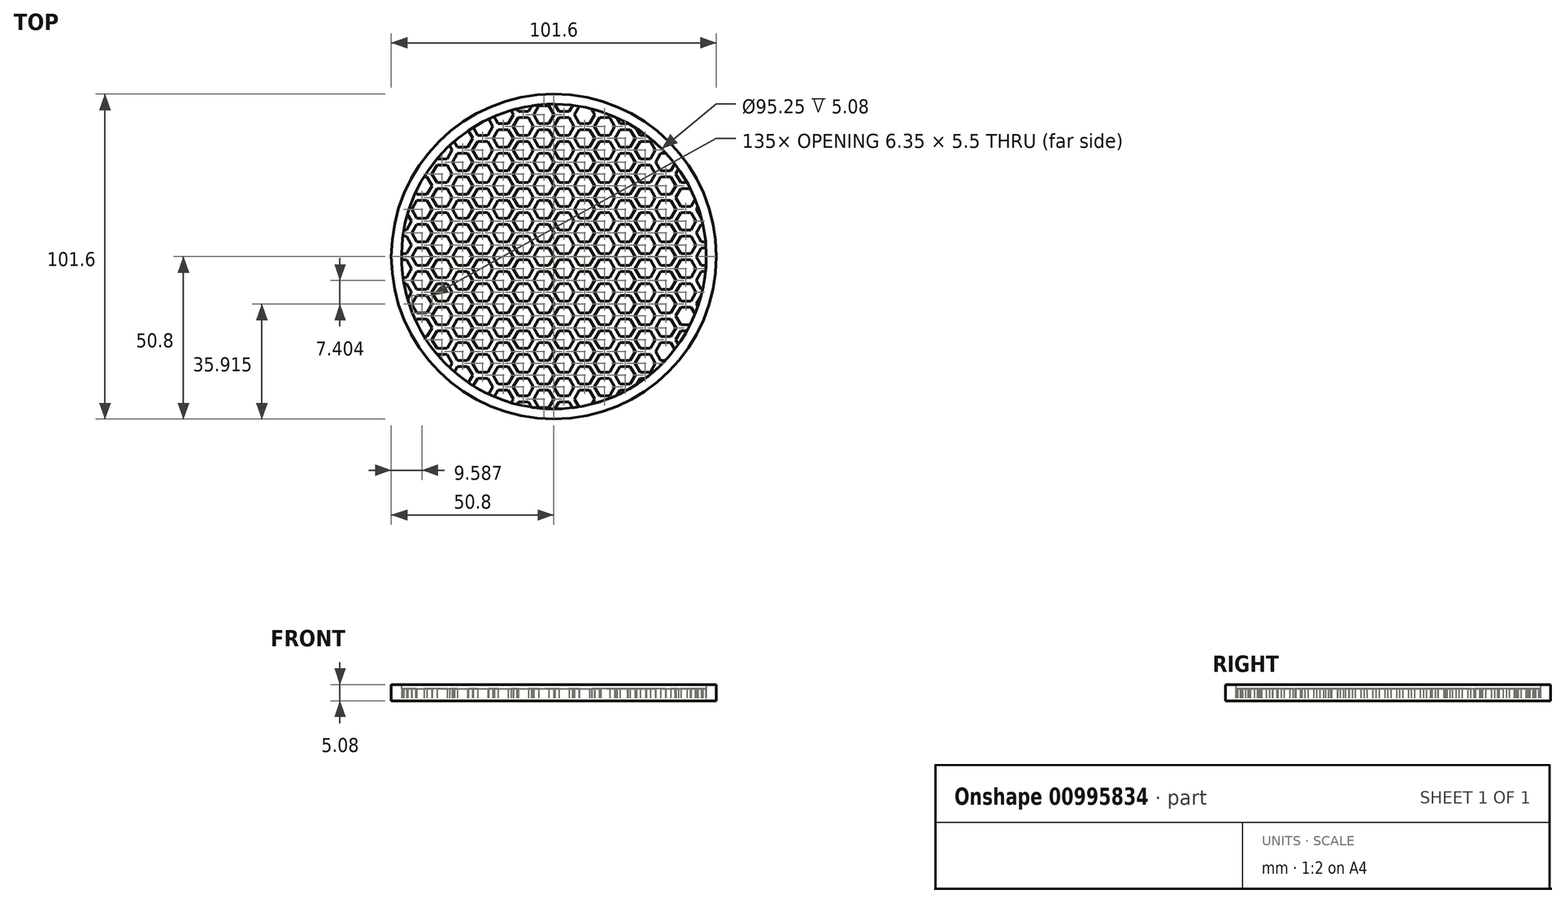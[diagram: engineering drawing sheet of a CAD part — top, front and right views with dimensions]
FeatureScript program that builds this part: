
annotation { "Feature Type Name" : "Feature", "Feature Type Description" : "" }
export const myFeature = defineFeature(function(context is Context, id is Id, definition is map)
    precondition{}
    {
        {
            var Q0;
            Q0=qCreatedBy(makeId("Top.planeOp"),FACE);
            var sketch = newSketch(context, id + "F0", { "sketchPlane" : qUnion([Q0])});
            skLineSegment(sketch, "E0.bottom", {"start": v(50.8, -50.8) * mm, "end": v(-50.8, -50.8) * mm});
            skLineSegment(sketch, "E0.top", {"start": v(50.8, 50.8) * mm, "end": v(-50.8, 50.8) * mm, "construction": true});
            skLineSegment(sketch, "E0.left", {"start": v(50.8, -50.8) * mm, "end": v(50.8, 50.8) * mm});
            skLineSegment(sketch, "E0.right", {"start": v(-50.8, -50.8) * mm, "end": v(-50.8, 50.8) * mm});
            skPoint(sketch, "E0.middle", {"position": v(0, 0) * mm});
            skCircle(sketch, "E1.cCircle", {"center": v(-47.63, 48.05) * mm, "radius": 3.18 * mm, "construction": true});
            skLineSegment(sketch, "E1.0", {"start": v(-46.04, 45.3) * mm, "end": v(-49.21, 45.3) * mm});
            skLineSegment(sketch, "E1.1", {"start": v(-49.21, 45.3) * mm, "end": v(-50.8, 48.05) * mm});
            skLineSegment(sketch, "E1.2", {"start": v(-50.8, 48.05) * mm, "end": v(-49.21, 50.8) * mm});
            skLineSegment(sketch, "E1.3", {"start": v(-49.21, 50.8) * mm, "end": v(-46.04, 50.8) * mm});
            skLineSegment(sketch, "E1.4", {"start": v(-46.04, 50.8) * mm, "end": v(-44.45, 48.05) * mm});
            skLineSegment(sketch, "E1.5", {"start": v(-44.45, 48.05) * mm, "end": v(-46.04, 45.3) * mm});
            skCircle(sketch, "E2.cCircle", {"center": v(-41.21, 44.35) * mm, "radius": 3.18 * mm, "construction": true});
            skLineSegment(sketch, "E2.0", {"start": v(-39.63, 47.1) * mm, "end": v(-38.04, 44.35) * mm});
            skLineSegment(sketch, "E2.1", {"start": v(-38.04, 44.35) * mm, "end": v(-39.63, 41.6) * mm});
            skLineSegment(sketch, "E2.2", {"start": v(-39.63, 41.6) * mm, "end": v(-42.8, 41.6) * mm});
            skLineSegment(sketch, "E2.3", {"start": v(-42.8, 41.6) * mm, "end": v(-44.39, 44.35) * mm});
            skLineSegment(sketch, "E2.4", {"start": v(-44.39, 44.35) * mm, "end": v(-42.8, 47.1) * mm});
            skLineSegment(sketch, "E2.5", {"start": v(-42.8, 47.1) * mm, "end": v(-39.63, 47.1) * mm});
            skCircle(sketch, "E3.cCircle", {"center": v(-41.21, 51.75) * mm, "radius": 3.18 * mm, "construction": true});
            skPoint(sketch, "E3.cCircle.centerSnap0", {"position": v(-41.21, 47.1) * mm});
            skLineSegment(sketch, "E3.0", {"start": v(-38.04, 51.75) * mm, "end": v(-39.63, 49) * mm});
            skLineSegment(sketch, "E3.1", {"start": v(-39.63, 49) * mm, "end": v(-42.8, 49) * mm});
            skLineSegment(sketch, "E3.2", {"start": v(-42.8, 49) * mm, "end": v(-44.39, 51.75) * mm});
            skLineSegment(sketch, "E3.3", {"start": v(-44.39, 51.75) * mm, "end": v(-42.8, 54.5) * mm});
            skLineSegment(sketch, "E3.4", {"start": v(-42.8, 54.5) * mm, "end": v(-39.63, 54.5) * mm});
            skLineSegment(sketch, "E3.5", {"start": v(-39.63, 54.5) * mm, "end": v(-38.04, 51.75) * mm});
            skCircle(sketch, "E4.cCircle", {"center": v(-47.63, 40.65) * mm, "radius": 3.18 * mm, "construction": true});
            skPoint(sketch, "E4.cCircle.centerSnap0", {"position": v(-47.62, 45.3) * mm});
            skLineSegment(sketch, "E4.0", {"start": v(-49.21, 37.9) * mm, "end": v(-50.8, 40.65) * mm});
            skLineSegment(sketch, "E4.1", {"start": v(-50.8, 40.65) * mm, "end": v(-49.21, 43.4) * mm});
            skLineSegment(sketch, "E4.2", {"start": v(-49.21, 43.4) * mm, "end": v(-46.04, 43.4) * mm});
            skLineSegment(sketch, "E4.3", {"start": v(-46.04, 43.4) * mm, "end": v(-44.45, 40.65) * mm});
            skLineSegment(sketch, "E4.4", {"start": v(-44.45, 40.65) * mm, "end": v(-46.04, 37.9) * mm});
            skLineSegment(sketch, "E4.5", {"start": v(-46.04, 37.9) * mm, "end": v(-49.21, 37.9) * mm});
            skLineSegment(sketch, "E5.0.1.0", {"start": v(-42.8, 32.29) * mm, "end": v(-39.63, 32.29) * mm});
            skLineSegment(sketch, "E5.0.1.1", {"start": v(-46.04, 30.5) * mm, "end": v(-49.21, 30.5) * mm});
            skLineSegment(sketch, "E5.0.1.2", {"start": v(-44.45, 25.84) * mm, "end": v(-46.04, 23.09) * mm});
            skLineSegment(sketch, "E5.0.1.3", {"start": v(-39.63, 32.29) * mm, "end": v(-38.04, 29.54) * mm});
            skLineSegment(sketch, "E5.0.1.4", {"start": v(-44.39, 36.94) * mm, "end": v(-42.8, 39.7) * mm});
            skLineSegment(sketch, "E5.0.1.5", {"start": v(-50.8, 33.24) * mm, "end": v(-49.21, 36) * mm});
            skLineSegment(sketch, "E5.0.1.6", {"start": v(-39.63, 39.7) * mm, "end": v(-38.04, 36.94) * mm});
            skLineSegment(sketch, "E5.0.1.7", {"start": v(-39.63, 26.8) * mm, "end": v(-42.8, 26.8) * mm});
            skLineSegment(sketch, "E5.0.1.8", {"start": v(-38.04, 36.94) * mm, "end": v(-39.63, 34.2) * mm});
            skLineSegment(sketch, "E5.0.1.9", {"start": v(-50.8, 25.84) * mm, "end": v(-49.21, 28.59) * mm});
            skLineSegment(sketch, "E5.0.1.10", {"start": v(-46.04, 36) * mm, "end": v(-44.45, 33.24) * mm});
            skLineSegment(sketch, "E5.0.1.11", {"start": v(-44.39, 29.54) * mm, "end": v(-42.8, 32.29) * mm});
            skLineSegment(sketch, "E5.0.1.12", {"start": v(-42.8, 34.2) * mm, "end": v(-44.39, 36.94) * mm});
            skLineSegment(sketch, "E5.0.1.13", {"start": v(-46.04, 28.59) * mm, "end": v(-44.45, 25.84) * mm});
            skLineSegment(sketch, "E5.0.1.14", {"start": v(-42.8, 39.7) * mm, "end": v(-39.63, 39.7) * mm});
            skLineSegment(sketch, "E5.0.1.15", {"start": v(-46.04, 23.09) * mm, "end": v(-49.21, 23.09) * mm});
            skLineSegment(sketch, "E5.0.1.16", {"start": v(-49.21, 30.5) * mm, "end": v(-50.8, 33.24) * mm});
            skLineSegment(sketch, "E5.0.1.17", {"start": v(-38.04, 29.54) * mm, "end": v(-39.63, 26.8) * mm});
            skLineSegment(sketch, "E5.0.1.18", {"start": v(-49.21, 23.09) * mm, "end": v(-50.8, 25.84) * mm});
            skLineSegment(sketch, "E5.0.1.19", {"start": v(-49.21, 36) * mm, "end": v(-46.04, 36) * mm});
            skLineSegment(sketch, "E5.0.1.20", {"start": v(-42.8, 26.8) * mm, "end": v(-44.39, 29.54) * mm});
            skLineSegment(sketch, "E5.0.1.21", {"start": v(-39.63, 34.2) * mm, "end": v(-42.8, 34.2) * mm});
            skLineSegment(sketch, "E5.0.1.22", {"start": v(-49.21, 28.59) * mm, "end": v(-46.04, 28.59) * mm});
            skLineSegment(sketch, "E5.0.1.23", {"start": v(-44.45, 33.24) * mm, "end": v(-46.04, 30.5) * mm});
            skLineSegment(sketch, "E5.0.2.0", {"start": v(-42.8, 17.48) * mm, "end": v(-39.63, 17.48) * mm});
            skLineSegment(sketch, "E5.0.2.1", {"start": v(-46.04, 15.68) * mm, "end": v(-49.21, 15.68) * mm});
            skLineSegment(sketch, "E5.0.2.2", {"start": v(-44.45, 11.03) * mm, "end": v(-46.04, 8.28) * mm});
            skLineSegment(sketch, "E5.0.2.3", {"start": v(-39.63, 17.48) * mm, "end": v(-38.04, 14.73) * mm});
            skLineSegment(sketch, "E5.0.2.4", {"start": v(-44.39, 22.14) * mm, "end": v(-42.8, 24.89) * mm});
            skLineSegment(sketch, "E5.0.2.5", {"start": v(-50.8, 18.43) * mm, "end": v(-49.21, 21.18) * mm});
            skLineSegment(sketch, "E5.0.2.6", {"start": v(-39.63, 24.89) * mm, "end": v(-38.04, 22.14) * mm});
            skLineSegment(sketch, "E5.0.2.7", {"start": v(-39.63, 11.98) * mm, "end": v(-42.8, 11.98) * mm});
            skLineSegment(sketch, "E5.0.2.8", {"start": v(-38.04, 22.14) * mm, "end": v(-39.63, 19.39) * mm});
            skLineSegment(sketch, "E5.0.2.9", {"start": v(-50.8, 11.03) * mm, "end": v(-49.21, 13.78) * mm});
            skLineSegment(sketch, "E5.0.2.10", {"start": v(-46.04, 21.18) * mm, "end": v(-44.45, 18.43) * mm});
            skLineSegment(sketch, "E5.0.2.11", {"start": v(-44.39, 14.73) * mm, "end": v(-42.8, 17.48) * mm});
            skLineSegment(sketch, "E5.0.2.12", {"start": v(-42.8, 19.39) * mm, "end": v(-44.39, 22.14) * mm});
            skLineSegment(sketch, "E5.0.2.13", {"start": v(-46.04, 13.78) * mm, "end": v(-44.45, 11.03) * mm});
            skLineSegment(sketch, "E5.0.2.14", {"start": v(-42.8, 24.89) * mm, "end": v(-39.63, 24.89) * mm});
            skLineSegment(sketch, "E5.0.2.15", {"start": v(-46.04, 8.28) * mm, "end": v(-49.21, 8.28) * mm});
            skLineSegment(sketch, "E5.0.2.16", {"start": v(-49.21, 15.68) * mm, "end": v(-50.8, 18.43) * mm});
            skLineSegment(sketch, "E5.0.2.17", {"start": v(-38.04, 14.73) * mm, "end": v(-39.63, 11.98) * mm});
            skLineSegment(sketch, "E5.0.2.18", {"start": v(-49.21, 8.28) * mm, "end": v(-50.8, 11.03) * mm});
            skLineSegment(sketch, "E5.0.2.19", {"start": v(-49.21, 21.18) * mm, "end": v(-46.04, 21.18) * mm});
            skLineSegment(sketch, "E5.0.2.20", {"start": v(-42.8, 11.98) * mm, "end": v(-44.39, 14.73) * mm});
            skLineSegment(sketch, "E5.0.2.21", {"start": v(-39.63, 19.39) * mm, "end": v(-42.8, 19.39) * mm});
            skLineSegment(sketch, "E5.0.2.22", {"start": v(-49.21, 13.78) * mm, "end": v(-46.04, 13.78) * mm});
            skLineSegment(sketch, "E5.0.2.23", {"start": v(-44.45, 18.43) * mm, "end": v(-46.04, 15.68) * mm});
            skLineSegment(sketch, "E5.0.3.0", {"start": v(-42.8, 2.67) * mm, "end": v(-39.63, 2.67) * mm});
            skLineSegment(sketch, "E5.0.3.1", {"start": v(-46.04, 0.88) * mm, "end": v(-49.21, 0.88) * mm});
            skLineSegment(sketch, "E5.0.3.2", {"start": v(-44.45, -3.78) * mm, "end": v(-46.04, -6.53) * mm});
            skLineSegment(sketch, "E5.0.3.3", {"start": v(-39.63, 2.67) * mm, "end": v(-38.04, -0.08) * mm});
            skLineSegment(sketch, "E5.0.3.4", {"start": v(-44.39, 7.33) * mm, "end": v(-42.8, 10.08) * mm});
            skLineSegment(sketch, "E5.0.3.5", {"start": v(-50.8, 3.63) * mm, "end": v(-49.21, 6.38) * mm});
            skLineSegment(sketch, "E5.0.3.6", {"start": v(-39.63, 10.08) * mm, "end": v(-38.04, 7.33) * mm});
            skLineSegment(sketch, "E5.0.3.7", {"start": v(-39.63, -2.83) * mm, "end": v(-42.8, -2.83) * mm});
            skLineSegment(sketch, "E5.0.3.8", {"start": v(-38.04, 7.33) * mm, "end": v(-39.63, 4.58) * mm});
            skLineSegment(sketch, "E5.0.3.9", {"start": v(-50.8, -3.78) * mm, "end": v(-49.21, -1.03) * mm});
            skLineSegment(sketch, "E5.0.3.10", {"start": v(-46.04, 6.38) * mm, "end": v(-44.45, 3.63) * mm});
            skLineSegment(sketch, "E5.0.3.11", {"start": v(-44.39, -0.08) * mm, "end": v(-42.8, 2.67) * mm});
            skLineSegment(sketch, "E5.0.3.12", {"start": v(-42.8, 4.58) * mm, "end": v(-44.39, 7.33) * mm});
            skLineSegment(sketch, "E5.0.3.13", {"start": v(-46.04, -1.03) * mm, "end": v(-44.45, -3.78) * mm});
            skLineSegment(sketch, "E5.0.3.14", {"start": v(-42.8, 10.08) * mm, "end": v(-39.63, 10.08) * mm});
            skLineSegment(sketch, "E5.0.3.15", {"start": v(-46.04, -6.53) * mm, "end": v(-49.21, -6.53) * mm});
            skLineSegment(sketch, "E5.0.3.16", {"start": v(-49.21, 0.88) * mm, "end": v(-50.8, 3.63) * mm});
            skLineSegment(sketch, "E5.0.3.17", {"start": v(-38.04, -0.08) * mm, "end": v(-39.63, -2.83) * mm});
            skLineSegment(sketch, "E5.0.3.18", {"start": v(-49.21, -6.53) * mm, "end": v(-50.8, -3.78) * mm});
            skLineSegment(sketch, "E5.0.3.19", {"start": v(-49.21, 6.38) * mm, "end": v(-46.04, 6.38) * mm});
            skLineSegment(sketch, "E5.0.3.20", {"start": v(-42.8, -2.83) * mm, "end": v(-44.39, -0.08) * mm});
            skLineSegment(sketch, "E5.0.3.21", {"start": v(-39.63, 4.58) * mm, "end": v(-42.8, 4.58) * mm});
            skLineSegment(sketch, "E5.0.3.22", {"start": v(-49.21, -1.03) * mm, "end": v(-46.04, -1.03) * mm});
            skLineSegment(sketch, "E5.0.3.23", {"start": v(-44.45, 3.63) * mm, "end": v(-46.04, 0.88) * mm});
            skLineSegment(sketch, "E5.0.4.0", {"start": v(-42.8, -12.13) * mm, "end": v(-39.63, -12.13) * mm});
            skLineSegment(sketch, "E5.0.4.1", {"start": v(-46.04, -13.93) * mm, "end": v(-49.21, -13.93) * mm});
            skLineSegment(sketch, "E5.0.4.2", {"start": v(-44.45, -18.59) * mm, "end": v(-46.04, -21.34) * mm});
            skLineSegment(sketch, "E5.0.4.3", {"start": v(-39.63, -12.13) * mm, "end": v(-38.04, -14.88) * mm});
            skLineSegment(sketch, "E5.0.4.4", {"start": v(-44.39, -7.48) * mm, "end": v(-42.8, -4.73) * mm});
            skLineSegment(sketch, "E5.0.4.5", {"start": v(-50.8, -11.18) * mm, "end": v(-49.21, -8.43) * mm});
            skLineSegment(sketch, "E5.0.4.6", {"start": v(-39.63, -4.73) * mm, "end": v(-38.04, -7.48) * mm});
            skLineSegment(sketch, "E5.0.4.7", {"start": v(-39.63, -17.63) * mm, "end": v(-42.8, -17.63) * mm});
            skLineSegment(sketch, "E5.0.4.8", {"start": v(-38.04, -7.48) * mm, "end": v(-39.63, -10.23) * mm});
            skLineSegment(sketch, "E5.0.4.9", {"start": v(-50.8, -18.59) * mm, "end": v(-49.21, -15.84) * mm});
            skLineSegment(sketch, "E5.0.4.10", {"start": v(-46.04, -8.43) * mm, "end": v(-44.45, -11.18) * mm});
            skLineSegment(sketch, "E5.0.4.11", {"start": v(-44.39, -14.88) * mm, "end": v(-42.8, -12.13) * mm});
            skLineSegment(sketch, "E5.0.4.12", {"start": v(-42.8, -10.23) * mm, "end": v(-44.39, -7.48) * mm});
            skLineSegment(sketch, "E5.0.4.13", {"start": v(-46.04, -15.84) * mm, "end": v(-44.45, -18.59) * mm});
            skLineSegment(sketch, "E5.0.4.14", {"start": v(-42.8, -4.73) * mm, "end": v(-39.63, -4.73) * mm});
            skLineSegment(sketch, "E5.0.4.15", {"start": v(-46.04, -21.34) * mm, "end": v(-49.21, -21.34) * mm});
            skLineSegment(sketch, "E5.0.4.16", {"start": v(-49.21, -13.93) * mm, "end": v(-50.8, -11.18) * mm});
            skLineSegment(sketch, "E5.0.4.17", {"start": v(-38.04, -14.88) * mm, "end": v(-39.63, -17.63) * mm});
            skLineSegment(sketch, "E5.0.4.18", {"start": v(-49.21, -21.34) * mm, "end": v(-50.8, -18.59) * mm});
            skLineSegment(sketch, "E5.0.4.19", {"start": v(-49.21, -8.43) * mm, "end": v(-46.04, -8.43) * mm});
            skLineSegment(sketch, "E5.0.4.20", {"start": v(-42.8, -17.63) * mm, "end": v(-44.39, -14.88) * mm});
            skLineSegment(sketch, "E5.0.4.21", {"start": v(-39.63, -10.23) * mm, "end": v(-42.8, -10.23) * mm});
            skLineSegment(sketch, "E5.0.4.22", {"start": v(-49.21, -15.84) * mm, "end": v(-46.04, -15.84) * mm});
            skLineSegment(sketch, "E5.0.4.23", {"start": v(-44.45, -11.18) * mm, "end": v(-46.04, -13.93) * mm});
            skLineSegment(sketch, "E5.0.5.0", {"start": v(-42.8, -26.94) * mm, "end": v(-39.63, -26.94) * mm});
            skLineSegment(sketch, "E5.0.5.1", {"start": v(-46.04, -28.74) * mm, "end": v(-49.21, -28.74) * mm});
            skLineSegment(sketch, "E5.0.5.2", {"start": v(-44.45, -33.4) * mm, "end": v(-46.04, -36.14) * mm});
            skLineSegment(sketch, "E5.0.5.3", {"start": v(-39.63, -26.94) * mm, "end": v(-38.04, -29.7) * mm});
            skLineSegment(sketch, "E5.0.5.4", {"start": v(-44.39, -22.29) * mm, "end": v(-42.8, -19.54) * mm});
            skLineSegment(sketch, "E5.0.5.5", {"start": v(-50.8, -26) * mm, "end": v(-49.21, -23.24) * mm});
            skLineSegment(sketch, "E5.0.5.6", {"start": v(-39.63, -19.54) * mm, "end": v(-38.04, -22.29) * mm});
            skLineSegment(sketch, "E5.0.5.7", {"start": v(-39.63, -32.44) * mm, "end": v(-42.8, -32.44) * mm});
            skLineSegment(sketch, "E5.0.5.8", {"start": v(-38.04, -22.29) * mm, "end": v(-39.63, -25.04) * mm});
            skLineSegment(sketch, "E5.0.5.9", {"start": v(-50.8, -33.4) * mm, "end": v(-49.21, -30.65) * mm});
            skLineSegment(sketch, "E5.0.5.10", {"start": v(-46.04, -23.24) * mm, "end": v(-44.45, -26) * mm});
            skLineSegment(sketch, "E5.0.5.11", {"start": v(-44.39, -29.7) * mm, "end": v(-42.8, -26.94) * mm});
            skLineSegment(sketch, "E5.0.5.12", {"start": v(-42.8, -25.04) * mm, "end": v(-44.39, -22.29) * mm});
            skLineSegment(sketch, "E5.0.5.13", {"start": v(-46.04, -30.65) * mm, "end": v(-44.45, -33.4) * mm});
            skLineSegment(sketch, "E5.0.5.14", {"start": v(-42.8, -19.54) * mm, "end": v(-39.63, -19.54) * mm});
            skLineSegment(sketch, "E5.0.5.15", {"start": v(-46.04, -36.14) * mm, "end": v(-49.21, -36.14) * mm});
            skLineSegment(sketch, "E5.0.5.16", {"start": v(-49.21, -28.74) * mm, "end": v(-50.8, -26) * mm});
            skLineSegment(sketch, "E5.0.5.17", {"start": v(-38.04, -29.7) * mm, "end": v(-39.63, -32.44) * mm});
            skLineSegment(sketch, "E5.0.5.18", {"start": v(-49.21, -36.14) * mm, "end": v(-50.8, -33.4) * mm});
            skLineSegment(sketch, "E5.0.5.19", {"start": v(-49.21, -23.24) * mm, "end": v(-46.04, -23.24) * mm});
            skLineSegment(sketch, "E5.0.5.20", {"start": v(-42.8, -32.44) * mm, "end": v(-44.39, -29.7) * mm});
            skLineSegment(sketch, "E5.0.5.21", {"start": v(-39.63, -25.04) * mm, "end": v(-42.8, -25.04) * mm});
            skLineSegment(sketch, "E5.0.5.22", {"start": v(-49.21, -30.65) * mm, "end": v(-46.04, -30.65) * mm});
            skLineSegment(sketch, "E5.0.5.23", {"start": v(-44.45, -26) * mm, "end": v(-46.04, -28.74) * mm});
            skLineSegment(sketch, "E5.0.6.0", {"start": v(-42.8, -41.75) * mm, "end": v(-39.63, -41.75) * mm});
            skLineSegment(sketch, "E5.0.6.1", {"start": v(-46.04, -43.55) * mm, "end": v(-49.21, -43.55) * mm});
            skLineSegment(sketch, "E5.0.6.2", {"start": v(-44.45, -48.2) * mm, "end": v(-46.04, -50.95) * mm});
            skLineSegment(sketch, "E5.0.6.3", {"start": v(-39.63, -41.75) * mm, "end": v(-38.04, -44.5) * mm});
            skLineSegment(sketch, "E5.0.6.4", {"start": v(-44.39, -37.1) * mm, "end": v(-42.8, -34.35) * mm});
            skLineSegment(sketch, "E5.0.6.5", {"start": v(-50.8, -40.8) * mm, "end": v(-49.21, -38.05) * mm});
            skLineSegment(sketch, "E5.0.6.6", {"start": v(-39.63, -34.35) * mm, "end": v(-38.04, -37.1) * mm});
            skLineSegment(sketch, "E5.0.6.7", {"start": v(-39.63, -47.25) * mm, "end": v(-42.8, -47.25) * mm});
            skLineSegment(sketch, "E5.0.6.8", {"start": v(-38.04, -37.1) * mm, "end": v(-39.63, -39.85) * mm});
            skLineSegment(sketch, "E5.0.6.9", {"start": v(-50.8, -48.2) * mm, "end": v(-49.21, -45.45) * mm});
            skLineSegment(sketch, "E5.0.6.10", {"start": v(-46.04, -38.05) * mm, "end": v(-44.45, -40.8) * mm});
            skLineSegment(sketch, "E5.0.6.11", {"start": v(-44.39, -44.5) * mm, "end": v(-42.8, -41.75) * mm});
            skLineSegment(sketch, "E5.0.6.12", {"start": v(-42.8, -39.85) * mm, "end": v(-44.39, -37.1) * mm});
            skLineSegment(sketch, "E5.0.6.13", {"start": v(-46.04, -45.45) * mm, "end": v(-44.45, -48.2) * mm});
            skLineSegment(sketch, "E5.0.6.14", {"start": v(-42.8, -34.35) * mm, "end": v(-39.63, -34.35) * mm});
            skLineSegment(sketch, "E5.0.6.15", {"start": v(-46.04, -50.95) * mm, "end": v(-49.21, -50.95) * mm});
            skLineSegment(sketch, "E5.0.6.16", {"start": v(-49.21, -43.55) * mm, "end": v(-50.8, -40.8) * mm});
            skLineSegment(sketch, "E5.0.6.17", {"start": v(-38.04, -44.5) * mm, "end": v(-39.63, -47.25) * mm});
            skLineSegment(sketch, "E5.0.6.18", {"start": v(-49.21, -50.95) * mm, "end": v(-50.8, -48.2) * mm});
            skLineSegment(sketch, "E5.0.6.19", {"start": v(-49.21, -38.05) * mm, "end": v(-46.04, -38.05) * mm});
            skLineSegment(sketch, "E5.0.6.20", {"start": v(-42.8, -47.25) * mm, "end": v(-44.39, -44.5) * mm});
            skLineSegment(sketch, "E5.0.6.21", {"start": v(-39.63, -39.85) * mm, "end": v(-42.8, -39.85) * mm});
            skLineSegment(sketch, "E5.0.6.22", {"start": v(-49.21, -45.45) * mm, "end": v(-46.04, -45.45) * mm});
            skLineSegment(sketch, "E5.0.6.23", {"start": v(-44.45, -40.8) * mm, "end": v(-46.04, -43.55) * mm});
            skLineSegment(sketch, "E5.1.0.0", {"start": v(-30.1, 47.1) * mm, "end": v(-26.93, 47.1) * mm});
            skLineSegment(sketch, "E5.1.0.1", {"start": v(-33.34, 45.3) * mm, "end": v(-36.51, 45.3) * mm});
            skLineSegment(sketch, "E5.1.0.2", {"start": v(-31.75, 40.65) * mm, "end": v(-33.34, 37.9) * mm});
            skLineSegment(sketch, "E5.1.0.3", {"start": v(-26.93, 47.1) * mm, "end": v(-25.34, 44.35) * mm});
            skLineSegment(sketch, "E5.1.0.4", {"start": v(-31.69, 51.75) * mm, "end": v(-30.1, 54.5) * mm});
            skLineSegment(sketch, "E5.1.0.5", {"start": v(-38.1, 48.05) * mm, "end": v(-36.51, 50.8) * mm});
            skLineSegment(sketch, "E5.1.0.6", {"start": v(-26.93, 54.5) * mm, "end": v(-25.34, 51.75) * mm});
            skLineSegment(sketch, "E5.1.0.7", {"start": v(-26.93, 41.6) * mm, "end": v(-30.1, 41.6) * mm});
            skLineSegment(sketch, "E5.1.0.8", {"start": v(-25.34, 51.75) * mm, "end": v(-26.93, 49) * mm});
            skLineSegment(sketch, "E5.1.0.9", {"start": v(-38.1, 40.65) * mm, "end": v(-36.51, 43.4) * mm});
            skLineSegment(sketch, "E5.1.0.10", {"start": v(-33.34, 50.8) * mm, "end": v(-31.75, 48.05) * mm});
            skLineSegment(sketch, "E5.1.0.11", {"start": v(-31.69, 44.35) * mm, "end": v(-30.1, 47.1) * mm});
            skLineSegment(sketch, "E5.1.0.12", {"start": v(-30.1, 49) * mm, "end": v(-31.69, 51.75) * mm});
            skLineSegment(sketch, "E5.1.0.13", {"start": v(-33.34, 43.4) * mm, "end": v(-31.75, 40.65) * mm});
            skLineSegment(sketch, "E5.1.0.14", {"start": v(-30.1, 54.5) * mm, "end": v(-26.93, 54.5) * mm});
            skLineSegment(sketch, "E5.1.0.15", {"start": v(-33.34, 37.9) * mm, "end": v(-36.51, 37.9) * mm});
            skLineSegment(sketch, "E5.1.0.16", {"start": v(-36.51, 45.3) * mm, "end": v(-38.1, 48.05) * mm});
            skLineSegment(sketch, "E5.1.0.17", {"start": v(-25.34, 44.35) * mm, "end": v(-26.93, 41.6) * mm});
            skLineSegment(sketch, "E5.1.0.18", {"start": v(-36.51, 37.9) * mm, "end": v(-38.1, 40.65) * mm});
            skLineSegment(sketch, "E5.1.0.19", {"start": v(-36.51, 50.8) * mm, "end": v(-33.34, 50.8) * mm});
            skLineSegment(sketch, "E5.1.0.20", {"start": v(-30.1, 41.6) * mm, "end": v(-31.69, 44.35) * mm});
            skLineSegment(sketch, "E5.1.0.21", {"start": v(-26.93, 49) * mm, "end": v(-30.1, 49) * mm});
            skLineSegment(sketch, "E5.1.0.22", {"start": v(-36.51, 43.4) * mm, "end": v(-33.34, 43.4) * mm});
            skLineSegment(sketch, "E5.1.0.23", {"start": v(-31.75, 48.05) * mm, "end": v(-33.34, 45.3) * mm});
            skLineSegment(sketch, "E5.1.1.0", {"start": v(-30.1, 32.29) * mm, "end": v(-26.93, 32.29) * mm});
            skLineSegment(sketch, "E5.1.1.1", {"start": v(-33.34, 30.5) * mm, "end": v(-36.51, 30.5) * mm});
            skLineSegment(sketch, "E5.1.1.2", {"start": v(-31.75, 25.84) * mm, "end": v(-33.34, 23.09) * mm});
            skLineSegment(sketch, "E5.1.1.3", {"start": v(-26.93, 32.29) * mm, "end": v(-25.34, 29.54) * mm});
            skLineSegment(sketch, "E5.1.1.4", {"start": v(-31.69, 36.94) * mm, "end": v(-30.1, 39.7) * mm});
            skLineSegment(sketch, "E5.1.1.5", {"start": v(-38.1, 33.24) * mm, "end": v(-36.51, 36) * mm});
            skLineSegment(sketch, "E5.1.1.6", {"start": v(-26.93, 39.7) * mm, "end": v(-25.34, 36.94) * mm});
            skLineSegment(sketch, "E5.1.1.7", {"start": v(-26.93, 26.8) * mm, "end": v(-30.1, 26.8) * mm});
            skLineSegment(sketch, "E5.1.1.8", {"start": v(-25.34, 36.94) * mm, "end": v(-26.93, 34.2) * mm});
            skLineSegment(sketch, "E5.1.1.9", {"start": v(-38.1, 25.84) * mm, "end": v(-36.51, 28.59) * mm});
            skLineSegment(sketch, "E5.1.1.10", {"start": v(-33.34, 36) * mm, "end": v(-31.75, 33.24) * mm});
            skLineSegment(sketch, "E5.1.1.11", {"start": v(-31.69, 29.54) * mm, "end": v(-30.1, 32.29) * mm});
            skLineSegment(sketch, "E5.1.1.12", {"start": v(-30.1, 34.2) * mm, "end": v(-31.69, 36.94) * mm});
            skLineSegment(sketch, "E5.1.1.13", {"start": v(-33.34, 28.59) * mm, "end": v(-31.75, 25.84) * mm});
            skLineSegment(sketch, "E5.1.1.14", {"start": v(-30.1, 39.7) * mm, "end": v(-26.93, 39.7) * mm});
            skLineSegment(sketch, "E5.1.1.15", {"start": v(-33.34, 23.09) * mm, "end": v(-36.51, 23.09) * mm});
            skLineSegment(sketch, "E5.1.1.16", {"start": v(-36.51, 30.5) * mm, "end": v(-38.1, 33.24) * mm});
            skLineSegment(sketch, "E5.1.1.17", {"start": v(-25.34, 29.54) * mm, "end": v(-26.93, 26.8) * mm});
            skLineSegment(sketch, "E5.1.1.18", {"start": v(-36.51, 23.09) * mm, "end": v(-38.1, 25.84) * mm});
            skLineSegment(sketch, "E5.1.1.19", {"start": v(-36.51, 36) * mm, "end": v(-33.34, 36) * mm});
            skLineSegment(sketch, "E5.1.1.20", {"start": v(-30.1, 26.8) * mm, "end": v(-31.69, 29.54) * mm});
            skLineSegment(sketch, "E5.1.1.21", {"start": v(-26.93, 34.2) * mm, "end": v(-30.1, 34.2) * mm});
            skLineSegment(sketch, "E5.1.1.22", {"start": v(-36.51, 28.59) * mm, "end": v(-33.34, 28.59) * mm});
            skLineSegment(sketch, "E5.1.1.23", {"start": v(-31.75, 33.24) * mm, "end": v(-33.34, 30.5) * mm});
            skLineSegment(sketch, "E5.1.2.0", {"start": v(-30.1, 17.48) * mm, "end": v(-26.93, 17.48) * mm});
            skLineSegment(sketch, "E5.1.2.1", {"start": v(-33.34, 15.68) * mm, "end": v(-36.51, 15.68) * mm});
            skLineSegment(sketch, "E5.1.2.2", {"start": v(-31.75, 11.03) * mm, "end": v(-33.34, 8.28) * mm});
            skLineSegment(sketch, "E5.1.2.3", {"start": v(-26.93, 17.48) * mm, "end": v(-25.34, 14.73) * mm});
            skLineSegment(sketch, "E5.1.2.4", {"start": v(-31.69, 22.14) * mm, "end": v(-30.1, 24.89) * mm});
            skLineSegment(sketch, "E5.1.2.5", {"start": v(-38.1, 18.43) * mm, "end": v(-36.51, 21.18) * mm});
            skLineSegment(sketch, "E5.1.2.6", {"start": v(-26.93, 24.89) * mm, "end": v(-25.34, 22.14) * mm});
            skLineSegment(sketch, "E5.1.2.7", {"start": v(-26.93, 11.98) * mm, "end": v(-30.1, 11.98) * mm});
            skLineSegment(sketch, "E5.1.2.8", {"start": v(-25.34, 22.14) * mm, "end": v(-26.93, 19.39) * mm});
            skLineSegment(sketch, "E5.1.2.9", {"start": v(-38.1, 11.03) * mm, "end": v(-36.51, 13.78) * mm});
            skLineSegment(sketch, "E5.1.2.10", {"start": v(-33.34, 21.18) * mm, "end": v(-31.75, 18.43) * mm});
            skLineSegment(sketch, "E5.1.2.11", {"start": v(-31.69, 14.73) * mm, "end": v(-30.1, 17.48) * mm});
            skLineSegment(sketch, "E5.1.2.12", {"start": v(-30.1, 19.39) * mm, "end": v(-31.69, 22.14) * mm});
            skLineSegment(sketch, "E5.1.2.13", {"start": v(-33.34, 13.78) * mm, "end": v(-31.75, 11.03) * mm});
            skLineSegment(sketch, "E5.1.2.14", {"start": v(-30.1, 24.89) * mm, "end": v(-26.93, 24.89) * mm});
            skLineSegment(sketch, "E5.1.2.15", {"start": v(-33.34, 8.28) * mm, "end": v(-36.51, 8.28) * mm});
            skLineSegment(sketch, "E5.1.2.16", {"start": v(-36.51, 15.68) * mm, "end": v(-38.1, 18.43) * mm});
            skLineSegment(sketch, "E5.1.2.17", {"start": v(-25.34, 14.73) * mm, "end": v(-26.93, 11.98) * mm});
            skLineSegment(sketch, "E5.1.2.18", {"start": v(-36.51, 8.28) * mm, "end": v(-38.1, 11.03) * mm});
            skLineSegment(sketch, "E5.1.2.19", {"start": v(-36.51, 21.18) * mm, "end": v(-33.34, 21.18) * mm});
            skLineSegment(sketch, "E5.1.2.20", {"start": v(-30.1, 11.98) * mm, "end": v(-31.69, 14.73) * mm});
            skLineSegment(sketch, "E5.1.2.21", {"start": v(-26.93, 19.39) * mm, "end": v(-30.1, 19.39) * mm});
            skLineSegment(sketch, "E5.1.2.22", {"start": v(-36.51, 13.78) * mm, "end": v(-33.34, 13.78) * mm});
            skLineSegment(sketch, "E5.1.2.23", {"start": v(-31.75, 18.43) * mm, "end": v(-33.34, 15.68) * mm});
            skLineSegment(sketch, "E5.1.3.0", {"start": v(-30.1, 2.67) * mm, "end": v(-26.93, 2.67) * mm});
            skLineSegment(sketch, "E5.1.3.1", {"start": v(-33.34, 0.88) * mm, "end": v(-36.51, 0.88) * mm});
            skLineSegment(sketch, "E5.1.3.2", {"start": v(-31.75, -3.78) * mm, "end": v(-33.34, -6.53) * mm});
            skLineSegment(sketch, "E5.1.3.3", {"start": v(-26.93, 2.67) * mm, "end": v(-25.34, -0.08) * mm});
            skLineSegment(sketch, "E5.1.3.4", {"start": v(-31.69, 7.33) * mm, "end": v(-30.1, 10.08) * mm});
            skLineSegment(sketch, "E5.1.3.5", {"start": v(-38.1, 3.63) * mm, "end": v(-36.51, 6.38) * mm});
            skLineSegment(sketch, "E5.1.3.6", {"start": v(-26.93, 10.08) * mm, "end": v(-25.34, 7.33) * mm});
            skLineSegment(sketch, "E5.1.3.7", {"start": v(-26.93, -2.83) * mm, "end": v(-30.1, -2.83) * mm});
            skLineSegment(sketch, "E5.1.3.8", {"start": v(-25.34, 7.33) * mm, "end": v(-26.93, 4.58) * mm});
            skLineSegment(sketch, "E5.1.3.9", {"start": v(-38.1, -3.78) * mm, "end": v(-36.51, -1.03) * mm});
            skLineSegment(sketch, "E5.1.3.10", {"start": v(-33.34, 6.38) * mm, "end": v(-31.75, 3.63) * mm});
            skLineSegment(sketch, "E5.1.3.11", {"start": v(-31.69, -0.08) * mm, "end": v(-30.1, 2.67) * mm});
            skLineSegment(sketch, "E5.1.3.12", {"start": v(-30.1, 4.58) * mm, "end": v(-31.69, 7.33) * mm});
            skLineSegment(sketch, "E5.1.3.13", {"start": v(-33.34, -1.03) * mm, "end": v(-31.75, -3.78) * mm});
            skLineSegment(sketch, "E5.1.3.14", {"start": v(-30.1, 10.08) * mm, "end": v(-26.93, 10.08) * mm});
            skLineSegment(sketch, "E5.1.3.15", {"start": v(-33.34, -6.53) * mm, "end": v(-36.51, -6.53) * mm});
            skLineSegment(sketch, "E5.1.3.16", {"start": v(-36.51, 0.88) * mm, "end": v(-38.1, 3.63) * mm});
            skLineSegment(sketch, "E5.1.3.17", {"start": v(-25.34, -0.08) * mm, "end": v(-26.93, -2.83) * mm});
            skLineSegment(sketch, "E5.1.3.18", {"start": v(-36.51, -6.53) * mm, "end": v(-38.1, -3.78) * mm});
            skLineSegment(sketch, "E5.1.3.19", {"start": v(-36.51, 6.38) * mm, "end": v(-33.34, 6.38) * mm});
            skLineSegment(sketch, "E5.1.3.20", {"start": v(-30.1, -2.83) * mm, "end": v(-31.69, -0.08) * mm});
            skLineSegment(sketch, "E5.1.3.21", {"start": v(-26.93, 4.58) * mm, "end": v(-30.1, 4.58) * mm});
            skLineSegment(sketch, "E5.1.3.22", {"start": v(-36.51, -1.03) * mm, "end": v(-33.34, -1.03) * mm});
            skLineSegment(sketch, "E5.1.3.23", {"start": v(-31.75, 3.63) * mm, "end": v(-33.34, 0.88) * mm});
            skLineSegment(sketch, "E5.1.4.0", {"start": v(-30.1, -12.13) * mm, "end": v(-26.93, -12.13) * mm});
            skLineSegment(sketch, "E5.1.4.1", {"start": v(-33.34, -13.93) * mm, "end": v(-36.51, -13.93) * mm});
            skLineSegment(sketch, "E5.1.4.2", {"start": v(-31.75, -18.59) * mm, "end": v(-33.34, -21.34) * mm});
            skLineSegment(sketch, "E5.1.4.3", {"start": v(-26.93, -12.13) * mm, "end": v(-25.34, -14.88) * mm});
            skLineSegment(sketch, "E5.1.4.4", {"start": v(-31.69, -7.48) * mm, "end": v(-30.1, -4.73) * mm});
            skLineSegment(sketch, "E5.1.4.5", {"start": v(-38.1, -11.18) * mm, "end": v(-36.51, -8.43) * mm});
            skLineSegment(sketch, "E5.1.4.6", {"start": v(-26.93, -4.73) * mm, "end": v(-25.34, -7.48) * mm});
            skLineSegment(sketch, "E5.1.4.7", {"start": v(-26.93, -17.63) * mm, "end": v(-30.1, -17.63) * mm});
            skLineSegment(sketch, "E5.1.4.8", {"start": v(-25.34, -7.48) * mm, "end": v(-26.93, -10.23) * mm});
            skLineSegment(sketch, "E5.1.4.9", {"start": v(-38.1, -18.59) * mm, "end": v(-36.51, -15.84) * mm});
            skLineSegment(sketch, "E5.1.4.10", {"start": v(-33.34, -8.43) * mm, "end": v(-31.75, -11.18) * mm});
            skLineSegment(sketch, "E5.1.4.11", {"start": v(-31.69, -14.88) * mm, "end": v(-30.1, -12.13) * mm});
            skLineSegment(sketch, "E5.1.4.12", {"start": v(-30.1, -10.23) * mm, "end": v(-31.69, -7.48) * mm});
            skLineSegment(sketch, "E5.1.4.13", {"start": v(-33.34, -15.84) * mm, "end": v(-31.75, -18.59) * mm});
            skLineSegment(sketch, "E5.1.4.14", {"start": v(-30.1, -4.73) * mm, "end": v(-26.93, -4.73) * mm});
            skLineSegment(sketch, "E5.1.4.15", {"start": v(-33.34, -21.34) * mm, "end": v(-36.51, -21.34) * mm});
            skLineSegment(sketch, "E5.1.4.16", {"start": v(-36.51, -13.93) * mm, "end": v(-38.1, -11.18) * mm});
            skLineSegment(sketch, "E5.1.4.17", {"start": v(-25.34, -14.88) * mm, "end": v(-26.93, -17.63) * mm});
            skLineSegment(sketch, "E5.1.4.18", {"start": v(-36.51, -21.34) * mm, "end": v(-38.1, -18.59) * mm});
            skLineSegment(sketch, "E5.1.4.19", {"start": v(-36.51, -8.43) * mm, "end": v(-33.34, -8.43) * mm});
            skLineSegment(sketch, "E5.1.4.20", {"start": v(-30.1, -17.63) * mm, "end": v(-31.69, -14.88) * mm});
            skLineSegment(sketch, "E5.1.4.21", {"start": v(-26.93, -10.23) * mm, "end": v(-30.1, -10.23) * mm});
            skLineSegment(sketch, "E5.1.4.22", {"start": v(-36.51, -15.84) * mm, "end": v(-33.34, -15.84) * mm});
            skLineSegment(sketch, "E5.1.4.23", {"start": v(-31.75, -11.18) * mm, "end": v(-33.34, -13.93) * mm});
            skLineSegment(sketch, "E5.1.5.0", {"start": v(-30.1, -26.94) * mm, "end": v(-26.93, -26.94) * mm});
            skLineSegment(sketch, "E5.1.5.1", {"start": v(-33.34, -28.74) * mm, "end": v(-36.51, -28.74) * mm});
            skLineSegment(sketch, "E5.1.5.2", {"start": v(-31.75, -33.4) * mm, "end": v(-33.34, -36.14) * mm});
            skLineSegment(sketch, "E5.1.5.3", {"start": v(-26.93, -26.94) * mm, "end": v(-25.34, -29.7) * mm});
            skLineSegment(sketch, "E5.1.5.4", {"start": v(-31.69, -22.29) * mm, "end": v(-30.1, -19.54) * mm});
            skLineSegment(sketch, "E5.1.5.5", {"start": v(-38.1, -26) * mm, "end": v(-36.51, -23.24) * mm});
            skLineSegment(sketch, "E5.1.5.6", {"start": v(-26.93, -19.54) * mm, "end": v(-25.34, -22.29) * mm});
            skLineSegment(sketch, "E5.1.5.7", {"start": v(-26.93, -32.44) * mm, "end": v(-30.1, -32.44) * mm});
            skLineSegment(sketch, "E5.1.5.8", {"start": v(-25.34, -22.29) * mm, "end": v(-26.93, -25.04) * mm});
            skLineSegment(sketch, "E5.1.5.9", {"start": v(-38.1, -33.4) * mm, "end": v(-36.51, -30.65) * mm});
            skLineSegment(sketch, "E5.1.5.10", {"start": v(-33.34, -23.24) * mm, "end": v(-31.75, -26) * mm});
            skLineSegment(sketch, "E5.1.5.11", {"start": v(-31.69, -29.7) * mm, "end": v(-30.1, -26.94) * mm});
            skLineSegment(sketch, "E5.1.5.12", {"start": v(-30.1, -25.04) * mm, "end": v(-31.69, -22.29) * mm});
            skLineSegment(sketch, "E5.1.5.13", {"start": v(-33.34, -30.65) * mm, "end": v(-31.75, -33.4) * mm});
            skLineSegment(sketch, "E5.1.5.14", {"start": v(-30.1, -19.54) * mm, "end": v(-26.93, -19.54) * mm});
            skLineSegment(sketch, "E5.1.5.15", {"start": v(-33.34, -36.14) * mm, "end": v(-36.51, -36.14) * mm});
            skLineSegment(sketch, "E5.1.5.16", {"start": v(-36.51, -28.74) * mm, "end": v(-38.1, -26) * mm});
            skLineSegment(sketch, "E5.1.5.17", {"start": v(-25.34, -29.7) * mm, "end": v(-26.93, -32.44) * mm});
            skLineSegment(sketch, "E5.1.5.18", {"start": v(-36.51, -36.14) * mm, "end": v(-38.1, -33.4) * mm});
            skLineSegment(sketch, "E5.1.5.19", {"start": v(-36.51, -23.24) * mm, "end": v(-33.34, -23.24) * mm});
            skLineSegment(sketch, "E5.1.5.20", {"start": v(-30.1, -32.44) * mm, "end": v(-31.69, -29.7) * mm});
            skLineSegment(sketch, "E5.1.5.21", {"start": v(-26.93, -25.04) * mm, "end": v(-30.1, -25.04) * mm});
            skLineSegment(sketch, "E5.1.5.22", {"start": v(-36.51, -30.65) * mm, "end": v(-33.34, -30.65) * mm});
            skLineSegment(sketch, "E5.1.5.23", {"start": v(-31.75, -26) * mm, "end": v(-33.34, -28.74) * mm});
            skLineSegment(sketch, "E5.1.6.0", {"start": v(-30.1, -41.75) * mm, "end": v(-26.93, -41.75) * mm});
            skLineSegment(sketch, "E5.1.6.1", {"start": v(-33.34, -43.55) * mm, "end": v(-36.51, -43.55) * mm});
            skLineSegment(sketch, "E5.1.6.2", {"start": v(-31.75, -48.2) * mm, "end": v(-33.34, -50.95) * mm});
            skLineSegment(sketch, "E5.1.6.3", {"start": v(-26.93, -41.75) * mm, "end": v(-25.34, -44.5) * mm});
            skLineSegment(sketch, "E5.1.6.4", {"start": v(-31.69, -37.1) * mm, "end": v(-30.1, -34.35) * mm});
            skLineSegment(sketch, "E5.1.6.5", {"start": v(-38.1, -40.8) * mm, "end": v(-36.51, -38.05) * mm});
            skLineSegment(sketch, "E5.1.6.6", {"start": v(-26.93, -34.35) * mm, "end": v(-25.34, -37.1) * mm});
            skLineSegment(sketch, "E5.1.6.7", {"start": v(-26.93, -47.25) * mm, "end": v(-30.1, -47.25) * mm});
            skLineSegment(sketch, "E5.1.6.8", {"start": v(-25.34, -37.1) * mm, "end": v(-26.93, -39.85) * mm});
            skLineSegment(sketch, "E5.1.6.9", {"start": v(-38.1, -48.2) * mm, "end": v(-36.51, -45.45) * mm});
            skLineSegment(sketch, "E5.1.6.10", {"start": v(-33.34, -38.05) * mm, "end": v(-31.75, -40.8) * mm});
            skLineSegment(sketch, "E5.1.6.11", {"start": v(-31.69, -44.5) * mm, "end": v(-30.1, -41.75) * mm});
            skLineSegment(sketch, "E5.1.6.12", {"start": v(-30.1, -39.85) * mm, "end": v(-31.69, -37.1) * mm});
            skLineSegment(sketch, "E5.1.6.13", {"start": v(-33.34, -45.45) * mm, "end": v(-31.75, -48.2) * mm});
            skLineSegment(sketch, "E5.1.6.14", {"start": v(-30.1, -34.35) * mm, "end": v(-26.93, -34.35) * mm});
            skLineSegment(sketch, "E5.1.6.15", {"start": v(-33.34, -50.95) * mm, "end": v(-36.51, -50.95) * mm});
            skLineSegment(sketch, "E5.1.6.16", {"start": v(-36.51, -43.55) * mm, "end": v(-38.1, -40.8) * mm});
            skLineSegment(sketch, "E5.1.6.17", {"start": v(-25.34, -44.5) * mm, "end": v(-26.93, -47.25) * mm});
            skLineSegment(sketch, "E5.1.6.18", {"start": v(-36.51, -50.95) * mm, "end": v(-38.1, -48.2) * mm});
            skLineSegment(sketch, "E5.1.6.19", {"start": v(-36.51, -38.05) * mm, "end": v(-33.34, -38.05) * mm});
            skLineSegment(sketch, "E5.1.6.20", {"start": v(-30.1, -47.25) * mm, "end": v(-31.69, -44.5) * mm});
            skLineSegment(sketch, "E5.1.6.21", {"start": v(-26.93, -39.85) * mm, "end": v(-30.1, -39.85) * mm});
            skLineSegment(sketch, "E5.1.6.22", {"start": v(-36.51, -45.45) * mm, "end": v(-33.34, -45.45) * mm});
            skLineSegment(sketch, "E5.1.6.23", {"start": v(-31.75, -40.8) * mm, "end": v(-33.34, -43.55) * mm});
            skLineSegment(sketch, "E5.2.0.0", {"start": v(-17.4, 47.1) * mm, "end": v(-14.23, 47.1) * mm});
            skLineSegment(sketch, "E5.2.0.1", {"start": v(-20.64, 45.3) * mm, "end": v(-23.81, 45.3) * mm});
            skLineSegment(sketch, "E5.2.0.2", {"start": v(-19.05, 40.65) * mm, "end": v(-20.64, 37.9) * mm});
            skLineSegment(sketch, "E5.2.0.3", {"start": v(-14.23, 47.1) * mm, "end": v(-12.64, 44.35) * mm});
            skLineSegment(sketch, "E5.2.0.4", {"start": v(-18.99, 51.75) * mm, "end": v(-17.4, 54.5) * mm});
            skLineSegment(sketch, "E5.2.0.5", {"start": v(-25.4, 48.05) * mm, "end": v(-23.81, 50.8) * mm});
            skLineSegment(sketch, "E5.2.0.6", {"start": v(-14.23, 54.5) * mm, "end": v(-12.64, 51.75) * mm});
            skLineSegment(sketch, "E5.2.0.7", {"start": v(-14.23, 41.6) * mm, "end": v(-17.4, 41.6) * mm});
            skLineSegment(sketch, "E5.2.0.8", {"start": v(-12.64, 51.75) * mm, "end": v(-14.23, 49) * mm});
            skLineSegment(sketch, "E5.2.0.9", {"start": v(-25.4, 40.65) * mm, "end": v(-23.81, 43.4) * mm});
            skLineSegment(sketch, "E5.2.0.10", {"start": v(-20.64, 50.8) * mm, "end": v(-19.05, 48.05) * mm});
            skLineSegment(sketch, "E5.2.0.11", {"start": v(-18.99, 44.35) * mm, "end": v(-17.4, 47.1) * mm});
            skLineSegment(sketch, "E5.2.0.12", {"start": v(-17.4, 49) * mm, "end": v(-18.99, 51.75) * mm});
            skLineSegment(sketch, "E5.2.0.13", {"start": v(-20.64, 43.4) * mm, "end": v(-19.05, 40.65) * mm});
            skLineSegment(sketch, "E5.2.0.14", {"start": v(-17.4, 54.5) * mm, "end": v(-14.23, 54.5) * mm});
            skLineSegment(sketch, "E5.2.0.15", {"start": v(-20.64, 37.9) * mm, "end": v(-23.81, 37.9) * mm});
            skLineSegment(sketch, "E5.2.0.16", {"start": v(-23.81, 45.3) * mm, "end": v(-25.4, 48.05) * mm});
            skLineSegment(sketch, "E5.2.0.17", {"start": v(-12.64, 44.35) * mm, "end": v(-14.23, 41.6) * mm});
            skLineSegment(sketch, "E5.2.0.18", {"start": v(-23.81, 37.9) * mm, "end": v(-25.4, 40.65) * mm});
            skLineSegment(sketch, "E5.2.0.19", {"start": v(-23.81, 50.8) * mm, "end": v(-20.64, 50.8) * mm});
            skLineSegment(sketch, "E5.2.0.20", {"start": v(-17.4, 41.6) * mm, "end": v(-18.99, 44.35) * mm});
            skLineSegment(sketch, "E5.2.0.21", {"start": v(-14.23, 49) * mm, "end": v(-17.4, 49) * mm});
            skLineSegment(sketch, "E5.2.0.22", {"start": v(-23.81, 43.4) * mm, "end": v(-20.64, 43.4) * mm});
            skLineSegment(sketch, "E5.2.0.23", {"start": v(-19.05, 48.05) * mm, "end": v(-20.64, 45.3) * mm});
            skLineSegment(sketch, "E5.2.1.0", {"start": v(-17.4, 32.29) * mm, "end": v(-14.23, 32.29) * mm});
            skLineSegment(sketch, "E5.2.1.1", {"start": v(-20.64, 30.5) * mm, "end": v(-23.81, 30.5) * mm});
            skLineSegment(sketch, "E5.2.1.2", {"start": v(-19.05, 25.84) * mm, "end": v(-20.64, 23.09) * mm});
            skLineSegment(sketch, "E5.2.1.3", {"start": v(-14.23, 32.29) * mm, "end": v(-12.64, 29.54) * mm});
            skLineSegment(sketch, "E5.2.1.4", {"start": v(-18.99, 36.94) * mm, "end": v(-17.4, 39.7) * mm});
            skLineSegment(sketch, "E5.2.1.5", {"start": v(-25.4, 33.24) * mm, "end": v(-23.81, 36) * mm});
            skLineSegment(sketch, "E5.2.1.6", {"start": v(-14.23, 39.7) * mm, "end": v(-12.64, 36.94) * mm});
            skLineSegment(sketch, "E5.2.1.7", {"start": v(-14.23, 26.8) * mm, "end": v(-17.4, 26.8) * mm});
            skLineSegment(sketch, "E5.2.1.8", {"start": v(-12.64, 36.94) * mm, "end": v(-14.23, 34.2) * mm});
            skLineSegment(sketch, "E5.2.1.9", {"start": v(-25.4, 25.84) * mm, "end": v(-23.81, 28.59) * mm});
            skLineSegment(sketch, "E5.2.1.10", {"start": v(-20.64, 36) * mm, "end": v(-19.05, 33.24) * mm});
            skLineSegment(sketch, "E5.2.1.11", {"start": v(-18.99, 29.54) * mm, "end": v(-17.4, 32.29) * mm});
            skLineSegment(sketch, "E5.2.1.12", {"start": v(-17.4, 34.2) * mm, "end": v(-18.99, 36.94) * mm});
            skLineSegment(sketch, "E5.2.1.13", {"start": v(-20.64, 28.59) * mm, "end": v(-19.05, 25.84) * mm});
            skLineSegment(sketch, "E5.2.1.14", {"start": v(-17.4, 39.7) * mm, "end": v(-14.23, 39.7) * mm});
            skLineSegment(sketch, "E5.2.1.15", {"start": v(-20.64, 23.09) * mm, "end": v(-23.81, 23.09) * mm});
            skLineSegment(sketch, "E5.2.1.16", {"start": v(-23.81, 30.5) * mm, "end": v(-25.4, 33.24) * mm});
            skLineSegment(sketch, "E5.2.1.17", {"start": v(-12.64, 29.54) * mm, "end": v(-14.23, 26.8) * mm});
            skLineSegment(sketch, "E5.2.1.18", {"start": v(-23.81, 23.09) * mm, "end": v(-25.4, 25.84) * mm});
            skLineSegment(sketch, "E5.2.1.19", {"start": v(-23.81, 36) * mm, "end": v(-20.64, 36) * mm});
            skLineSegment(sketch, "E5.2.1.20", {"start": v(-17.4, 26.8) * mm, "end": v(-18.99, 29.54) * mm});
            skLineSegment(sketch, "E5.2.1.21", {"start": v(-14.23, 34.2) * mm, "end": v(-17.4, 34.2) * mm});
            skLineSegment(sketch, "E5.2.1.22", {"start": v(-23.81, 28.59) * mm, "end": v(-20.64, 28.59) * mm});
            skLineSegment(sketch, "E5.2.1.23", {"start": v(-19.05, 33.24) * mm, "end": v(-20.64, 30.5) * mm});
            skLineSegment(sketch, "E5.2.2.0", {"start": v(-17.4, 17.48) * mm, "end": v(-14.23, 17.48) * mm});
            skLineSegment(sketch, "E5.2.2.1", {"start": v(-20.64, 15.68) * mm, "end": v(-23.81, 15.68) * mm});
            skLineSegment(sketch, "E5.2.2.2", {"start": v(-19.05, 11.03) * mm, "end": v(-20.64, 8.28) * mm});
            skLineSegment(sketch, "E5.2.2.3", {"start": v(-14.23, 17.48) * mm, "end": v(-12.64, 14.73) * mm});
            skLineSegment(sketch, "E5.2.2.4", {"start": v(-18.99, 22.14) * mm, "end": v(-17.4, 24.89) * mm});
            skLineSegment(sketch, "E5.2.2.5", {"start": v(-25.4, 18.43) * mm, "end": v(-23.81, 21.18) * mm});
            skLineSegment(sketch, "E5.2.2.6", {"start": v(-14.23, 24.89) * mm, "end": v(-12.64, 22.14) * mm});
            skLineSegment(sketch, "E5.2.2.7", {"start": v(-14.23, 11.98) * mm, "end": v(-17.4, 11.98) * mm});
            skLineSegment(sketch, "E5.2.2.8", {"start": v(-12.64, 22.14) * mm, "end": v(-14.23, 19.39) * mm});
            skLineSegment(sketch, "E5.2.2.9", {"start": v(-25.4, 11.03) * mm, "end": v(-23.81, 13.78) * mm});
            skLineSegment(sketch, "E5.2.2.10", {"start": v(-20.64, 21.18) * mm, "end": v(-19.05, 18.43) * mm});
            skLineSegment(sketch, "E5.2.2.11", {"start": v(-18.99, 14.73) * mm, "end": v(-17.4, 17.48) * mm});
            skLineSegment(sketch, "E5.2.2.12", {"start": v(-17.4, 19.39) * mm, "end": v(-18.99, 22.14) * mm});
            skLineSegment(sketch, "E5.2.2.13", {"start": v(-20.64, 13.78) * mm, "end": v(-19.05, 11.03) * mm});
            skLineSegment(sketch, "E5.2.2.14", {"start": v(-17.4, 24.89) * mm, "end": v(-14.23, 24.89) * mm});
            skLineSegment(sketch, "E5.2.2.15", {"start": v(-20.64, 8.28) * mm, "end": v(-23.81, 8.28) * mm});
            skLineSegment(sketch, "E5.2.2.16", {"start": v(-23.81, 15.68) * mm, "end": v(-25.4, 18.43) * mm});
            skLineSegment(sketch, "E5.2.2.17", {"start": v(-12.64, 14.73) * mm, "end": v(-14.23, 11.98) * mm});
            skLineSegment(sketch, "E5.2.2.18", {"start": v(-23.81, 8.28) * mm, "end": v(-25.4, 11.03) * mm});
            skLineSegment(sketch, "E5.2.2.19", {"start": v(-23.81, 21.18) * mm, "end": v(-20.64, 21.18) * mm});
            skLineSegment(sketch, "E5.2.2.20", {"start": v(-17.4, 11.98) * mm, "end": v(-18.99, 14.73) * mm});
            skLineSegment(sketch, "E5.2.2.21", {"start": v(-14.23, 19.39) * mm, "end": v(-17.4, 19.39) * mm});
            skLineSegment(sketch, "E5.2.2.22", {"start": v(-23.81, 13.78) * mm, "end": v(-20.64, 13.78) * mm});
            skLineSegment(sketch, "E5.2.2.23", {"start": v(-19.05, 18.43) * mm, "end": v(-20.64, 15.68) * mm});
            skLineSegment(sketch, "E5.2.3.0", {"start": v(-17.4, 2.67) * mm, "end": v(-14.23, 2.67) * mm});
            skLineSegment(sketch, "E5.2.3.1", {"start": v(-20.64, 0.88) * mm, "end": v(-23.81, 0.88) * mm});
            skLineSegment(sketch, "E5.2.3.2", {"start": v(-19.05, -3.78) * mm, "end": v(-20.64, -6.53) * mm});
            skLineSegment(sketch, "E5.2.3.3", {"start": v(-14.23, 2.67) * mm, "end": v(-12.64, -0.08) * mm});
            skLineSegment(sketch, "E5.2.3.4", {"start": v(-18.99, 7.33) * mm, "end": v(-17.4, 10.08) * mm});
            skLineSegment(sketch, "E5.2.3.5", {"start": v(-25.4, 3.63) * mm, "end": v(-23.81, 6.38) * mm});
            skLineSegment(sketch, "E5.2.3.6", {"start": v(-14.23, 10.08) * mm, "end": v(-12.64, 7.33) * mm});
            skLineSegment(sketch, "E5.2.3.7", {"start": v(-14.23, -2.83) * mm, "end": v(-17.4, -2.83) * mm});
            skLineSegment(sketch, "E5.2.3.8", {"start": v(-12.64, 7.33) * mm, "end": v(-14.23, 4.58) * mm});
            skLineSegment(sketch, "E5.2.3.9", {"start": v(-25.4, -3.78) * mm, "end": v(-23.81, -1.03) * mm});
            skLineSegment(sketch, "E5.2.3.10", {"start": v(-20.64, 6.38) * mm, "end": v(-19.05, 3.63) * mm});
            skLineSegment(sketch, "E5.2.3.11", {"start": v(-18.99, -0.08) * mm, "end": v(-17.4, 2.67) * mm});
            skLineSegment(sketch, "E5.2.3.12", {"start": v(-17.4, 4.58) * mm, "end": v(-18.99, 7.33) * mm});
            skLineSegment(sketch, "E5.2.3.13", {"start": v(-20.64, -1.03) * mm, "end": v(-19.05, -3.78) * mm});
            skLineSegment(sketch, "E5.2.3.14", {"start": v(-17.4, 10.08) * mm, "end": v(-14.23, 10.08) * mm});
            skLineSegment(sketch, "E5.2.3.15", {"start": v(-20.64, -6.53) * mm, "end": v(-23.81, -6.53) * mm});
            skLineSegment(sketch, "E5.2.3.16", {"start": v(-23.81, 0.88) * mm, "end": v(-25.4, 3.63) * mm});
            skLineSegment(sketch, "E5.2.3.17", {"start": v(-12.64, -0.08) * mm, "end": v(-14.23, -2.83) * mm});
            skLineSegment(sketch, "E5.2.3.18", {"start": v(-23.81, -6.53) * mm, "end": v(-25.4, -3.78) * mm});
            skLineSegment(sketch, "E5.2.3.19", {"start": v(-23.81, 6.38) * mm, "end": v(-20.64, 6.38) * mm});
            skLineSegment(sketch, "E5.2.3.20", {"start": v(-17.4, -2.83) * mm, "end": v(-18.99, -0.08) * mm});
            skLineSegment(sketch, "E5.2.3.21", {"start": v(-14.23, 4.58) * mm, "end": v(-17.4, 4.58) * mm});
            skLineSegment(sketch, "E5.2.3.22", {"start": v(-23.81, -1.03) * mm, "end": v(-20.64, -1.03) * mm});
            skLineSegment(sketch, "E5.2.3.23", {"start": v(-19.05, 3.63) * mm, "end": v(-20.64, 0.88) * mm});
            skLineSegment(sketch, "E5.2.4.0", {"start": v(-17.4, -12.13) * mm, "end": v(-14.23, -12.13) * mm});
            skLineSegment(sketch, "E5.2.4.1", {"start": v(-20.64, -13.93) * mm, "end": v(-23.81, -13.93) * mm});
            skLineSegment(sketch, "E5.2.4.2", {"start": v(-19.05, -18.59) * mm, "end": v(-20.64, -21.34) * mm});
            skLineSegment(sketch, "E5.2.4.3", {"start": v(-14.23, -12.13) * mm, "end": v(-12.64, -14.88) * mm});
            skLineSegment(sketch, "E5.2.4.4", {"start": v(-18.99, -7.48) * mm, "end": v(-17.4, -4.73) * mm});
            skLineSegment(sketch, "E5.2.4.5", {"start": v(-25.4, -11.18) * mm, "end": v(-23.81, -8.43) * mm});
            skLineSegment(sketch, "E5.2.4.6", {"start": v(-14.23, -4.73) * mm, "end": v(-12.64, -7.48) * mm});
            skLineSegment(sketch, "E5.2.4.7", {"start": v(-14.23, -17.63) * mm, "end": v(-17.4, -17.63) * mm});
            skLineSegment(sketch, "E5.2.4.8", {"start": v(-12.64, -7.48) * mm, "end": v(-14.23, -10.23) * mm});
            skLineSegment(sketch, "E5.2.4.9", {"start": v(-25.4, -18.59) * mm, "end": v(-23.81, -15.84) * mm});
            skLineSegment(sketch, "E5.2.4.10", {"start": v(-20.64, -8.43) * mm, "end": v(-19.05, -11.18) * mm});
            skLineSegment(sketch, "E5.2.4.11", {"start": v(-18.99, -14.88) * mm, "end": v(-17.4, -12.13) * mm});
            skLineSegment(sketch, "E5.2.4.12", {"start": v(-17.4, -10.23) * mm, "end": v(-18.99, -7.48) * mm});
            skLineSegment(sketch, "E5.2.4.13", {"start": v(-20.64, -15.84) * mm, "end": v(-19.05, -18.59) * mm});
            skLineSegment(sketch, "E5.2.4.14", {"start": v(-17.4, -4.73) * mm, "end": v(-14.23, -4.73) * mm});
            skLineSegment(sketch, "E5.2.4.15", {"start": v(-20.64, -21.34) * mm, "end": v(-23.81, -21.34) * mm});
            skLineSegment(sketch, "E5.2.4.16", {"start": v(-23.81, -13.93) * mm, "end": v(-25.4, -11.18) * mm});
            skLineSegment(sketch, "E5.2.4.17", {"start": v(-12.64, -14.88) * mm, "end": v(-14.23, -17.63) * mm});
            skLineSegment(sketch, "E5.2.4.18", {"start": v(-23.81, -21.34) * mm, "end": v(-25.4, -18.59) * mm});
            skLineSegment(sketch, "E5.2.4.19", {"start": v(-23.81, -8.43) * mm, "end": v(-20.64, -8.43) * mm});
            skLineSegment(sketch, "E5.2.4.20", {"start": v(-17.4, -17.63) * mm, "end": v(-18.99, -14.88) * mm});
            skLineSegment(sketch, "E5.2.4.21", {"start": v(-14.23, -10.23) * mm, "end": v(-17.4, -10.23) * mm});
            skLineSegment(sketch, "E5.2.4.22", {"start": v(-23.81, -15.84) * mm, "end": v(-20.64, -15.84) * mm});
            skLineSegment(sketch, "E5.2.4.23", {"start": v(-19.05, -11.18) * mm, "end": v(-20.64, -13.93) * mm});
            skLineSegment(sketch, "E5.2.5.0", {"start": v(-17.4, -26.94) * mm, "end": v(-14.23, -26.94) * mm});
            skLineSegment(sketch, "E5.2.5.1", {"start": v(-20.64, -28.74) * mm, "end": v(-23.81, -28.74) * mm});
            skLineSegment(sketch, "E5.2.5.2", {"start": v(-19.05, -33.4) * mm, "end": v(-20.64, -36.14) * mm});
            skLineSegment(sketch, "E5.2.5.3", {"start": v(-14.23, -26.94) * mm, "end": v(-12.64, -29.7) * mm});
            skLineSegment(sketch, "E5.2.5.4", {"start": v(-18.99, -22.29) * mm, "end": v(-17.4, -19.54) * mm});
            skLineSegment(sketch, "E5.2.5.5", {"start": v(-25.4, -26) * mm, "end": v(-23.81, -23.24) * mm});
            skLineSegment(sketch, "E5.2.5.6", {"start": v(-14.23, -19.54) * mm, "end": v(-12.64, -22.29) * mm});
            skLineSegment(sketch, "E5.2.5.7", {"start": v(-14.23, -32.44) * mm, "end": v(-17.4, -32.44) * mm});
            skLineSegment(sketch, "E5.2.5.8", {"start": v(-12.64, -22.29) * mm, "end": v(-14.23, -25.04) * mm});
            skLineSegment(sketch, "E5.2.5.9", {"start": v(-25.4, -33.4) * mm, "end": v(-23.81, -30.65) * mm});
            skLineSegment(sketch, "E5.2.5.10", {"start": v(-20.64, -23.24) * mm, "end": v(-19.05, -26) * mm});
            skLineSegment(sketch, "E5.2.5.11", {"start": v(-18.99, -29.7) * mm, "end": v(-17.4, -26.94) * mm});
            skLineSegment(sketch, "E5.2.5.12", {"start": v(-17.4, -25.04) * mm, "end": v(-18.99, -22.29) * mm});
            skLineSegment(sketch, "E5.2.5.13", {"start": v(-20.64, -30.65) * mm, "end": v(-19.05, -33.4) * mm});
            skLineSegment(sketch, "E5.2.5.14", {"start": v(-17.4, -19.54) * mm, "end": v(-14.23, -19.54) * mm});
            skLineSegment(sketch, "E5.2.5.15", {"start": v(-20.64, -36.14) * mm, "end": v(-23.81, -36.14) * mm});
            skLineSegment(sketch, "E5.2.5.16", {"start": v(-23.81, -28.74) * mm, "end": v(-25.4, -26) * mm});
            skLineSegment(sketch, "E5.2.5.17", {"start": v(-12.64, -29.7) * mm, "end": v(-14.23, -32.44) * mm});
            skLineSegment(sketch, "E5.2.5.18", {"start": v(-23.81, -36.14) * mm, "end": v(-25.4, -33.4) * mm});
            skLineSegment(sketch, "E5.2.5.19", {"start": v(-23.81, -23.24) * mm, "end": v(-20.64, -23.24) * mm});
            skLineSegment(sketch, "E5.2.5.20", {"start": v(-17.4, -32.44) * mm, "end": v(-18.99, -29.7) * mm});
            skLineSegment(sketch, "E5.2.5.21", {"start": v(-14.23, -25.04) * mm, "end": v(-17.4, -25.04) * mm});
            skLineSegment(sketch, "E5.2.5.22", {"start": v(-23.81, -30.65) * mm, "end": v(-20.64, -30.65) * mm});
            skLineSegment(sketch, "E5.2.5.23", {"start": v(-19.05, -26) * mm, "end": v(-20.64, -28.74) * mm});
            skLineSegment(sketch, "E5.2.6.0", {"start": v(-17.4, -41.75) * mm, "end": v(-14.23, -41.75) * mm});
            skLineSegment(sketch, "E5.2.6.1", {"start": v(-20.64, -43.55) * mm, "end": v(-23.81, -43.55) * mm});
            skLineSegment(sketch, "E5.2.6.2", {"start": v(-19.05, -48.2) * mm, "end": v(-20.64, -50.95) * mm});
            skLineSegment(sketch, "E5.2.6.3", {"start": v(-14.23, -41.75) * mm, "end": v(-12.64, -44.5) * mm});
            skLineSegment(sketch, "E5.2.6.4", {"start": v(-18.99, -37.1) * mm, "end": v(-17.4, -34.35) * mm});
            skLineSegment(sketch, "E5.2.6.5", {"start": v(-25.4, -40.8) * mm, "end": v(-23.81, -38.05) * mm});
            skLineSegment(sketch, "E5.2.6.6", {"start": v(-14.23, -34.35) * mm, "end": v(-12.64, -37.1) * mm});
            skLineSegment(sketch, "E5.2.6.7", {"start": v(-14.23, -47.25) * mm, "end": v(-17.4, -47.25) * mm});
            skLineSegment(sketch, "E5.2.6.8", {"start": v(-12.64, -37.1) * mm, "end": v(-14.23, -39.85) * mm});
            skLineSegment(sketch, "E5.2.6.9", {"start": v(-25.4, -48.2) * mm, "end": v(-23.81, -45.45) * mm});
            skLineSegment(sketch, "E5.2.6.10", {"start": v(-20.64, -38.05) * mm, "end": v(-19.05, -40.8) * mm});
            skLineSegment(sketch, "E5.2.6.11", {"start": v(-18.99, -44.5) * mm, "end": v(-17.4, -41.75) * mm});
            skLineSegment(sketch, "E5.2.6.12", {"start": v(-17.4, -39.85) * mm, "end": v(-18.99, -37.1) * mm});
            skLineSegment(sketch, "E5.2.6.13", {"start": v(-20.64, -45.45) * mm, "end": v(-19.05, -48.2) * mm});
            skLineSegment(sketch, "E5.2.6.14", {"start": v(-17.4, -34.35) * mm, "end": v(-14.23, -34.35) * mm});
            skLineSegment(sketch, "E5.2.6.15", {"start": v(-20.64, -50.95) * mm, "end": v(-23.81, -50.95) * mm});
            skLineSegment(sketch, "E5.2.6.16", {"start": v(-23.81, -43.55) * mm, "end": v(-25.4, -40.8) * mm});
            skLineSegment(sketch, "E5.2.6.17", {"start": v(-12.64, -44.5) * mm, "end": v(-14.23, -47.25) * mm});
            skLineSegment(sketch, "E5.2.6.18", {"start": v(-23.81, -50.95) * mm, "end": v(-25.4, -48.2) * mm});
            skLineSegment(sketch, "E5.2.6.19", {"start": v(-23.81, -38.05) * mm, "end": v(-20.64, -38.05) * mm});
            skLineSegment(sketch, "E5.2.6.20", {"start": v(-17.4, -47.25) * mm, "end": v(-18.99, -44.5) * mm});
            skLineSegment(sketch, "E5.2.6.21", {"start": v(-14.23, -39.85) * mm, "end": v(-17.4, -39.85) * mm});
            skLineSegment(sketch, "E5.2.6.22", {"start": v(-23.81, -45.45) * mm, "end": v(-20.64, -45.45) * mm});
            skLineSegment(sketch, "E5.2.6.23", {"start": v(-19.05, -40.8) * mm, "end": v(-20.64, -43.55) * mm});
            skLineSegment(sketch, "E5.3.0.0", {"start": v(-4.7, 47.1) * mm, "end": v(-1.53, 47.1) * mm});
            skLineSegment(sketch, "E5.3.0.1", {"start": v(-7.94, 45.3) * mm, "end": v(-11.11, 45.3) * mm});
            skLineSegment(sketch, "E5.3.0.2", {"start": v(-6.35, 40.65) * mm, "end": v(-7.94, 37.9) * mm});
            skLineSegment(sketch, "E5.3.0.3", {"start": v(-1.53, 47.1) * mm, "end": v(0.06, 44.35) * mm});
            skLineSegment(sketch, "E5.3.0.4", {"start": v(-6.29, 51.75) * mm, "end": v(-4.7, 54.5) * mm});
            skLineSegment(sketch, "E5.3.0.5", {"start": v(-12.7, 48.05) * mm, "end": v(-11.11, 50.8) * mm});
            skLineSegment(sketch, "E5.3.0.6", {"start": v(-1.53, 54.5) * mm, "end": v(0.06, 51.75) * mm});
            skLineSegment(sketch, "E5.3.0.7", {"start": v(-1.53, 41.6) * mm, "end": v(-4.7, 41.6) * mm});
            skLineSegment(sketch, "E5.3.0.8", {"start": v(0.06, 51.75) * mm, "end": v(-1.53, 49) * mm});
            skLineSegment(sketch, "E5.3.0.9", {"start": v(-12.7, 40.65) * mm, "end": v(-11.11, 43.4) * mm});
            skLineSegment(sketch, "E5.3.0.10", {"start": v(-7.94, 50.8) * mm, "end": v(-6.35, 48.05) * mm});
            skLineSegment(sketch, "E5.3.0.11", {"start": v(-6.29, 44.35) * mm, "end": v(-4.7, 47.1) * mm});
            skLineSegment(sketch, "E5.3.0.12", {"start": v(-4.7, 49) * mm, "end": v(-6.29, 51.75) * mm});
            skLineSegment(sketch, "E5.3.0.13", {"start": v(-7.94, 43.4) * mm, "end": v(-6.35, 40.65) * mm});
            skLineSegment(sketch, "E5.3.0.14", {"start": v(-4.7, 54.5) * mm, "end": v(-1.53, 54.5) * mm});
            skLineSegment(sketch, "E5.3.0.15", {"start": v(-7.94, 37.9) * mm, "end": v(-11.11, 37.9) * mm});
            skLineSegment(sketch, "E5.3.0.16", {"start": v(-11.11, 45.3) * mm, "end": v(-12.7, 48.05) * mm});
            skLineSegment(sketch, "E5.3.0.17", {"start": v(0.06, 44.35) * mm, "end": v(-1.53, 41.6) * mm});
            skLineSegment(sketch, "E5.3.0.18", {"start": v(-11.11, 37.9) * mm, "end": v(-12.7, 40.65) * mm});
            skLineSegment(sketch, "E5.3.0.19", {"start": v(-11.11, 50.8) * mm, "end": v(-7.94, 50.8) * mm});
            skLineSegment(sketch, "E5.3.0.20", {"start": v(-4.7, 41.6) * mm, "end": v(-6.29, 44.35) * mm});
            skLineSegment(sketch, "E5.3.0.21", {"start": v(-1.53, 49) * mm, "end": v(-4.7, 49) * mm});
            skLineSegment(sketch, "E5.3.0.22", {"start": v(-11.11, 43.4) * mm, "end": v(-7.94, 43.4) * mm});
            skLineSegment(sketch, "E5.3.0.23", {"start": v(-6.35, 48.05) * mm, "end": v(-7.94, 45.3) * mm});
            skLineSegment(sketch, "E5.3.1.0", {"start": v(-4.7, 32.29) * mm, "end": v(-1.53, 32.29) * mm});
            skLineSegment(sketch, "E5.3.1.1", {"start": v(-7.94, 30.5) * mm, "end": v(-11.11, 30.5) * mm});
            skLineSegment(sketch, "E5.3.1.2", {"start": v(-6.35, 25.84) * mm, "end": v(-7.94, 23.09) * mm});
            skLineSegment(sketch, "E5.3.1.3", {"start": v(-1.53, 32.29) * mm, "end": v(0.06, 29.54) * mm});
            skLineSegment(sketch, "E5.3.1.4", {"start": v(-6.29, 36.94) * mm, "end": v(-4.7, 39.7) * mm});
            skLineSegment(sketch, "E5.3.1.5", {"start": v(-12.7, 33.24) * mm, "end": v(-11.11, 36) * mm});
            skLineSegment(sketch, "E5.3.1.6", {"start": v(-1.53, 39.7) * mm, "end": v(0.06, 36.94) * mm});
            skLineSegment(sketch, "E5.3.1.7", {"start": v(-1.53, 26.8) * mm, "end": v(-4.7, 26.8) * mm});
            skLineSegment(sketch, "E5.3.1.8", {"start": v(0.06, 36.94) * mm, "end": v(-1.53, 34.2) * mm});
            skLineSegment(sketch, "E5.3.1.9", {"start": v(-12.7, 25.84) * mm, "end": v(-11.11, 28.59) * mm});
            skLineSegment(sketch, "E5.3.1.10", {"start": v(-7.94, 36) * mm, "end": v(-6.35, 33.24) * mm});
            skLineSegment(sketch, "E5.3.1.11", {"start": v(-6.29, 29.54) * mm, "end": v(-4.7, 32.29) * mm});
            skLineSegment(sketch, "E5.3.1.12", {"start": v(-4.7, 34.2) * mm, "end": v(-6.29, 36.94) * mm});
            skLineSegment(sketch, "E5.3.1.13", {"start": v(-7.94, 28.59) * mm, "end": v(-6.35, 25.84) * mm});
            skLineSegment(sketch, "E5.3.1.14", {"start": v(-4.7, 39.7) * mm, "end": v(-1.53, 39.7) * mm});
            skLineSegment(sketch, "E5.3.1.15", {"start": v(-7.94, 23.09) * mm, "end": v(-11.11, 23.09) * mm});
            skLineSegment(sketch, "E5.3.1.16", {"start": v(-11.11, 30.5) * mm, "end": v(-12.7, 33.24) * mm});
            skLineSegment(sketch, "E5.3.1.17", {"start": v(0.06, 29.54) * mm, "end": v(-1.53, 26.8) * mm});
            skLineSegment(sketch, "E5.3.1.18", {"start": v(-11.11, 23.09) * mm, "end": v(-12.7, 25.84) * mm});
            skLineSegment(sketch, "E5.3.1.19", {"start": v(-11.11, 36) * mm, "end": v(-7.94, 36) * mm});
            skLineSegment(sketch, "E5.3.1.20", {"start": v(-4.7, 26.8) * mm, "end": v(-6.29, 29.54) * mm});
            skLineSegment(sketch, "E5.3.1.21", {"start": v(-1.53, 34.2) * mm, "end": v(-4.7, 34.2) * mm});
            skLineSegment(sketch, "E5.3.1.22", {"start": v(-11.11, 28.59) * mm, "end": v(-7.94, 28.59) * mm});
            skLineSegment(sketch, "E5.3.1.23", {"start": v(-6.35, 33.24) * mm, "end": v(-7.94, 30.5) * mm});
            skLineSegment(sketch, "E5.3.2.0", {"start": v(-4.7, 17.48) * mm, "end": v(-1.53, 17.48) * mm});
            skLineSegment(sketch, "E5.3.2.1", {"start": v(-7.94, 15.68) * mm, "end": v(-11.11, 15.68) * mm});
            skLineSegment(sketch, "E5.3.2.2", {"start": v(-6.35, 11.03) * mm, "end": v(-7.94, 8.28) * mm});
            skLineSegment(sketch, "E5.3.2.3", {"start": v(-1.53, 17.48) * mm, "end": v(0.06, 14.73) * mm});
            skLineSegment(sketch, "E5.3.2.4", {"start": v(-6.29, 22.14) * mm, "end": v(-4.7, 24.89) * mm});
            skLineSegment(sketch, "E5.3.2.5", {"start": v(-12.7, 18.43) * mm, "end": v(-11.11, 21.18) * mm});
            skLineSegment(sketch, "E5.3.2.6", {"start": v(-1.53, 24.89) * mm, "end": v(0.06, 22.14) * mm});
            skLineSegment(sketch, "E5.3.2.7", {"start": v(-1.53, 11.98) * mm, "end": v(-4.7, 11.98) * mm});
            skLineSegment(sketch, "E5.3.2.8", {"start": v(0.06, 22.14) * mm, "end": v(-1.53, 19.39) * mm});
            skLineSegment(sketch, "E5.3.2.9", {"start": v(-12.7, 11.03) * mm, "end": v(-11.11, 13.78) * mm});
            skLineSegment(sketch, "E5.3.2.10", {"start": v(-7.94, 21.18) * mm, "end": v(-6.35, 18.43) * mm});
            skLineSegment(sketch, "E5.3.2.11", {"start": v(-6.29, 14.73) * mm, "end": v(-4.7, 17.48) * mm});
            skLineSegment(sketch, "E5.3.2.12", {"start": v(-4.7, 19.39) * mm, "end": v(-6.29, 22.14) * mm});
            skLineSegment(sketch, "E5.3.2.13", {"start": v(-7.94, 13.78) * mm, "end": v(-6.35, 11.03) * mm});
            skLineSegment(sketch, "E5.3.2.14", {"start": v(-4.7, 24.89) * mm, "end": v(-1.53, 24.89) * mm});
            skLineSegment(sketch, "E5.3.2.15", {"start": v(-7.94, 8.28) * mm, "end": v(-11.11, 8.28) * mm});
            skLineSegment(sketch, "E5.3.2.16", {"start": v(-11.11, 15.68) * mm, "end": v(-12.7, 18.43) * mm});
            skLineSegment(sketch, "E5.3.2.17", {"start": v(0.06, 14.73) * mm, "end": v(-1.53, 11.98) * mm});
            skLineSegment(sketch, "E5.3.2.18", {"start": v(-11.11, 8.28) * mm, "end": v(-12.7, 11.03) * mm});
            skLineSegment(sketch, "E5.3.2.19", {"start": v(-11.11, 21.18) * mm, "end": v(-7.94, 21.18) * mm});
            skLineSegment(sketch, "E5.3.2.20", {"start": v(-4.7, 11.98) * mm, "end": v(-6.29, 14.73) * mm});
            skLineSegment(sketch, "E5.3.2.21", {"start": v(-1.53, 19.39) * mm, "end": v(-4.7, 19.39) * mm});
            skLineSegment(sketch, "E5.3.2.22", {"start": v(-11.11, 13.78) * mm, "end": v(-7.94, 13.78) * mm});
            skLineSegment(sketch, "E5.3.2.23", {"start": v(-6.35, 18.43) * mm, "end": v(-7.94, 15.68) * mm});
            skLineSegment(sketch, "E5.3.3.0", {"start": v(-4.7, 2.67) * mm, "end": v(-1.53, 2.67) * mm});
            skLineSegment(sketch, "E5.3.3.1", {"start": v(-7.94, 0.88) * mm, "end": v(-11.11, 0.88) * mm});
            skLineSegment(sketch, "E5.3.3.2", {"start": v(-6.35, -3.78) * mm, "end": v(-7.94, -6.53) * mm});
            skLineSegment(sketch, "E5.3.3.3", {"start": v(-1.53, 2.67) * mm, "end": v(0.06, -0.08) * mm});
            skLineSegment(sketch, "E5.3.3.4", {"start": v(-6.29, 7.33) * mm, "end": v(-4.7, 10.08) * mm});
            skLineSegment(sketch, "E5.3.3.5", {"start": v(-12.7, 3.63) * mm, "end": v(-11.11, 6.38) * mm});
            skLineSegment(sketch, "E5.3.3.6", {"start": v(-1.53, 10.08) * mm, "end": v(0.06, 7.33) * mm});
            skLineSegment(sketch, "E5.3.3.7", {"start": v(-1.53, -2.83) * mm, "end": v(-4.7, -2.83) * mm});
            skLineSegment(sketch, "E5.3.3.8", {"start": v(0.06, 7.33) * mm, "end": v(-1.53, 4.58) * mm});
            skLineSegment(sketch, "E5.3.3.9", {"start": v(-12.7, -3.78) * mm, "end": v(-11.11, -1.03) * mm});
            skLineSegment(sketch, "E5.3.3.10", {"start": v(-7.94, 6.38) * mm, "end": v(-6.35, 3.63) * mm});
            skLineSegment(sketch, "E5.3.3.11", {"start": v(-6.29, -0.08) * mm, "end": v(-4.7, 2.67) * mm});
            skLineSegment(sketch, "E5.3.3.12", {"start": v(-4.7, 4.58) * mm, "end": v(-6.29, 7.33) * mm});
            skLineSegment(sketch, "E5.3.3.13", {"start": v(-7.94, -1.03) * mm, "end": v(-6.35, -3.78) * mm});
            skLineSegment(sketch, "E5.3.3.14", {"start": v(-4.7, 10.08) * mm, "end": v(-1.53, 10.08) * mm});
            skLineSegment(sketch, "E5.3.3.15", {"start": v(-7.94, -6.53) * mm, "end": v(-11.11, -6.53) * mm});
            skLineSegment(sketch, "E5.3.3.16", {"start": v(-11.11, 0.88) * mm, "end": v(-12.7, 3.63) * mm});
            skLineSegment(sketch, "E5.3.3.17", {"start": v(0.06, -0.08) * mm, "end": v(-1.53, -2.83) * mm});
            skLineSegment(sketch, "E5.3.3.18", {"start": v(-11.11, -6.53) * mm, "end": v(-12.7, -3.78) * mm});
            skLineSegment(sketch, "E5.3.3.19", {"start": v(-11.11, 6.38) * mm, "end": v(-7.94, 6.38) * mm});
            skLineSegment(sketch, "E5.3.3.20", {"start": v(-4.7, -2.83) * mm, "end": v(-6.29, -0.08) * mm});
            skLineSegment(sketch, "E5.3.3.21", {"start": v(-1.53, 4.58) * mm, "end": v(-4.7, 4.58) * mm});
            skLineSegment(sketch, "E5.3.3.22", {"start": v(-11.11, -1.03) * mm, "end": v(-7.94, -1.03) * mm});
            skLineSegment(sketch, "E5.3.3.23", {"start": v(-6.35, 3.63) * mm, "end": v(-7.94, 0.88) * mm});
            skLineSegment(sketch, "E5.3.4.0", {"start": v(-4.7, -12.13) * mm, "end": v(-1.53, -12.13) * mm});
            skLineSegment(sketch, "E5.3.4.1", {"start": v(-7.94, -13.93) * mm, "end": v(-11.11, -13.93) * mm});
            skLineSegment(sketch, "E5.3.4.2", {"start": v(-6.35, -18.59) * mm, "end": v(-7.94, -21.34) * mm});
            skLineSegment(sketch, "E5.3.4.3", {"start": v(-1.53, -12.13) * mm, "end": v(0.06, -14.88) * mm});
            skLineSegment(sketch, "E5.3.4.4", {"start": v(-6.29, -7.48) * mm, "end": v(-4.7, -4.73) * mm});
            skLineSegment(sketch, "E5.3.4.5", {"start": v(-12.7, -11.18) * mm, "end": v(-11.11, -8.43) * mm});
            skLineSegment(sketch, "E5.3.4.6", {"start": v(-1.53, -4.73) * mm, "end": v(0.06, -7.48) * mm});
            skLineSegment(sketch, "E5.3.4.7", {"start": v(-1.53, -17.63) * mm, "end": v(-4.7, -17.63) * mm});
            skLineSegment(sketch, "E5.3.4.8", {"start": v(0.06, -7.48) * mm, "end": v(-1.53, -10.23) * mm});
            skLineSegment(sketch, "E5.3.4.9", {"start": v(-12.7, -18.59) * mm, "end": v(-11.11, -15.84) * mm});
            skLineSegment(sketch, "E5.3.4.10", {"start": v(-7.94, -8.43) * mm, "end": v(-6.35, -11.18) * mm});
            skLineSegment(sketch, "E5.3.4.11", {"start": v(-6.29, -14.88) * mm, "end": v(-4.7, -12.13) * mm});
            skLineSegment(sketch, "E5.3.4.12", {"start": v(-4.7, -10.23) * mm, "end": v(-6.29, -7.48) * mm});
            skLineSegment(sketch, "E5.3.4.13", {"start": v(-7.94, -15.84) * mm, "end": v(-6.35, -18.59) * mm});
            skLineSegment(sketch, "E5.3.4.14", {"start": v(-4.7, -4.73) * mm, "end": v(-1.53, -4.73) * mm});
            skLineSegment(sketch, "E5.3.4.15", {"start": v(-7.94, -21.34) * mm, "end": v(-11.11, -21.34) * mm});
            skLineSegment(sketch, "E5.3.4.16", {"start": v(-11.11, -13.93) * mm, "end": v(-12.7, -11.18) * mm});
            skLineSegment(sketch, "E5.3.4.17", {"start": v(0.06, -14.88) * mm, "end": v(-1.53, -17.63) * mm});
            skLineSegment(sketch, "E5.3.4.18", {"start": v(-11.11, -21.34) * mm, "end": v(-12.7, -18.59) * mm});
            skLineSegment(sketch, "E5.3.4.19", {"start": v(-11.11, -8.43) * mm, "end": v(-7.94, -8.43) * mm});
            skLineSegment(sketch, "E5.3.4.20", {"start": v(-4.7, -17.63) * mm, "end": v(-6.29, -14.88) * mm});
            skLineSegment(sketch, "E5.3.4.21", {"start": v(-1.53, -10.23) * mm, "end": v(-4.7, -10.23) * mm});
            skLineSegment(sketch, "E5.3.4.22", {"start": v(-11.11, -15.84) * mm, "end": v(-7.94, -15.84) * mm});
            skLineSegment(sketch, "E5.3.4.23", {"start": v(-6.35, -11.18) * mm, "end": v(-7.94, -13.93) * mm});
            skLineSegment(sketch, "E5.3.5.0", {"start": v(-4.7, -26.94) * mm, "end": v(-1.53, -26.94) * mm});
            skLineSegment(sketch, "E5.3.5.1", {"start": v(-7.94, -28.74) * mm, "end": v(-11.11, -28.74) * mm});
            skLineSegment(sketch, "E5.3.5.2", {"start": v(-6.35, -33.4) * mm, "end": v(-7.94, -36.14) * mm});
            skLineSegment(sketch, "E5.3.5.3", {"start": v(-1.53, -26.94) * mm, "end": v(0.06, -29.7) * mm});
            skLineSegment(sketch, "E5.3.5.4", {"start": v(-6.29, -22.29) * mm, "end": v(-4.7, -19.54) * mm});
            skLineSegment(sketch, "E5.3.5.5", {"start": v(-12.7, -26) * mm, "end": v(-11.11, -23.24) * mm});
            skLineSegment(sketch, "E5.3.5.6", {"start": v(-1.53, -19.54) * mm, "end": v(0.06, -22.29) * mm});
            skLineSegment(sketch, "E5.3.5.7", {"start": v(-1.53, -32.44) * mm, "end": v(-4.7, -32.44) * mm});
            skLineSegment(sketch, "E5.3.5.8", {"start": v(0.06, -22.29) * mm, "end": v(-1.53, -25.04) * mm});
            skLineSegment(sketch, "E5.3.5.9", {"start": v(-12.7, -33.4) * mm, "end": v(-11.11, -30.65) * mm});
            skLineSegment(sketch, "E5.3.5.10", {"start": v(-7.94, -23.24) * mm, "end": v(-6.35, -26) * mm});
            skLineSegment(sketch, "E5.3.5.11", {"start": v(-6.29, -29.7) * mm, "end": v(-4.7, -26.94) * mm});
            skLineSegment(sketch, "E5.3.5.12", {"start": v(-4.7, -25.04) * mm, "end": v(-6.29, -22.29) * mm});
            skLineSegment(sketch, "E5.3.5.13", {"start": v(-7.94, -30.65) * mm, "end": v(-6.35, -33.4) * mm});
            skLineSegment(sketch, "E5.3.5.14", {"start": v(-4.7, -19.54) * mm, "end": v(-1.53, -19.54) * mm});
            skLineSegment(sketch, "E5.3.5.15", {"start": v(-7.94, -36.14) * mm, "end": v(-11.11, -36.14) * mm});
            skLineSegment(sketch, "E5.3.5.16", {"start": v(-11.11, -28.74) * mm, "end": v(-12.7, -26) * mm});
            skLineSegment(sketch, "E5.3.5.17", {"start": v(0.06, -29.7) * mm, "end": v(-1.53, -32.44) * mm});
            skLineSegment(sketch, "E5.3.5.18", {"start": v(-11.11, -36.14) * mm, "end": v(-12.7, -33.4) * mm});
            skLineSegment(sketch, "E5.3.5.19", {"start": v(-11.11, -23.24) * mm, "end": v(-7.94, -23.24) * mm});
            skLineSegment(sketch, "E5.3.5.20", {"start": v(-4.7, -32.44) * mm, "end": v(-6.29, -29.7) * mm});
            skLineSegment(sketch, "E5.3.5.21", {"start": v(-1.53, -25.04) * mm, "end": v(-4.7, -25.04) * mm});
            skLineSegment(sketch, "E5.3.5.22", {"start": v(-11.11, -30.65) * mm, "end": v(-7.94, -30.65) * mm});
            skLineSegment(sketch, "E5.3.5.23", {"start": v(-6.35, -26) * mm, "end": v(-7.94, -28.74) * mm});
            skLineSegment(sketch, "E5.3.6.0", {"start": v(-4.7, -41.75) * mm, "end": v(-1.53, -41.75) * mm});
            skLineSegment(sketch, "E5.3.6.1", {"start": v(-7.94, -43.55) * mm, "end": v(-11.11, -43.55) * mm});
            skLineSegment(sketch, "E5.3.6.2", {"start": v(-6.35, -48.2) * mm, "end": v(-7.94, -50.95) * mm});
            skLineSegment(sketch, "E5.3.6.3", {"start": v(-1.53, -41.75) * mm, "end": v(0.06, -44.5) * mm});
            skLineSegment(sketch, "E5.3.6.4", {"start": v(-6.29, -37.1) * mm, "end": v(-4.7, -34.35) * mm});
            skLineSegment(sketch, "E5.3.6.5", {"start": v(-12.7, -40.8) * mm, "end": v(-11.11, -38.05) * mm});
            skLineSegment(sketch, "E5.3.6.6", {"start": v(-1.53, -34.35) * mm, "end": v(0.06, -37.1) * mm});
            skLineSegment(sketch, "E5.3.6.7", {"start": v(-1.53, -47.25) * mm, "end": v(-4.7, -47.25) * mm});
            skLineSegment(sketch, "E5.3.6.8", {"start": v(0.06, -37.1) * mm, "end": v(-1.53, -39.85) * mm});
            skLineSegment(sketch, "E5.3.6.9", {"start": v(-12.7, -48.2) * mm, "end": v(-11.11, -45.45) * mm});
            skLineSegment(sketch, "E5.3.6.10", {"start": v(-7.94, -38.05) * mm, "end": v(-6.35, -40.8) * mm});
            skLineSegment(sketch, "E5.3.6.11", {"start": v(-6.29, -44.5) * mm, "end": v(-4.7, -41.75) * mm});
            skLineSegment(sketch, "E5.3.6.12", {"start": v(-4.7, -39.85) * mm, "end": v(-6.29, -37.1) * mm});
            skLineSegment(sketch, "E5.3.6.13", {"start": v(-7.94, -45.45) * mm, "end": v(-6.35, -48.2) * mm});
            skLineSegment(sketch, "E5.3.6.14", {"start": v(-4.7, -34.35) * mm, "end": v(-1.53, -34.35) * mm});
            skLineSegment(sketch, "E5.3.6.15", {"start": v(-7.94, -50.95) * mm, "end": v(-11.11, -50.95) * mm});
            skLineSegment(sketch, "E5.3.6.16", {"start": v(-11.11, -43.55) * mm, "end": v(-12.7, -40.8) * mm});
            skLineSegment(sketch, "E5.3.6.17", {"start": v(0.06, -44.5) * mm, "end": v(-1.53, -47.25) * mm});
            skLineSegment(sketch, "E5.3.6.18", {"start": v(-11.11, -50.95) * mm, "end": v(-12.7, -48.2) * mm});
            skLineSegment(sketch, "E5.3.6.19", {"start": v(-11.11, -38.05) * mm, "end": v(-7.94, -38.05) * mm});
            skLineSegment(sketch, "E5.3.6.20", {"start": v(-4.7, -47.25) * mm, "end": v(-6.29, -44.5) * mm});
            skLineSegment(sketch, "E5.3.6.21", {"start": v(-1.53, -39.85) * mm, "end": v(-4.7, -39.85) * mm});
            skLineSegment(sketch, "E5.3.6.22", {"start": v(-11.11, -45.45) * mm, "end": v(-7.94, -45.45) * mm});
            skLineSegment(sketch, "E5.3.6.23", {"start": v(-6.35, -40.8) * mm, "end": v(-7.94, -43.55) * mm});
            skLineSegment(sketch, "E5.4.0.0", {"start": v(8, 47.1) * mm, "end": v(11.17, 47.1) * mm});
            skLineSegment(sketch, "E5.4.0.1", {"start": v(4.76, 45.3) * mm, "end": v(1.59, 45.3) * mm});
            skLineSegment(sketch, "E5.4.0.2", {"start": v(6.35, 40.65) * mm, "end": v(4.76, 37.9) * mm});
            skLineSegment(sketch, "E5.4.0.3", {"start": v(11.17, 47.1) * mm, "end": v(12.76, 44.35) * mm});
            skLineSegment(sketch, "E5.4.0.4", {"start": v(6.41, 51.75) * mm, "end": v(8, 54.5) * mm});
            skLineSegment(sketch, "E5.4.0.5", {"start": v(0, 48.05) * mm, "end": v(1.59, 50.8) * mm});
            skLineSegment(sketch, "E5.4.0.6", {"start": v(11.17, 54.5) * mm, "end": v(12.76, 51.75) * mm});
            skLineSegment(sketch, "E5.4.0.7", {"start": v(11.17, 41.6) * mm, "end": v(8, 41.6) * mm});
            skLineSegment(sketch, "E5.4.0.8", {"start": v(12.76, 51.75) * mm, "end": v(11.17, 49) * mm});
            skLineSegment(sketch, "E5.4.0.9", {"start": v(0, 40.65) * mm, "end": v(1.59, 43.4) * mm});
            skLineSegment(sketch, "E5.4.0.10", {"start": v(4.76, 50.8) * mm, "end": v(6.35, 48.05) * mm});
            skLineSegment(sketch, "E5.4.0.11", {"start": v(6.41, 44.35) * mm, "end": v(8, 47.1) * mm});
            skLineSegment(sketch, "E5.4.0.12", {"start": v(8, 49) * mm, "end": v(6.41, 51.75) * mm});
            skLineSegment(sketch, "E5.4.0.13", {"start": v(4.76, 43.4) * mm, "end": v(6.35, 40.65) * mm});
            skLineSegment(sketch, "E5.4.0.14", {"start": v(8, 54.5) * mm, "end": v(11.17, 54.5) * mm});
            skLineSegment(sketch, "E5.4.0.15", {"start": v(4.76, 37.9) * mm, "end": v(1.59, 37.9) * mm});
            skLineSegment(sketch, "E5.4.0.16", {"start": v(1.59, 45.3) * mm, "end": v(0, 48.05) * mm});
            skLineSegment(sketch, "E5.4.0.17", {"start": v(12.76, 44.35) * mm, "end": v(11.17, 41.6) * mm});
            skLineSegment(sketch, "E5.4.0.18", {"start": v(1.59, 37.9) * mm, "end": v(0, 40.65) * mm});
            skLineSegment(sketch, "E5.4.0.19", {"start": v(1.59, 50.8) * mm, "end": v(4.76, 50.8) * mm});
            skLineSegment(sketch, "E5.4.0.20", {"start": v(8, 41.6) * mm, "end": v(6.41, 44.35) * mm});
            skLineSegment(sketch, "E5.4.0.21", {"start": v(11.17, 49) * mm, "end": v(8, 49) * mm});
            skLineSegment(sketch, "E5.4.0.22", {"start": v(1.59, 43.4) * mm, "end": v(4.76, 43.4) * mm});
            skLineSegment(sketch, "E5.4.0.23", {"start": v(6.35, 48.05) * mm, "end": v(4.76, 45.3) * mm});
            skLineSegment(sketch, "E5.4.1.0", {"start": v(8, 32.29) * mm, "end": v(11.17, 32.29) * mm});
            skLineSegment(sketch, "E5.4.1.1", {"start": v(4.76, 30.5) * mm, "end": v(1.59, 30.5) * mm});
            skLineSegment(sketch, "E5.4.1.2", {"start": v(6.35, 25.84) * mm, "end": v(4.76, 23.09) * mm});
            skLineSegment(sketch, "E5.4.1.3", {"start": v(11.17, 32.29) * mm, "end": v(12.76, 29.54) * mm});
            skLineSegment(sketch, "E5.4.1.4", {"start": v(6.41, 36.94) * mm, "end": v(8, 39.7) * mm});
            skLineSegment(sketch, "E5.4.1.5", {"start": v(0, 33.24) * mm, "end": v(1.59, 36) * mm});
            skLineSegment(sketch, "E5.4.1.6", {"start": v(11.17, 39.7) * mm, "end": v(12.76, 36.94) * mm});
            skLineSegment(sketch, "E5.4.1.7", {"start": v(11.17, 26.8) * mm, "end": v(8, 26.8) * mm});
            skLineSegment(sketch, "E5.4.1.8", {"start": v(12.76, 36.94) * mm, "end": v(11.17, 34.2) * mm});
            skLineSegment(sketch, "E5.4.1.9", {"start": v(0, 25.84) * mm, "end": v(1.59, 28.59) * mm});
            skLineSegment(sketch, "E5.4.1.10", {"start": v(4.76, 36) * mm, "end": v(6.35, 33.24) * mm});
            skLineSegment(sketch, "E5.4.1.11", {"start": v(6.41, 29.54) * mm, "end": v(8, 32.29) * mm});
            skLineSegment(sketch, "E5.4.1.12", {"start": v(8, 34.2) * mm, "end": v(6.41, 36.94) * mm});
            skLineSegment(sketch, "E5.4.1.13", {"start": v(4.76, 28.59) * mm, "end": v(6.35, 25.84) * mm});
            skLineSegment(sketch, "E5.4.1.14", {"start": v(8, 39.7) * mm, "end": v(11.17, 39.7) * mm});
            skLineSegment(sketch, "E5.4.1.15", {"start": v(4.76, 23.09) * mm, "end": v(1.59, 23.09) * mm});
            skLineSegment(sketch, "E5.4.1.16", {"start": v(1.59, 30.5) * mm, "end": v(0, 33.24) * mm});
            skLineSegment(sketch, "E5.4.1.17", {"start": v(12.76, 29.54) * mm, "end": v(11.17, 26.8) * mm});
            skLineSegment(sketch, "E5.4.1.18", {"start": v(1.59, 23.09) * mm, "end": v(0, 25.84) * mm});
            skLineSegment(sketch, "E5.4.1.19", {"start": v(1.59, 36) * mm, "end": v(4.76, 36) * mm});
            skLineSegment(sketch, "E5.4.1.20", {"start": v(8, 26.8) * mm, "end": v(6.41, 29.54) * mm});
            skLineSegment(sketch, "E5.4.1.21", {"start": v(11.17, 34.2) * mm, "end": v(8, 34.2) * mm});
            skLineSegment(sketch, "E5.4.1.22", {"start": v(1.59, 28.59) * mm, "end": v(4.76, 28.59) * mm});
            skLineSegment(sketch, "E5.4.1.23", {"start": v(6.35, 33.24) * mm, "end": v(4.76, 30.5) * mm});
            skLineSegment(sketch, "E5.4.2.0", {"start": v(8, 17.48) * mm, "end": v(11.17, 17.48) * mm});
            skLineSegment(sketch, "E5.4.2.1", {"start": v(4.76, 15.68) * mm, "end": v(1.59, 15.68) * mm});
            skLineSegment(sketch, "E5.4.2.2", {"start": v(6.35, 11.03) * mm, "end": v(4.76, 8.28) * mm});
            skLineSegment(sketch, "E5.4.2.3", {"start": v(11.17, 17.48) * mm, "end": v(12.76, 14.73) * mm});
            skLineSegment(sketch, "E5.4.2.4", {"start": v(6.41, 22.14) * mm, "end": v(8, 24.89) * mm});
            skLineSegment(sketch, "E5.4.2.5", {"start": v(0, 18.43) * mm, "end": v(1.59, 21.18) * mm});
            skLineSegment(sketch, "E5.4.2.6", {"start": v(11.17, 24.89) * mm, "end": v(12.76, 22.14) * mm});
            skLineSegment(sketch, "E5.4.2.7", {"start": v(11.17, 11.98) * mm, "end": v(8, 11.98) * mm});
            skLineSegment(sketch, "E5.4.2.8", {"start": v(12.76, 22.14) * mm, "end": v(11.17, 19.39) * mm});
            skLineSegment(sketch, "E5.4.2.9", {"start": v(0, 11.03) * mm, "end": v(1.59, 13.78) * mm});
            skLineSegment(sketch, "E5.4.2.10", {"start": v(4.76, 21.18) * mm, "end": v(6.35, 18.43) * mm});
            skLineSegment(sketch, "E5.4.2.11", {"start": v(6.41, 14.73) * mm, "end": v(8, 17.48) * mm});
            skLineSegment(sketch, "E5.4.2.12", {"start": v(8, 19.39) * mm, "end": v(6.41, 22.14) * mm});
            skLineSegment(sketch, "E5.4.2.13", {"start": v(4.76, 13.78) * mm, "end": v(6.35, 11.03) * mm});
            skLineSegment(sketch, "E5.4.2.14", {"start": v(8, 24.89) * mm, "end": v(11.17, 24.89) * mm});
            skLineSegment(sketch, "E5.4.2.15", {"start": v(4.76, 8.28) * mm, "end": v(1.59, 8.28) * mm});
            skLineSegment(sketch, "E5.4.2.16", {"start": v(1.59, 15.68) * mm, "end": v(0, 18.43) * mm});
            skLineSegment(sketch, "E5.4.2.17", {"start": v(12.76, 14.73) * mm, "end": v(11.17, 11.98) * mm});
            skLineSegment(sketch, "E5.4.2.18", {"start": v(1.59, 8.28) * mm, "end": v(0, 11.03) * mm});
            skLineSegment(sketch, "E5.4.2.19", {"start": v(1.59, 21.18) * mm, "end": v(4.76, 21.18) * mm});
            skLineSegment(sketch, "E5.4.2.20", {"start": v(8, 11.98) * mm, "end": v(6.41, 14.73) * mm});
            skLineSegment(sketch, "E5.4.2.21", {"start": v(11.17, 19.39) * mm, "end": v(8, 19.39) * mm});
            skLineSegment(sketch, "E5.4.2.22", {"start": v(1.59, 13.78) * mm, "end": v(4.76, 13.78) * mm});
            skLineSegment(sketch, "E5.4.2.23", {"start": v(6.35, 18.43) * mm, "end": v(4.76, 15.68) * mm});
            skLineSegment(sketch, "E5.4.3.0", {"start": v(8, 2.67) * mm, "end": v(11.17, 2.67) * mm});
            skLineSegment(sketch, "E5.4.3.1", {"start": v(4.76, 0.88) * mm, "end": v(1.59, 0.88) * mm});
            skLineSegment(sketch, "E5.4.3.2", {"start": v(6.35, -3.78) * mm, "end": v(4.76, -6.53) * mm});
            skLineSegment(sketch, "E5.4.3.3", {"start": v(11.17, 2.67) * mm, "end": v(12.76, -0.08) * mm});
            skLineSegment(sketch, "E5.4.3.4", {"start": v(6.41, 7.33) * mm, "end": v(8, 10.08) * mm});
            skLineSegment(sketch, "E5.4.3.5", {"start": v(0, 3.63) * mm, "end": v(1.59, 6.38) * mm});
            skLineSegment(sketch, "E5.4.3.6", {"start": v(11.17, 10.08) * mm, "end": v(12.76, 7.33) * mm});
            skLineSegment(sketch, "E5.4.3.7", {"start": v(11.17, -2.83) * mm, "end": v(8, -2.83) * mm});
            skLineSegment(sketch, "E5.4.3.8", {"start": v(12.76, 7.33) * mm, "end": v(11.17, 4.58) * mm});
            skLineSegment(sketch, "E5.4.3.9", {"start": v(0, -3.78) * mm, "end": v(1.59, -1.03) * mm});
            skLineSegment(sketch, "E5.4.3.10", {"start": v(4.76, 6.38) * mm, "end": v(6.35, 3.63) * mm});
            skLineSegment(sketch, "E5.4.3.11", {"start": v(6.41, -0.08) * mm, "end": v(8, 2.67) * mm});
            skLineSegment(sketch, "E5.4.3.12", {"start": v(8, 4.58) * mm, "end": v(6.41, 7.33) * mm});
            skLineSegment(sketch, "E5.4.3.13", {"start": v(4.76, -1.03) * mm, "end": v(6.35, -3.78) * mm});
            skLineSegment(sketch, "E5.4.3.14", {"start": v(8, 10.08) * mm, "end": v(11.17, 10.08) * mm});
            skLineSegment(sketch, "E5.4.3.15", {"start": v(4.76, -6.53) * mm, "end": v(1.59, -6.53) * mm});
            skLineSegment(sketch, "E5.4.3.16", {"start": v(1.59, 0.88) * mm, "end": v(0, 3.63) * mm});
            skLineSegment(sketch, "E5.4.3.17", {"start": v(12.76, -0.08) * mm, "end": v(11.17, -2.83) * mm});
            skLineSegment(sketch, "E5.4.3.18", {"start": v(1.59, -6.53) * mm, "end": v(0, -3.78) * mm});
            skLineSegment(sketch, "E5.4.3.19", {"start": v(1.59, 6.38) * mm, "end": v(4.76, 6.38) * mm});
            skLineSegment(sketch, "E5.4.3.20", {"start": v(8, -2.83) * mm, "end": v(6.41, -0.08) * mm});
            skLineSegment(sketch, "E5.4.3.21", {"start": v(11.17, 4.58) * mm, "end": v(8, 4.58) * mm});
            skLineSegment(sketch, "E5.4.3.22", {"start": v(1.59, -1.03) * mm, "end": v(4.76, -1.03) * mm});
            skLineSegment(sketch, "E5.4.3.23", {"start": v(6.35, 3.63) * mm, "end": v(4.76, 0.88) * mm});
            skLineSegment(sketch, "E5.4.4.0", {"start": v(8, -12.13) * mm, "end": v(11.17, -12.13) * mm});
            skLineSegment(sketch, "E5.4.4.1", {"start": v(4.76, -13.93) * mm, "end": v(1.59, -13.93) * mm});
            skLineSegment(sketch, "E5.4.4.2", {"start": v(6.35, -18.59) * mm, "end": v(4.76, -21.34) * mm});
            skLineSegment(sketch, "E5.4.4.3", {"start": v(11.17, -12.13) * mm, "end": v(12.76, -14.88) * mm});
            skLineSegment(sketch, "E5.4.4.4", {"start": v(6.41, -7.48) * mm, "end": v(8, -4.73) * mm});
            skLineSegment(sketch, "E5.4.4.5", {"start": v(0, -11.18) * mm, "end": v(1.59, -8.43) * mm});
            skLineSegment(sketch, "E5.4.4.6", {"start": v(11.17, -4.73) * mm, "end": v(12.76, -7.48) * mm});
            skLineSegment(sketch, "E5.4.4.7", {"start": v(11.17, -17.63) * mm, "end": v(8, -17.63) * mm});
            skLineSegment(sketch, "E5.4.4.8", {"start": v(12.76, -7.48) * mm, "end": v(11.17, -10.23) * mm});
            skLineSegment(sketch, "E5.4.4.9", {"start": v(0, -18.59) * mm, "end": v(1.59, -15.84) * mm});
            skLineSegment(sketch, "E5.4.4.10", {"start": v(4.76, -8.43) * mm, "end": v(6.35, -11.18) * mm});
            skLineSegment(sketch, "E5.4.4.11", {"start": v(6.41, -14.88) * mm, "end": v(8, -12.13) * mm});
            skLineSegment(sketch, "E5.4.4.12", {"start": v(8, -10.23) * mm, "end": v(6.41, -7.48) * mm});
            skLineSegment(sketch, "E5.4.4.13", {"start": v(4.76, -15.84) * mm, "end": v(6.35, -18.59) * mm});
            skLineSegment(sketch, "E5.4.4.14", {"start": v(8, -4.73) * mm, "end": v(11.17, -4.73) * mm});
            skLineSegment(sketch, "E5.4.4.15", {"start": v(4.76, -21.34) * mm, "end": v(1.59, -21.34) * mm});
            skLineSegment(sketch, "E5.4.4.16", {"start": v(1.59, -13.93) * mm, "end": v(0, -11.18) * mm});
            skLineSegment(sketch, "E5.4.4.17", {"start": v(12.76, -14.88) * mm, "end": v(11.17, -17.63) * mm});
            skLineSegment(sketch, "E5.4.4.18", {"start": v(1.59, -21.34) * mm, "end": v(0, -18.59) * mm});
            skLineSegment(sketch, "E5.4.4.19", {"start": v(1.59, -8.43) * mm, "end": v(4.76, -8.43) * mm});
            skLineSegment(sketch, "E5.4.4.20", {"start": v(8, -17.63) * mm, "end": v(6.41, -14.88) * mm});
            skLineSegment(sketch, "E5.4.4.21", {"start": v(11.17, -10.23) * mm, "end": v(8, -10.23) * mm});
            skLineSegment(sketch, "E5.4.4.22", {"start": v(1.59, -15.84) * mm, "end": v(4.76, -15.84) * mm});
            skLineSegment(sketch, "E5.4.4.23", {"start": v(6.35, -11.18) * mm, "end": v(4.76, -13.93) * mm});
            skLineSegment(sketch, "E5.4.5.0", {"start": v(8, -26.94) * mm, "end": v(11.17, -26.94) * mm});
            skLineSegment(sketch, "E5.4.5.1", {"start": v(4.76, -28.74) * mm, "end": v(1.59, -28.74) * mm});
            skLineSegment(sketch, "E5.4.5.2", {"start": v(6.35, -33.4) * mm, "end": v(4.76, -36.14) * mm});
            skLineSegment(sketch, "E5.4.5.3", {"start": v(11.17, -26.94) * mm, "end": v(12.76, -29.7) * mm});
            skLineSegment(sketch, "E5.4.5.4", {"start": v(6.41, -22.29) * mm, "end": v(8, -19.54) * mm});
            skLineSegment(sketch, "E5.4.5.5", {"start": v(0, -26) * mm, "end": v(1.59, -23.24) * mm});
            skLineSegment(sketch, "E5.4.5.6", {"start": v(11.17, -19.54) * mm, "end": v(12.76, -22.29) * mm});
            skLineSegment(sketch, "E5.4.5.7", {"start": v(11.17, -32.44) * mm, "end": v(8, -32.44) * mm});
            skLineSegment(sketch, "E5.4.5.8", {"start": v(12.76, -22.29) * mm, "end": v(11.17, -25.04) * mm});
            skLineSegment(sketch, "E5.4.5.9", {"start": v(0, -33.4) * mm, "end": v(1.59, -30.65) * mm});
            skLineSegment(sketch, "E5.4.5.10", {"start": v(4.76, -23.24) * mm, "end": v(6.35, -26) * mm});
            skLineSegment(sketch, "E5.4.5.11", {"start": v(6.41, -29.7) * mm, "end": v(8, -26.94) * mm});
            skLineSegment(sketch, "E5.4.5.12", {"start": v(8, -25.04) * mm, "end": v(6.41, -22.29) * mm});
            skLineSegment(sketch, "E5.4.5.13", {"start": v(4.76, -30.65) * mm, "end": v(6.35, -33.4) * mm});
            skLineSegment(sketch, "E5.4.5.14", {"start": v(8, -19.54) * mm, "end": v(11.17, -19.54) * mm});
            skLineSegment(sketch, "E5.4.5.15", {"start": v(4.76, -36.14) * mm, "end": v(1.59, -36.14) * mm});
            skLineSegment(sketch, "E5.4.5.16", {"start": v(1.59, -28.74) * mm, "end": v(0, -26) * mm});
            skLineSegment(sketch, "E5.4.5.17", {"start": v(12.76, -29.7) * mm, "end": v(11.17, -32.44) * mm});
            skLineSegment(sketch, "E5.4.5.18", {"start": v(1.59, -36.14) * mm, "end": v(0, -33.4) * mm});
            skLineSegment(sketch, "E5.4.5.19", {"start": v(1.59, -23.24) * mm, "end": v(4.76, -23.24) * mm});
            skLineSegment(sketch, "E5.4.5.20", {"start": v(8, -32.44) * mm, "end": v(6.41, -29.7) * mm});
            skLineSegment(sketch, "E5.4.5.21", {"start": v(11.17, -25.04) * mm, "end": v(8, -25.04) * mm});
            skLineSegment(sketch, "E5.4.5.22", {"start": v(1.59, -30.65) * mm, "end": v(4.76, -30.65) * mm});
            skLineSegment(sketch, "E5.4.5.23", {"start": v(6.35, -26) * mm, "end": v(4.76, -28.74) * mm});
            skLineSegment(sketch, "E5.4.6.0", {"start": v(8, -41.75) * mm, "end": v(11.17, -41.75) * mm});
            skLineSegment(sketch, "E5.4.6.1", {"start": v(4.76, -43.55) * mm, "end": v(1.59, -43.55) * mm});
            skLineSegment(sketch, "E5.4.6.2", {"start": v(6.35, -48.2) * mm, "end": v(4.76, -50.95) * mm});
            skLineSegment(sketch, "E5.4.6.3", {"start": v(11.17, -41.75) * mm, "end": v(12.76, -44.5) * mm});
            skLineSegment(sketch, "E5.4.6.4", {"start": v(6.41, -37.1) * mm, "end": v(8, -34.35) * mm});
            skLineSegment(sketch, "E5.4.6.5", {"start": v(0, -40.8) * mm, "end": v(1.59, -38.05) * mm});
            skLineSegment(sketch, "E5.4.6.6", {"start": v(11.17, -34.35) * mm, "end": v(12.76, -37.1) * mm});
            skLineSegment(sketch, "E5.4.6.7", {"start": v(11.17, -47.25) * mm, "end": v(8, -47.25) * mm});
            skLineSegment(sketch, "E5.4.6.8", {"start": v(12.76, -37.1) * mm, "end": v(11.17, -39.85) * mm});
            skLineSegment(sketch, "E5.4.6.9", {"start": v(0, -48.2) * mm, "end": v(1.59, -45.45) * mm});
            skLineSegment(sketch, "E5.4.6.10", {"start": v(4.76, -38.05) * mm, "end": v(6.35, -40.8) * mm});
            skLineSegment(sketch, "E5.4.6.11", {"start": v(6.41, -44.5) * mm, "end": v(8, -41.75) * mm});
            skLineSegment(sketch, "E5.4.6.12", {"start": v(8, -39.85) * mm, "end": v(6.41, -37.1) * mm});
            skLineSegment(sketch, "E5.4.6.13", {"start": v(4.76, -45.45) * mm, "end": v(6.35, -48.2) * mm});
            skLineSegment(sketch, "E5.4.6.14", {"start": v(8, -34.35) * mm, "end": v(11.17, -34.35) * mm});
            skLineSegment(sketch, "E5.4.6.15", {"start": v(4.76, -50.95) * mm, "end": v(1.59, -50.95) * mm});
            skLineSegment(sketch, "E5.4.6.16", {"start": v(1.59, -43.55) * mm, "end": v(0, -40.8) * mm});
            skLineSegment(sketch, "E5.4.6.17", {"start": v(12.76, -44.5) * mm, "end": v(11.17, -47.25) * mm});
            skLineSegment(sketch, "E5.4.6.18", {"start": v(1.59, -50.95) * mm, "end": v(0, -48.2) * mm});
            skLineSegment(sketch, "E5.4.6.19", {"start": v(1.59, -38.05) * mm, "end": v(4.76, -38.05) * mm});
            skLineSegment(sketch, "E5.4.6.20", {"start": v(8, -47.25) * mm, "end": v(6.41, -44.5) * mm});
            skLineSegment(sketch, "E5.4.6.21", {"start": v(11.17, -39.85) * mm, "end": v(8, -39.85) * mm});
            skLineSegment(sketch, "E5.4.6.22", {"start": v(1.59, -45.45) * mm, "end": v(4.76, -45.45) * mm});
            skLineSegment(sketch, "E5.4.6.23", {"start": v(6.35, -40.8) * mm, "end": v(4.76, -43.55) * mm});
            skLineSegment(sketch, "E5.5.0.0", {"start": v(20.7, 47.1) * mm, "end": v(23.87, 47.1) * mm});
            skLineSegment(sketch, "E5.5.0.1", {"start": v(17.46, 45.3) * mm, "end": v(14.29, 45.3) * mm});
            skLineSegment(sketch, "E5.5.0.2", {"start": v(19.05, 40.65) * mm, "end": v(17.46, 37.9) * mm});
            skLineSegment(sketch, "E5.5.0.3", {"start": v(23.87, 47.1) * mm, "end": v(25.46, 44.35) * mm});
            skLineSegment(sketch, "E5.5.0.4", {"start": v(19.11, 51.75) * mm, "end": v(20.7, 54.5) * mm});
            skLineSegment(sketch, "E5.5.0.5", {"start": v(12.7, 48.05) * mm, "end": v(14.29, 50.8) * mm});
            skLineSegment(sketch, "E5.5.0.6", {"start": v(23.87, 54.5) * mm, "end": v(25.46, 51.75) * mm});
            skLineSegment(sketch, "E5.5.0.7", {"start": v(23.87, 41.6) * mm, "end": v(20.7, 41.6) * mm});
            skLineSegment(sketch, "E5.5.0.8", {"start": v(25.46, 51.75) * mm, "end": v(23.87, 49) * mm});
            skLineSegment(sketch, "E5.5.0.9", {"start": v(12.7, 40.65) * mm, "end": v(14.29, 43.4) * mm});
            skLineSegment(sketch, "E5.5.0.10", {"start": v(17.46, 50.8) * mm, "end": v(19.05, 48.05) * mm});
            skLineSegment(sketch, "E5.5.0.11", {"start": v(19.11, 44.35) * mm, "end": v(20.7, 47.1) * mm});
            skLineSegment(sketch, "E5.5.0.12", {"start": v(20.7, 49) * mm, "end": v(19.11, 51.75) * mm});
            skLineSegment(sketch, "E5.5.0.13", {"start": v(17.46, 43.4) * mm, "end": v(19.05, 40.65) * mm});
            skLineSegment(sketch, "E5.5.0.14", {"start": v(20.7, 54.5) * mm, "end": v(23.87, 54.5) * mm});
            skLineSegment(sketch, "E5.5.0.15", {"start": v(17.46, 37.9) * mm, "end": v(14.29, 37.9) * mm});
            skLineSegment(sketch, "E5.5.0.16", {"start": v(14.29, 45.3) * mm, "end": v(12.7, 48.05) * mm});
            skLineSegment(sketch, "E5.5.0.17", {"start": v(25.46, 44.35) * mm, "end": v(23.87, 41.6) * mm});
            skLineSegment(sketch, "E5.5.0.18", {"start": v(14.29, 37.9) * mm, "end": v(12.7, 40.65) * mm});
            skLineSegment(sketch, "E5.5.0.19", {"start": v(14.29, 50.8) * mm, "end": v(17.46, 50.8) * mm});
            skLineSegment(sketch, "E5.5.0.20", {"start": v(20.7, 41.6) * mm, "end": v(19.11, 44.35) * mm});
            skLineSegment(sketch, "E5.5.0.21", {"start": v(23.87, 49) * mm, "end": v(20.7, 49) * mm});
            skLineSegment(sketch, "E5.5.0.22", {"start": v(14.29, 43.4) * mm, "end": v(17.46, 43.4) * mm});
            skLineSegment(sketch, "E5.5.0.23", {"start": v(19.05, 48.05) * mm, "end": v(17.46, 45.3) * mm});
            skLineSegment(sketch, "E5.5.1.0", {"start": v(20.7, 32.29) * mm, "end": v(23.87, 32.29) * mm});
            skLineSegment(sketch, "E5.5.1.1", {"start": v(17.46, 30.5) * mm, "end": v(14.29, 30.5) * mm});
            skLineSegment(sketch, "E5.5.1.2", {"start": v(19.05, 25.84) * mm, "end": v(17.46, 23.09) * mm});
            skLineSegment(sketch, "E5.5.1.3", {"start": v(23.87, 32.29) * mm, "end": v(25.46, 29.54) * mm});
            skLineSegment(sketch, "E5.5.1.4", {"start": v(19.11, 36.94) * mm, "end": v(20.7, 39.7) * mm});
            skLineSegment(sketch, "E5.5.1.5", {"start": v(12.7, 33.24) * mm, "end": v(14.29, 36) * mm});
            skLineSegment(sketch, "E5.5.1.6", {"start": v(23.87, 39.7) * mm, "end": v(25.46, 36.94) * mm});
            skLineSegment(sketch, "E5.5.1.7", {"start": v(23.87, 26.8) * mm, "end": v(20.7, 26.8) * mm});
            skLineSegment(sketch, "E5.5.1.8", {"start": v(25.46, 36.94) * mm, "end": v(23.87, 34.2) * mm});
            skLineSegment(sketch, "E5.5.1.9", {"start": v(12.7, 25.84) * mm, "end": v(14.29, 28.59) * mm});
            skLineSegment(sketch, "E5.5.1.10", {"start": v(17.46, 36) * mm, "end": v(19.05, 33.24) * mm});
            skLineSegment(sketch, "E5.5.1.11", {"start": v(19.11, 29.54) * mm, "end": v(20.7, 32.29) * mm});
            skLineSegment(sketch, "E5.5.1.12", {"start": v(20.7, 34.2) * mm, "end": v(19.11, 36.94) * mm});
            skLineSegment(sketch, "E5.5.1.13", {"start": v(17.46, 28.59) * mm, "end": v(19.05, 25.84) * mm});
            skLineSegment(sketch, "E5.5.1.14", {"start": v(20.7, 39.7) * mm, "end": v(23.87, 39.7) * mm});
            skLineSegment(sketch, "E5.5.1.15", {"start": v(17.46, 23.09) * mm, "end": v(14.29, 23.09) * mm});
            skLineSegment(sketch, "E5.5.1.16", {"start": v(14.29, 30.5) * mm, "end": v(12.7, 33.24) * mm});
            skLineSegment(sketch, "E5.5.1.17", {"start": v(25.46, 29.54) * mm, "end": v(23.87, 26.8) * mm});
            skLineSegment(sketch, "E5.5.1.18", {"start": v(14.29, 23.09) * mm, "end": v(12.7, 25.84) * mm});
            skLineSegment(sketch, "E5.5.1.19", {"start": v(14.29, 36) * mm, "end": v(17.46, 36) * mm});
            skLineSegment(sketch, "E5.5.1.20", {"start": v(20.7, 26.8) * mm, "end": v(19.11, 29.54) * mm});
            skLineSegment(sketch, "E5.5.1.21", {"start": v(23.87, 34.2) * mm, "end": v(20.7, 34.2) * mm});
            skLineSegment(sketch, "E5.5.1.22", {"start": v(14.29, 28.59) * mm, "end": v(17.46, 28.59) * mm});
            skLineSegment(sketch, "E5.5.1.23", {"start": v(19.05, 33.24) * mm, "end": v(17.46, 30.5) * mm});
            skLineSegment(sketch, "E5.5.2.0", {"start": v(20.7, 17.48) * mm, "end": v(23.87, 17.48) * mm});
            skLineSegment(sketch, "E5.5.2.1", {"start": v(17.46, 15.68) * mm, "end": v(14.29, 15.68) * mm});
            skLineSegment(sketch, "E5.5.2.2", {"start": v(19.05, 11.03) * mm, "end": v(17.46, 8.28) * mm});
            skLineSegment(sketch, "E5.5.2.3", {"start": v(23.87, 17.48) * mm, "end": v(25.46, 14.73) * mm});
            skLineSegment(sketch, "E5.5.2.4", {"start": v(19.11, 22.14) * mm, "end": v(20.7, 24.89) * mm});
            skLineSegment(sketch, "E5.5.2.5", {"start": v(12.7, 18.43) * mm, "end": v(14.29, 21.18) * mm});
            skLineSegment(sketch, "E5.5.2.6", {"start": v(23.87, 24.89) * mm, "end": v(25.46, 22.14) * mm});
            skLineSegment(sketch, "E5.5.2.7", {"start": v(23.87, 11.98) * mm, "end": v(20.7, 11.98) * mm});
            skLineSegment(sketch, "E5.5.2.8", {"start": v(25.46, 22.14) * mm, "end": v(23.87, 19.39) * mm});
            skLineSegment(sketch, "E5.5.2.9", {"start": v(12.7, 11.03) * mm, "end": v(14.29, 13.78) * mm});
            skLineSegment(sketch, "E5.5.2.10", {"start": v(17.46, 21.18) * mm, "end": v(19.05, 18.43) * mm});
            skLineSegment(sketch, "E5.5.2.11", {"start": v(19.11, 14.73) * mm, "end": v(20.7, 17.48) * mm});
            skLineSegment(sketch, "E5.5.2.12", {"start": v(20.7, 19.39) * mm, "end": v(19.11, 22.14) * mm});
            skLineSegment(sketch, "E5.5.2.13", {"start": v(17.46, 13.78) * mm, "end": v(19.05, 11.03) * mm});
            skLineSegment(sketch, "E5.5.2.14", {"start": v(20.7, 24.89) * mm, "end": v(23.87, 24.89) * mm});
            skLineSegment(sketch, "E5.5.2.15", {"start": v(17.46, 8.28) * mm, "end": v(14.29, 8.28) * mm});
            skLineSegment(sketch, "E5.5.2.16", {"start": v(14.29, 15.68) * mm, "end": v(12.7, 18.43) * mm});
            skLineSegment(sketch, "E5.5.2.17", {"start": v(25.46, 14.73) * mm, "end": v(23.87, 11.98) * mm});
            skLineSegment(sketch, "E5.5.2.18", {"start": v(14.29, 8.28) * mm, "end": v(12.7, 11.03) * mm});
            skLineSegment(sketch, "E5.5.2.19", {"start": v(14.29, 21.18) * mm, "end": v(17.46, 21.18) * mm});
            skLineSegment(sketch, "E5.5.2.20", {"start": v(20.7, 11.98) * mm, "end": v(19.11, 14.73) * mm});
            skLineSegment(sketch, "E5.5.2.21", {"start": v(23.87, 19.39) * mm, "end": v(20.7, 19.39) * mm});
            skLineSegment(sketch, "E5.5.2.22", {"start": v(14.29, 13.78) * mm, "end": v(17.46, 13.78) * mm});
            skLineSegment(sketch, "E5.5.2.23", {"start": v(19.05, 18.43) * mm, "end": v(17.46, 15.68) * mm});
            skLineSegment(sketch, "E5.5.3.0", {"start": v(20.7, 2.67) * mm, "end": v(23.87, 2.67) * mm});
            skLineSegment(sketch, "E5.5.3.1", {"start": v(17.46, 0.88) * mm, "end": v(14.29, 0.88) * mm});
            skLineSegment(sketch, "E5.5.3.2", {"start": v(19.05, -3.78) * mm, "end": v(17.46, -6.53) * mm});
            skLineSegment(sketch, "E5.5.3.3", {"start": v(23.87, 2.67) * mm, "end": v(25.46, -0.08) * mm});
            skLineSegment(sketch, "E5.5.3.4", {"start": v(19.11, 7.33) * mm, "end": v(20.7, 10.08) * mm});
            skLineSegment(sketch, "E5.5.3.5", {"start": v(12.7, 3.63) * mm, "end": v(14.29, 6.38) * mm});
            skLineSegment(sketch, "E5.5.3.6", {"start": v(23.87, 10.08) * mm, "end": v(25.46, 7.33) * mm});
            skLineSegment(sketch, "E5.5.3.7", {"start": v(23.87, -2.83) * mm, "end": v(20.7, -2.83) * mm});
            skLineSegment(sketch, "E5.5.3.8", {"start": v(25.46, 7.33) * mm, "end": v(23.87, 4.58) * mm});
            skLineSegment(sketch, "E5.5.3.9", {"start": v(12.7, -3.78) * mm, "end": v(14.29, -1.03) * mm});
            skLineSegment(sketch, "E5.5.3.10", {"start": v(17.46, 6.38) * mm, "end": v(19.05, 3.63) * mm});
            skLineSegment(sketch, "E5.5.3.11", {"start": v(19.11, -0.08) * mm, "end": v(20.7, 2.67) * mm});
            skLineSegment(sketch, "E5.5.3.12", {"start": v(20.7, 4.58) * mm, "end": v(19.11, 7.33) * mm});
            skLineSegment(sketch, "E5.5.3.13", {"start": v(17.46, -1.03) * mm, "end": v(19.05, -3.78) * mm});
            skLineSegment(sketch, "E5.5.3.14", {"start": v(20.7, 10.08) * mm, "end": v(23.87, 10.08) * mm});
            skLineSegment(sketch, "E5.5.3.15", {"start": v(17.46, -6.53) * mm, "end": v(14.29, -6.53) * mm});
            skLineSegment(sketch, "E5.5.3.16", {"start": v(14.29, 0.88) * mm, "end": v(12.7, 3.63) * mm});
            skLineSegment(sketch, "E5.5.3.17", {"start": v(25.46, -0.08) * mm, "end": v(23.87, -2.83) * mm});
            skLineSegment(sketch, "E5.5.3.18", {"start": v(14.29, -6.53) * mm, "end": v(12.7, -3.78) * mm});
            skLineSegment(sketch, "E5.5.3.19", {"start": v(14.29, 6.38) * mm, "end": v(17.46, 6.38) * mm});
            skLineSegment(sketch, "E5.5.3.20", {"start": v(20.7, -2.83) * mm, "end": v(19.11, -0.08) * mm});
            skLineSegment(sketch, "E5.5.3.21", {"start": v(23.87, 4.58) * mm, "end": v(20.7, 4.58) * mm});
            skLineSegment(sketch, "E5.5.3.22", {"start": v(14.29, -1.03) * mm, "end": v(17.46, -1.03) * mm});
            skLineSegment(sketch, "E5.5.3.23", {"start": v(19.05, 3.63) * mm, "end": v(17.46, 0.88) * mm});
            skLineSegment(sketch, "E5.5.4.0", {"start": v(20.7, -12.13) * mm, "end": v(23.87, -12.13) * mm});
            skLineSegment(sketch, "E5.5.4.1", {"start": v(17.46, -13.93) * mm, "end": v(14.29, -13.93) * mm});
            skLineSegment(sketch, "E5.5.4.2", {"start": v(19.05, -18.59) * mm, "end": v(17.46, -21.34) * mm});
            skLineSegment(sketch, "E5.5.4.3", {"start": v(23.87, -12.13) * mm, "end": v(25.46, -14.88) * mm});
            skLineSegment(sketch, "E5.5.4.4", {"start": v(19.11, -7.48) * mm, "end": v(20.7, -4.73) * mm});
            skLineSegment(sketch, "E5.5.4.5", {"start": v(12.7, -11.18) * mm, "end": v(14.29, -8.43) * mm});
            skLineSegment(sketch, "E5.5.4.6", {"start": v(23.87, -4.73) * mm, "end": v(25.46, -7.48) * mm});
            skLineSegment(sketch, "E5.5.4.7", {"start": v(23.87, -17.63) * mm, "end": v(20.7, -17.63) * mm});
            skLineSegment(sketch, "E5.5.4.8", {"start": v(25.46, -7.48) * mm, "end": v(23.87, -10.23) * mm});
            skLineSegment(sketch, "E5.5.4.9", {"start": v(12.7, -18.59) * mm, "end": v(14.29, -15.84) * mm});
            skLineSegment(sketch, "E5.5.4.10", {"start": v(17.46, -8.43) * mm, "end": v(19.05, -11.18) * mm});
            skLineSegment(sketch, "E5.5.4.11", {"start": v(19.11, -14.88) * mm, "end": v(20.7, -12.13) * mm});
            skLineSegment(sketch, "E5.5.4.12", {"start": v(20.7, -10.23) * mm, "end": v(19.11, -7.48) * mm});
            skLineSegment(sketch, "E5.5.4.13", {"start": v(17.46, -15.84) * mm, "end": v(19.05, -18.59) * mm});
            skLineSegment(sketch, "E5.5.4.14", {"start": v(20.7, -4.73) * mm, "end": v(23.87, -4.73) * mm});
            skLineSegment(sketch, "E5.5.4.15", {"start": v(17.46, -21.34) * mm, "end": v(14.29, -21.34) * mm});
            skLineSegment(sketch, "E5.5.4.16", {"start": v(14.29, -13.93) * mm, "end": v(12.7, -11.18) * mm});
            skLineSegment(sketch, "E5.5.4.17", {"start": v(25.46, -14.88) * mm, "end": v(23.87, -17.63) * mm});
            skLineSegment(sketch, "E5.5.4.18", {"start": v(14.29, -21.34) * mm, "end": v(12.7, -18.59) * mm});
            skLineSegment(sketch, "E5.5.4.19", {"start": v(14.29, -8.43) * mm, "end": v(17.46, -8.43) * mm});
            skLineSegment(sketch, "E5.5.4.20", {"start": v(20.7, -17.63) * mm, "end": v(19.11, -14.88) * mm});
            skLineSegment(sketch, "E5.5.4.21", {"start": v(23.87, -10.23) * mm, "end": v(20.7, -10.23) * mm});
            skLineSegment(sketch, "E5.5.4.22", {"start": v(14.29, -15.84) * mm, "end": v(17.46, -15.84) * mm});
            skLineSegment(sketch, "E5.5.4.23", {"start": v(19.05, -11.18) * mm, "end": v(17.46, -13.93) * mm});
            skLineSegment(sketch, "E5.5.5.0", {"start": v(20.7, -26.94) * mm, "end": v(23.87, -26.94) * mm});
            skLineSegment(sketch, "E5.5.5.1", {"start": v(17.46, -28.74) * mm, "end": v(14.29, -28.74) * mm});
            skLineSegment(sketch, "E5.5.5.2", {"start": v(19.05, -33.4) * mm, "end": v(17.46, -36.14) * mm});
            skLineSegment(sketch, "E5.5.5.3", {"start": v(23.87, -26.94) * mm, "end": v(25.46, -29.7) * mm});
            skLineSegment(sketch, "E5.5.5.4", {"start": v(19.11, -22.29) * mm, "end": v(20.7, -19.54) * mm});
            skLineSegment(sketch, "E5.5.5.5", {"start": v(12.7, -26) * mm, "end": v(14.29, -23.24) * mm});
            skLineSegment(sketch, "E5.5.5.6", {"start": v(23.87, -19.54) * mm, "end": v(25.46, -22.29) * mm});
            skLineSegment(sketch, "E5.5.5.7", {"start": v(23.87, -32.44) * mm, "end": v(20.7, -32.44) * mm});
            skLineSegment(sketch, "E5.5.5.8", {"start": v(25.46, -22.29) * mm, "end": v(23.87, -25.04) * mm});
            skLineSegment(sketch, "E5.5.5.9", {"start": v(12.7, -33.4) * mm, "end": v(14.29, -30.65) * mm});
            skLineSegment(sketch, "E5.5.5.10", {"start": v(17.46, -23.24) * mm, "end": v(19.05, -26) * mm});
            skLineSegment(sketch, "E5.5.5.11", {"start": v(19.11, -29.7) * mm, "end": v(20.7, -26.94) * mm});
            skLineSegment(sketch, "E5.5.5.12", {"start": v(20.7, -25.04) * mm, "end": v(19.11, -22.29) * mm});
            skLineSegment(sketch, "E5.5.5.13", {"start": v(17.46, -30.65) * mm, "end": v(19.05, -33.4) * mm});
            skLineSegment(sketch, "E5.5.5.14", {"start": v(20.7, -19.54) * mm, "end": v(23.87, -19.54) * mm});
            skLineSegment(sketch, "E5.5.5.15", {"start": v(17.46, -36.14) * mm, "end": v(14.29, -36.14) * mm});
            skLineSegment(sketch, "E5.5.5.16", {"start": v(14.29, -28.74) * mm, "end": v(12.7, -26) * mm});
            skLineSegment(sketch, "E5.5.5.17", {"start": v(25.46, -29.7) * mm, "end": v(23.87, -32.44) * mm});
            skLineSegment(sketch, "E5.5.5.18", {"start": v(14.29, -36.14) * mm, "end": v(12.7, -33.4) * mm});
            skLineSegment(sketch, "E5.5.5.19", {"start": v(14.29, -23.24) * mm, "end": v(17.46, -23.24) * mm});
            skLineSegment(sketch, "E5.5.5.20", {"start": v(20.7, -32.44) * mm, "end": v(19.11, -29.7) * mm});
            skLineSegment(sketch, "E5.5.5.21", {"start": v(23.87, -25.04) * mm, "end": v(20.7, -25.04) * mm});
            skLineSegment(sketch, "E5.5.5.22", {"start": v(14.29, -30.65) * mm, "end": v(17.46, -30.65) * mm});
            skLineSegment(sketch, "E5.5.5.23", {"start": v(19.05, -26) * mm, "end": v(17.46, -28.74) * mm});
            skLineSegment(sketch, "E5.5.6.0", {"start": v(20.7, -41.75) * mm, "end": v(23.87, -41.75) * mm});
            skLineSegment(sketch, "E5.5.6.1", {"start": v(17.46, -43.55) * mm, "end": v(14.29, -43.55) * mm});
            skLineSegment(sketch, "E5.5.6.2", {"start": v(19.05, -48.2) * mm, "end": v(17.46, -50.95) * mm});
            skLineSegment(sketch, "E5.5.6.3", {"start": v(23.87, -41.75) * mm, "end": v(25.46, -44.5) * mm});
            skLineSegment(sketch, "E5.5.6.4", {"start": v(19.11, -37.1) * mm, "end": v(20.7, -34.35) * mm});
            skLineSegment(sketch, "E5.5.6.5", {"start": v(12.7, -40.8) * mm, "end": v(14.29, -38.05) * mm});
            skLineSegment(sketch, "E5.5.6.6", {"start": v(23.87, -34.35) * mm, "end": v(25.46, -37.1) * mm});
            skLineSegment(sketch, "E5.5.6.7", {"start": v(23.87, -47.25) * mm, "end": v(20.7, -47.25) * mm});
            skLineSegment(sketch, "E5.5.6.8", {"start": v(25.46, -37.1) * mm, "end": v(23.87, -39.85) * mm});
            skLineSegment(sketch, "E5.5.6.9", {"start": v(12.7, -48.2) * mm, "end": v(14.29, -45.45) * mm});
            skLineSegment(sketch, "E5.5.6.10", {"start": v(17.46, -38.05) * mm, "end": v(19.05, -40.8) * mm});
            skLineSegment(sketch, "E5.5.6.11", {"start": v(19.11, -44.5) * mm, "end": v(20.7, -41.75) * mm});
            skLineSegment(sketch, "E5.5.6.12", {"start": v(20.7, -39.85) * mm, "end": v(19.11, -37.1) * mm});
            skLineSegment(sketch, "E5.5.6.13", {"start": v(17.46, -45.45) * mm, "end": v(19.05, -48.2) * mm});
            skLineSegment(sketch, "E5.5.6.14", {"start": v(20.7, -34.35) * mm, "end": v(23.87, -34.35) * mm});
            skLineSegment(sketch, "E5.5.6.15", {"start": v(17.46, -50.95) * mm, "end": v(14.29, -50.95) * mm});
            skLineSegment(sketch, "E5.5.6.16", {"start": v(14.29, -43.55) * mm, "end": v(12.7, -40.8) * mm});
            skLineSegment(sketch, "E5.5.6.17", {"start": v(25.46, -44.5) * mm, "end": v(23.87, -47.25) * mm});
            skLineSegment(sketch, "E5.5.6.18", {"start": v(14.29, -50.95) * mm, "end": v(12.7, -48.2) * mm});
            skLineSegment(sketch, "E5.5.6.19", {"start": v(14.29, -38.05) * mm, "end": v(17.46, -38.05) * mm});
            skLineSegment(sketch, "E5.5.6.20", {"start": v(20.7, -47.25) * mm, "end": v(19.11, -44.5) * mm});
            skLineSegment(sketch, "E5.5.6.21", {"start": v(23.87, -39.85) * mm, "end": v(20.7, -39.85) * mm});
            skLineSegment(sketch, "E5.5.6.22", {"start": v(14.29, -45.45) * mm, "end": v(17.46, -45.45) * mm});
            skLineSegment(sketch, "E5.5.6.23", {"start": v(19.05, -40.8) * mm, "end": v(17.46, -43.55) * mm});
            skLineSegment(sketch, "E5.6.0.0", {"start": v(33.4, 47.1) * mm, "end": v(36.57, 47.1) * mm});
            skLineSegment(sketch, "E5.6.0.1", {"start": v(30.16, 45.3) * mm, "end": v(26.99, 45.3) * mm});
            skLineSegment(sketch, "E5.6.0.2", {"start": v(31.75, 40.65) * mm, "end": v(30.16, 37.9) * mm});
            skLineSegment(sketch, "E5.6.0.3", {"start": v(36.57, 47.1) * mm, "end": v(38.16, 44.35) * mm});
            skLineSegment(sketch, "E5.6.0.4", {"start": v(31.81, 51.75) * mm, "end": v(33.4, 54.5) * mm});
            skLineSegment(sketch, "E5.6.0.5", {"start": v(25.4, 48.05) * mm, "end": v(26.99, 50.8) * mm});
            skLineSegment(sketch, "E5.6.0.6", {"start": v(36.57, 54.5) * mm, "end": v(38.16, 51.75) * mm});
            skLineSegment(sketch, "E5.6.0.7", {"start": v(36.57, 41.6) * mm, "end": v(33.4, 41.6) * mm});
            skLineSegment(sketch, "E5.6.0.8", {"start": v(38.16, 51.75) * mm, "end": v(36.57, 49) * mm});
            skLineSegment(sketch, "E5.6.0.9", {"start": v(25.4, 40.65) * mm, "end": v(26.99, 43.4) * mm});
            skLineSegment(sketch, "E5.6.0.10", {"start": v(30.16, 50.8) * mm, "end": v(31.75, 48.05) * mm});
            skLineSegment(sketch, "E5.6.0.11", {"start": v(31.81, 44.35) * mm, "end": v(33.4, 47.1) * mm});
            skLineSegment(sketch, "E5.6.0.12", {"start": v(33.4, 49) * mm, "end": v(31.81, 51.75) * mm});
            skLineSegment(sketch, "E5.6.0.13", {"start": v(30.16, 43.4) * mm, "end": v(31.75, 40.65) * mm});
            skLineSegment(sketch, "E5.6.0.14", {"start": v(33.4, 54.5) * mm, "end": v(36.57, 54.5) * mm});
            skLineSegment(sketch, "E5.6.0.15", {"start": v(30.16, 37.9) * mm, "end": v(26.99, 37.9) * mm});
            skLineSegment(sketch, "E5.6.0.16", {"start": v(26.99, 45.3) * mm, "end": v(25.4, 48.05) * mm});
            skLineSegment(sketch, "E5.6.0.17", {"start": v(38.16, 44.35) * mm, "end": v(36.57, 41.6) * mm});
            skLineSegment(sketch, "E5.6.0.18", {"start": v(26.99, 37.9) * mm, "end": v(25.4, 40.65) * mm});
            skLineSegment(sketch, "E5.6.0.19", {"start": v(26.99, 50.8) * mm, "end": v(30.16, 50.8) * mm});
            skLineSegment(sketch, "E5.6.0.20", {"start": v(33.4, 41.6) * mm, "end": v(31.81, 44.35) * mm});
            skLineSegment(sketch, "E5.6.0.21", {"start": v(36.57, 49) * mm, "end": v(33.4, 49) * mm});
            skLineSegment(sketch, "E5.6.0.22", {"start": v(26.99, 43.4) * mm, "end": v(30.16, 43.4) * mm});
            skLineSegment(sketch, "E5.6.0.23", {"start": v(31.75, 48.05) * mm, "end": v(30.16, 45.3) * mm});
            skLineSegment(sketch, "E5.6.1.0", {"start": v(33.4, 32.29) * mm, "end": v(36.57, 32.29) * mm});
            skLineSegment(sketch, "E5.6.1.1", {"start": v(30.16, 30.5) * mm, "end": v(26.99, 30.5) * mm});
            skLineSegment(sketch, "E5.6.1.2", {"start": v(31.75, 25.84) * mm, "end": v(30.16, 23.09) * mm});
            skLineSegment(sketch, "E5.6.1.3", {"start": v(36.57, 32.29) * mm, "end": v(38.16, 29.54) * mm});
            skLineSegment(sketch, "E5.6.1.4", {"start": v(31.81, 36.94) * mm, "end": v(33.4, 39.7) * mm});
            skLineSegment(sketch, "E5.6.1.5", {"start": v(25.4, 33.24) * mm, "end": v(26.99, 36) * mm});
            skLineSegment(sketch, "E5.6.1.6", {"start": v(36.57, 39.7) * mm, "end": v(38.16, 36.94) * mm});
            skLineSegment(sketch, "E5.6.1.7", {"start": v(36.57, 26.8) * mm, "end": v(33.4, 26.8) * mm});
            skLineSegment(sketch, "E5.6.1.8", {"start": v(38.16, 36.94) * mm, "end": v(36.57, 34.2) * mm});
            skLineSegment(sketch, "E5.6.1.9", {"start": v(25.4, 25.84) * mm, "end": v(26.99, 28.59) * mm});
            skLineSegment(sketch, "E5.6.1.10", {"start": v(30.16, 36) * mm, "end": v(31.75, 33.24) * mm});
            skLineSegment(sketch, "E5.6.1.11", {"start": v(31.81, 29.54) * mm, "end": v(33.4, 32.29) * mm});
            skLineSegment(sketch, "E5.6.1.12", {"start": v(33.4, 34.2) * mm, "end": v(31.81, 36.94) * mm});
            skLineSegment(sketch, "E5.6.1.13", {"start": v(30.16, 28.59) * mm, "end": v(31.75, 25.84) * mm});
            skLineSegment(sketch, "E5.6.1.14", {"start": v(33.4, 39.7) * mm, "end": v(36.57, 39.7) * mm});
            skLineSegment(sketch, "E5.6.1.15", {"start": v(30.16, 23.09) * mm, "end": v(26.99, 23.09) * mm});
            skLineSegment(sketch, "E5.6.1.16", {"start": v(26.99, 30.5) * mm, "end": v(25.4, 33.24) * mm});
            skLineSegment(sketch, "E5.6.1.17", {"start": v(38.16, 29.54) * mm, "end": v(36.57, 26.8) * mm});
            skLineSegment(sketch, "E5.6.1.18", {"start": v(26.99, 23.09) * mm, "end": v(25.4, 25.84) * mm});
            skLineSegment(sketch, "E5.6.1.19", {"start": v(26.99, 36) * mm, "end": v(30.16, 36) * mm});
            skLineSegment(sketch, "E5.6.1.20", {"start": v(33.4, 26.8) * mm, "end": v(31.81, 29.54) * mm});
            skLineSegment(sketch, "E5.6.1.21", {"start": v(36.57, 34.2) * mm, "end": v(33.4, 34.2) * mm});
            skLineSegment(sketch, "E5.6.1.22", {"start": v(26.99, 28.59) * mm, "end": v(30.16, 28.59) * mm});
            skLineSegment(sketch, "E5.6.1.23", {"start": v(31.75, 33.24) * mm, "end": v(30.16, 30.5) * mm});
            skLineSegment(sketch, "E5.6.2.0", {"start": v(33.4, 17.48) * mm, "end": v(36.57, 17.48) * mm});
            skLineSegment(sketch, "E5.6.2.1", {"start": v(30.16, 15.68) * mm, "end": v(26.99, 15.68) * mm});
            skLineSegment(sketch, "E5.6.2.2", {"start": v(31.75, 11.03) * mm, "end": v(30.16, 8.28) * mm});
            skLineSegment(sketch, "E5.6.2.3", {"start": v(36.57, 17.48) * mm, "end": v(38.16, 14.73) * mm});
            skLineSegment(sketch, "E5.6.2.4", {"start": v(31.81, 22.14) * mm, "end": v(33.4, 24.89) * mm});
            skLineSegment(sketch, "E5.6.2.5", {"start": v(25.4, 18.43) * mm, "end": v(26.99, 21.18) * mm});
            skLineSegment(sketch, "E5.6.2.6", {"start": v(36.57, 24.89) * mm, "end": v(38.16, 22.14) * mm});
            skLineSegment(sketch, "E5.6.2.7", {"start": v(36.57, 11.98) * mm, "end": v(33.4, 11.98) * mm});
            skLineSegment(sketch, "E5.6.2.8", {"start": v(38.16, 22.14) * mm, "end": v(36.57, 19.39) * mm});
            skLineSegment(sketch, "E5.6.2.9", {"start": v(25.4, 11.03) * mm, "end": v(26.99, 13.78) * mm});
            skLineSegment(sketch, "E5.6.2.10", {"start": v(30.16, 21.18) * mm, "end": v(31.75, 18.43) * mm});
            skLineSegment(sketch, "E5.6.2.11", {"start": v(31.81, 14.73) * mm, "end": v(33.4, 17.48) * mm});
            skLineSegment(sketch, "E5.6.2.12", {"start": v(33.4, 19.39) * mm, "end": v(31.81, 22.14) * mm});
            skLineSegment(sketch, "E5.6.2.13", {"start": v(30.16, 13.78) * mm, "end": v(31.75, 11.03) * mm});
            skLineSegment(sketch, "E5.6.2.14", {"start": v(33.4, 24.89) * mm, "end": v(36.57, 24.89) * mm});
            skLineSegment(sketch, "E5.6.2.15", {"start": v(30.16, 8.28) * mm, "end": v(26.99, 8.28) * mm});
            skLineSegment(sketch, "E5.6.2.16", {"start": v(26.99, 15.68) * mm, "end": v(25.4, 18.43) * mm});
            skLineSegment(sketch, "E5.6.2.17", {"start": v(38.16, 14.73) * mm, "end": v(36.57, 11.98) * mm});
            skLineSegment(sketch, "E5.6.2.18", {"start": v(26.99, 8.28) * mm, "end": v(25.4, 11.03) * mm});
            skLineSegment(sketch, "E5.6.2.19", {"start": v(26.99, 21.18) * mm, "end": v(30.16, 21.18) * mm});
            skLineSegment(sketch, "E5.6.2.20", {"start": v(33.4, 11.98) * mm, "end": v(31.81, 14.73) * mm});
            skLineSegment(sketch, "E5.6.2.21", {"start": v(36.57, 19.39) * mm, "end": v(33.4, 19.39) * mm});
            skLineSegment(sketch, "E5.6.2.22", {"start": v(26.99, 13.78) * mm, "end": v(30.16, 13.78) * mm});
            skLineSegment(sketch, "E5.6.2.23", {"start": v(31.75, 18.43) * mm, "end": v(30.16, 15.68) * mm});
            skLineSegment(sketch, "E5.6.3.0", {"start": v(33.4, 2.67) * mm, "end": v(36.57, 2.67) * mm});
            skLineSegment(sketch, "E5.6.3.1", {"start": v(30.16, 0.88) * mm, "end": v(26.99, 0.88) * mm});
            skLineSegment(sketch, "E5.6.3.2", {"start": v(31.75, -3.78) * mm, "end": v(30.16, -6.53) * mm});
            skLineSegment(sketch, "E5.6.3.3", {"start": v(36.57, 2.67) * mm, "end": v(38.16, -0.08) * mm});
            skLineSegment(sketch, "E5.6.3.4", {"start": v(31.81, 7.33) * mm, "end": v(33.4, 10.08) * mm});
            skLineSegment(sketch, "E5.6.3.5", {"start": v(25.4, 3.63) * mm, "end": v(26.99, 6.38) * mm});
            skLineSegment(sketch, "E5.6.3.6", {"start": v(36.57, 10.08) * mm, "end": v(38.16, 7.33) * mm});
            skLineSegment(sketch, "E5.6.3.7", {"start": v(36.57, -2.83) * mm, "end": v(33.4, -2.83) * mm});
            skLineSegment(sketch, "E5.6.3.8", {"start": v(38.16, 7.33) * mm, "end": v(36.57, 4.58) * mm});
            skLineSegment(sketch, "E5.6.3.9", {"start": v(25.4, -3.78) * mm, "end": v(26.99, -1.03) * mm});
            skLineSegment(sketch, "E5.6.3.10", {"start": v(30.16, 6.38) * mm, "end": v(31.75, 3.63) * mm});
            skLineSegment(sketch, "E5.6.3.11", {"start": v(31.81, -0.08) * mm, "end": v(33.4, 2.67) * mm});
            skLineSegment(sketch, "E5.6.3.12", {"start": v(33.4, 4.58) * mm, "end": v(31.81, 7.33) * mm});
            skLineSegment(sketch, "E5.6.3.13", {"start": v(30.16, -1.03) * mm, "end": v(31.75, -3.78) * mm});
            skLineSegment(sketch, "E5.6.3.14", {"start": v(33.4, 10.08) * mm, "end": v(36.57, 10.08) * mm});
            skLineSegment(sketch, "E5.6.3.15", {"start": v(30.16, -6.53) * mm, "end": v(26.99, -6.53) * mm});
            skLineSegment(sketch, "E5.6.3.16", {"start": v(26.99, 0.88) * mm, "end": v(25.4, 3.63) * mm});
            skLineSegment(sketch, "E5.6.3.17", {"start": v(38.16, -0.08) * mm, "end": v(36.57, -2.83) * mm});
            skLineSegment(sketch, "E5.6.3.18", {"start": v(26.99, -6.53) * mm, "end": v(25.4, -3.78) * mm});
            skLineSegment(sketch, "E5.6.3.19", {"start": v(26.99, 6.38) * mm, "end": v(30.16, 6.38) * mm});
            skLineSegment(sketch, "E5.6.3.20", {"start": v(33.4, -2.83) * mm, "end": v(31.81, -0.08) * mm});
            skLineSegment(sketch, "E5.6.3.21", {"start": v(36.57, 4.58) * mm, "end": v(33.4, 4.58) * mm});
            skLineSegment(sketch, "E5.6.3.22", {"start": v(26.99, -1.03) * mm, "end": v(30.16, -1.03) * mm});
            skLineSegment(sketch, "E5.6.3.23", {"start": v(31.75, 3.63) * mm, "end": v(30.16, 0.88) * mm});
            skLineSegment(sketch, "E5.6.4.0", {"start": v(33.4, -12.13) * mm, "end": v(36.57, -12.13) * mm});
            skLineSegment(sketch, "E5.6.4.1", {"start": v(30.16, -13.93) * mm, "end": v(26.99, -13.93) * mm});
            skLineSegment(sketch, "E5.6.4.2", {"start": v(31.75, -18.59) * mm, "end": v(30.16, -21.34) * mm});
            skLineSegment(sketch, "E5.6.4.3", {"start": v(36.57, -12.13) * mm, "end": v(38.16, -14.88) * mm});
            skLineSegment(sketch, "E5.6.4.4", {"start": v(31.81, -7.48) * mm, "end": v(33.4, -4.73) * mm});
            skLineSegment(sketch, "E5.6.4.5", {"start": v(25.4, -11.18) * mm, "end": v(26.99, -8.43) * mm});
            skLineSegment(sketch, "E5.6.4.6", {"start": v(36.57, -4.73) * mm, "end": v(38.16, -7.48) * mm});
            skLineSegment(sketch, "E5.6.4.7", {"start": v(36.57, -17.63) * mm, "end": v(33.4, -17.63) * mm});
            skLineSegment(sketch, "E5.6.4.8", {"start": v(38.16, -7.48) * mm, "end": v(36.57, -10.23) * mm});
            skLineSegment(sketch, "E5.6.4.9", {"start": v(25.4, -18.59) * mm, "end": v(26.99, -15.84) * mm});
            skLineSegment(sketch, "E5.6.4.10", {"start": v(30.16, -8.43) * mm, "end": v(31.75, -11.18) * mm});
            skLineSegment(sketch, "E5.6.4.11", {"start": v(31.81, -14.88) * mm, "end": v(33.4, -12.13) * mm});
            skLineSegment(sketch, "E5.6.4.12", {"start": v(33.4, -10.23) * mm, "end": v(31.81, -7.48) * mm});
            skLineSegment(sketch, "E5.6.4.13", {"start": v(30.16, -15.84) * mm, "end": v(31.75, -18.59) * mm});
            skLineSegment(sketch, "E5.6.4.14", {"start": v(33.4, -4.73) * mm, "end": v(36.57, -4.73) * mm});
            skLineSegment(sketch, "E5.6.4.15", {"start": v(30.16, -21.34) * mm, "end": v(26.99, -21.34) * mm});
            skLineSegment(sketch, "E5.6.4.16", {"start": v(26.99, -13.93) * mm, "end": v(25.4, -11.18) * mm});
            skLineSegment(sketch, "E5.6.4.17", {"start": v(38.16, -14.88) * mm, "end": v(36.57, -17.63) * mm});
            skLineSegment(sketch, "E5.6.4.18", {"start": v(26.99, -21.34) * mm, "end": v(25.4, -18.59) * mm});
            skLineSegment(sketch, "E5.6.4.19", {"start": v(26.99, -8.43) * mm, "end": v(30.16, -8.43) * mm});
            skLineSegment(sketch, "E5.6.4.20", {"start": v(33.4, -17.63) * mm, "end": v(31.81, -14.88) * mm});
            skLineSegment(sketch, "E5.6.4.21", {"start": v(36.57, -10.23) * mm, "end": v(33.4, -10.23) * mm});
            skLineSegment(sketch, "E5.6.4.22", {"start": v(26.99, -15.84) * mm, "end": v(30.16, -15.84) * mm});
            skLineSegment(sketch, "E5.6.4.23", {"start": v(31.75, -11.18) * mm, "end": v(30.16, -13.93) * mm});
            skLineSegment(sketch, "E5.6.5.0", {"start": v(33.4, -26.94) * mm, "end": v(36.57, -26.94) * mm});
            skLineSegment(sketch, "E5.6.5.1", {"start": v(30.16, -28.74) * mm, "end": v(26.99, -28.74) * mm});
            skLineSegment(sketch, "E5.6.5.2", {"start": v(31.75, -33.4) * mm, "end": v(30.16, -36.14) * mm});
            skLineSegment(sketch, "E5.6.5.3", {"start": v(36.57, -26.94) * mm, "end": v(38.16, -29.7) * mm});
            skLineSegment(sketch, "E5.6.5.4", {"start": v(31.81, -22.29) * mm, "end": v(33.4, -19.54) * mm});
            skLineSegment(sketch, "E5.6.5.5", {"start": v(25.4, -26) * mm, "end": v(26.99, -23.24) * mm});
            skLineSegment(sketch, "E5.6.5.6", {"start": v(36.57, -19.54) * mm, "end": v(38.16, -22.29) * mm});
            skLineSegment(sketch, "E5.6.5.7", {"start": v(36.57, -32.44) * mm, "end": v(33.4, -32.44) * mm});
            skLineSegment(sketch, "E5.6.5.8", {"start": v(38.16, -22.29) * mm, "end": v(36.57, -25.04) * mm});
            skLineSegment(sketch, "E5.6.5.9", {"start": v(25.4, -33.4) * mm, "end": v(26.99, -30.65) * mm});
            skLineSegment(sketch, "E5.6.5.10", {"start": v(30.16, -23.24) * mm, "end": v(31.75, -26) * mm});
            skLineSegment(sketch, "E5.6.5.11", {"start": v(31.81, -29.7) * mm, "end": v(33.4, -26.94) * mm});
            skLineSegment(sketch, "E5.6.5.12", {"start": v(33.4, -25.04) * mm, "end": v(31.81, -22.29) * mm});
            skLineSegment(sketch, "E5.6.5.13", {"start": v(30.16, -30.65) * mm, "end": v(31.75, -33.4) * mm});
            skLineSegment(sketch, "E5.6.5.14", {"start": v(33.4, -19.54) * mm, "end": v(36.57, -19.54) * mm});
            skLineSegment(sketch, "E5.6.5.15", {"start": v(30.16, -36.14) * mm, "end": v(26.99, -36.14) * mm});
            skLineSegment(sketch, "E5.6.5.16", {"start": v(26.99, -28.74) * mm, "end": v(25.4, -26) * mm});
            skLineSegment(sketch, "E5.6.5.17", {"start": v(38.16, -29.7) * mm, "end": v(36.57, -32.44) * mm});
            skLineSegment(sketch, "E5.6.5.18", {"start": v(26.99, -36.14) * mm, "end": v(25.4, -33.4) * mm});
            skLineSegment(sketch, "E5.6.5.19", {"start": v(26.99, -23.24) * mm, "end": v(30.16, -23.24) * mm});
            skLineSegment(sketch, "E5.6.5.20", {"start": v(33.4, -32.44) * mm, "end": v(31.81, -29.7) * mm});
            skLineSegment(sketch, "E5.6.5.21", {"start": v(36.57, -25.04) * mm, "end": v(33.4, -25.04) * mm});
            skLineSegment(sketch, "E5.6.5.22", {"start": v(26.99, -30.65) * mm, "end": v(30.16, -30.65) * mm});
            skLineSegment(sketch, "E5.6.5.23", {"start": v(31.75, -26) * mm, "end": v(30.16, -28.74) * mm});
            skLineSegment(sketch, "E5.6.6.0", {"start": v(33.4, -41.75) * mm, "end": v(36.57, -41.75) * mm});
            skLineSegment(sketch, "E5.6.6.1", {"start": v(30.16, -43.55) * mm, "end": v(26.99, -43.55) * mm});
            skLineSegment(sketch, "E5.6.6.2", {"start": v(31.75, -48.2) * mm, "end": v(30.16, -50.95) * mm});
            skLineSegment(sketch, "E5.6.6.3", {"start": v(36.57, -41.75) * mm, "end": v(38.16, -44.5) * mm});
            skLineSegment(sketch, "E5.6.6.4", {"start": v(31.81, -37.1) * mm, "end": v(33.4, -34.35) * mm});
            skLineSegment(sketch, "E5.6.6.5", {"start": v(25.4, -40.8) * mm, "end": v(26.99, -38.05) * mm});
            skLineSegment(sketch, "E5.6.6.6", {"start": v(36.57, -34.35) * mm, "end": v(38.16, -37.1) * mm});
            skLineSegment(sketch, "E5.6.6.7", {"start": v(36.57, -47.25) * mm, "end": v(33.4, -47.25) * mm});
            skLineSegment(sketch, "E5.6.6.8", {"start": v(38.16, -37.1) * mm, "end": v(36.57, -39.85) * mm});
            skLineSegment(sketch, "E5.6.6.9", {"start": v(25.4, -48.2) * mm, "end": v(26.99, -45.45) * mm});
            skLineSegment(sketch, "E5.6.6.10", {"start": v(30.16, -38.05) * mm, "end": v(31.75, -40.8) * mm});
            skLineSegment(sketch, "E5.6.6.11", {"start": v(31.81, -44.5) * mm, "end": v(33.4, -41.75) * mm});
            skLineSegment(sketch, "E5.6.6.12", {"start": v(33.4, -39.85) * mm, "end": v(31.81, -37.1) * mm});
            skLineSegment(sketch, "E5.6.6.13", {"start": v(30.16, -45.45) * mm, "end": v(31.75, -48.2) * mm});
            skLineSegment(sketch, "E5.6.6.14", {"start": v(33.4, -34.35) * mm, "end": v(36.57, -34.35) * mm});
            skLineSegment(sketch, "E5.6.6.15", {"start": v(30.16, -50.95) * mm, "end": v(26.99, -50.95) * mm});
            skLineSegment(sketch, "E5.6.6.16", {"start": v(26.99, -43.55) * mm, "end": v(25.4, -40.8) * mm});
            skLineSegment(sketch, "E5.6.6.17", {"start": v(38.16, -44.5) * mm, "end": v(36.57, -47.25) * mm});
            skLineSegment(sketch, "E5.6.6.18", {"start": v(26.99, -50.95) * mm, "end": v(25.4, -48.2) * mm});
            skLineSegment(sketch, "E5.6.6.19", {"start": v(26.99, -38.05) * mm, "end": v(30.16, -38.05) * mm});
            skLineSegment(sketch, "E5.6.6.20", {"start": v(33.4, -47.25) * mm, "end": v(31.81, -44.5) * mm});
            skLineSegment(sketch, "E5.6.6.21", {"start": v(36.57, -39.85) * mm, "end": v(33.4, -39.85) * mm});
            skLineSegment(sketch, "E5.6.6.22", {"start": v(26.99, -45.45) * mm, "end": v(30.16, -45.45) * mm});
            skLineSegment(sketch, "E5.6.6.23", {"start": v(31.75, -40.8) * mm, "end": v(30.16, -43.55) * mm});
            skLineSegment(sketch, "E5.7.0.0", {"start": v(46.1, 47.1) * mm, "end": v(49.27, 47.1) * mm});
            skLineSegment(sketch, "E5.7.0.1", {"start": v(42.86, 45.3) * mm, "end": v(39.69, 45.3) * mm});
            skLineSegment(sketch, "E5.7.0.2", {"start": v(44.45, 40.65) * mm, "end": v(42.86, 37.9) * mm});
            skLineSegment(sketch, "E5.7.0.3", {"start": v(49.27, 47.1) * mm, "end": v(50.86, 44.35) * mm});
            skLineSegment(sketch, "E5.7.0.4", {"start": v(44.51, 51.75) * mm, "end": v(46.1, 54.5) * mm});
            skLineSegment(sketch, "E5.7.0.5", {"start": v(38.1, 48.05) * mm, "end": v(39.69, 50.8) * mm});
            skLineSegment(sketch, "E5.7.0.6", {"start": v(49.27, 54.5) * mm, "end": v(50.86, 51.75) * mm});
            skLineSegment(sketch, "E5.7.0.7", {"start": v(49.27, 41.6) * mm, "end": v(46.1, 41.6) * mm});
            skLineSegment(sketch, "E5.7.0.8", {"start": v(50.86, 51.75) * mm, "end": v(49.27, 49) * mm});
            skLineSegment(sketch, "E5.7.0.9", {"start": v(38.1, 40.65) * mm, "end": v(39.69, 43.4) * mm});
            skLineSegment(sketch, "E5.7.0.10", {"start": v(42.86, 50.8) * mm, "end": v(44.45, 48.05) * mm});
            skLineSegment(sketch, "E5.7.0.11", {"start": v(44.51, 44.35) * mm, "end": v(46.1, 47.1) * mm});
            skLineSegment(sketch, "E5.7.0.12", {"start": v(46.1, 49) * mm, "end": v(44.51, 51.75) * mm});
            skLineSegment(sketch, "E5.7.0.13", {"start": v(42.86, 43.4) * mm, "end": v(44.45, 40.65) * mm});
            skLineSegment(sketch, "E5.7.0.14", {"start": v(46.1, 54.5) * mm, "end": v(49.27, 54.5) * mm});
            skLineSegment(sketch, "E5.7.0.15", {"start": v(42.86, 37.9) * mm, "end": v(39.69, 37.9) * mm});
            skLineSegment(sketch, "E5.7.0.16", {"start": v(39.69, 45.3) * mm, "end": v(38.1, 48.05) * mm});
            skLineSegment(sketch, "E5.7.0.17", {"start": v(50.86, 44.35) * mm, "end": v(49.27, 41.6) * mm});
            skLineSegment(sketch, "E5.7.0.18", {"start": v(39.69, 37.9) * mm, "end": v(38.1, 40.65) * mm});
            skLineSegment(sketch, "E5.7.0.19", {"start": v(39.69, 50.8) * mm, "end": v(42.86, 50.8) * mm});
            skLineSegment(sketch, "E5.7.0.20", {"start": v(46.1, 41.6) * mm, "end": v(44.51, 44.35) * mm});
            skLineSegment(sketch, "E5.7.0.21", {"start": v(49.27, 49) * mm, "end": v(46.1, 49) * mm});
            skLineSegment(sketch, "E5.7.0.22", {"start": v(39.69, 43.4) * mm, "end": v(42.86, 43.4) * mm});
            skLineSegment(sketch, "E5.7.0.23", {"start": v(44.45, 48.05) * mm, "end": v(42.86, 45.3) * mm});
            skLineSegment(sketch, "E5.7.1.0", {"start": v(46.1, 32.29) * mm, "end": v(49.27, 32.29) * mm});
            skLineSegment(sketch, "E5.7.1.1", {"start": v(42.86, 30.5) * mm, "end": v(39.69, 30.5) * mm});
            skLineSegment(sketch, "E5.7.1.2", {"start": v(44.45, 25.84) * mm, "end": v(42.86, 23.09) * mm});
            skLineSegment(sketch, "E5.7.1.3", {"start": v(49.27, 32.29) * mm, "end": v(50.86, 29.54) * mm});
            skLineSegment(sketch, "E5.7.1.4", {"start": v(44.51, 36.94) * mm, "end": v(46.1, 39.7) * mm});
            skLineSegment(sketch, "E5.7.1.5", {"start": v(38.1, 33.24) * mm, "end": v(39.69, 36) * mm});
            skLineSegment(sketch, "E5.7.1.6", {"start": v(49.27, 39.7) * mm, "end": v(50.86, 36.94) * mm});
            skLineSegment(sketch, "E5.7.1.7", {"start": v(49.27, 26.8) * mm, "end": v(46.1, 26.8) * mm});
            skLineSegment(sketch, "E5.7.1.8", {"start": v(50.86, 36.94) * mm, "end": v(49.27, 34.2) * mm});
            skLineSegment(sketch, "E5.7.1.9", {"start": v(38.1, 25.84) * mm, "end": v(39.69, 28.59) * mm});
            skLineSegment(sketch, "E5.7.1.10", {"start": v(42.86, 36) * mm, "end": v(44.45, 33.24) * mm});
            skLineSegment(sketch, "E5.7.1.11", {"start": v(44.51, 29.54) * mm, "end": v(46.1, 32.29) * mm});
            skLineSegment(sketch, "E5.7.1.12", {"start": v(46.1, 34.2) * mm, "end": v(44.51, 36.94) * mm});
            skLineSegment(sketch, "E5.7.1.13", {"start": v(42.86, 28.59) * mm, "end": v(44.45, 25.84) * mm});
            skLineSegment(sketch, "E5.7.1.14", {"start": v(46.1, 39.7) * mm, "end": v(49.27, 39.7) * mm});
            skLineSegment(sketch, "E5.7.1.15", {"start": v(42.86, 23.09) * mm, "end": v(39.69, 23.09) * mm});
            skLineSegment(sketch, "E5.7.1.16", {"start": v(39.69, 30.5) * mm, "end": v(38.1, 33.24) * mm});
            skLineSegment(sketch, "E5.7.1.17", {"start": v(50.86, 29.54) * mm, "end": v(49.27, 26.8) * mm});
            skLineSegment(sketch, "E5.7.1.18", {"start": v(39.69, 23.09) * mm, "end": v(38.1, 25.84) * mm});
            skLineSegment(sketch, "E5.7.1.19", {"start": v(39.69, 36) * mm, "end": v(42.86, 36) * mm});
            skLineSegment(sketch, "E5.7.1.20", {"start": v(46.1, 26.8) * mm, "end": v(44.51, 29.54) * mm});
            skLineSegment(sketch, "E5.7.1.21", {"start": v(49.27, 34.2) * mm, "end": v(46.1, 34.2) * mm});
            skLineSegment(sketch, "E5.7.1.22", {"start": v(39.69, 28.59) * mm, "end": v(42.86, 28.59) * mm});
            skLineSegment(sketch, "E5.7.1.23", {"start": v(44.45, 33.24) * mm, "end": v(42.86, 30.5) * mm});
            skLineSegment(sketch, "E5.7.2.0", {"start": v(46.1, 17.48) * mm, "end": v(49.27, 17.48) * mm});
            skLineSegment(sketch, "E5.7.2.1", {"start": v(42.86, 15.68) * mm, "end": v(39.69, 15.68) * mm});
            skLineSegment(sketch, "E5.7.2.2", {"start": v(44.45, 11.03) * mm, "end": v(42.86, 8.28) * mm});
            skLineSegment(sketch, "E5.7.2.3", {"start": v(49.27, 17.48) * mm, "end": v(50.86, 14.73) * mm});
            skLineSegment(sketch, "E5.7.2.4", {"start": v(44.51, 22.14) * mm, "end": v(46.1, 24.89) * mm});
            skLineSegment(sketch, "E5.7.2.5", {"start": v(38.1, 18.43) * mm, "end": v(39.69, 21.18) * mm});
            skLineSegment(sketch, "E5.7.2.6", {"start": v(49.27, 24.89) * mm, "end": v(50.86, 22.14) * mm});
            skLineSegment(sketch, "E5.7.2.7", {"start": v(49.27, 11.98) * mm, "end": v(46.1, 11.98) * mm});
            skLineSegment(sketch, "E5.7.2.8", {"start": v(50.86, 22.14) * mm, "end": v(49.27, 19.39) * mm});
            skLineSegment(sketch, "E5.7.2.9", {"start": v(38.1, 11.03) * mm, "end": v(39.69, 13.78) * mm});
            skLineSegment(sketch, "E5.7.2.10", {"start": v(42.86, 21.18) * mm, "end": v(44.45, 18.43) * mm});
            skLineSegment(sketch, "E5.7.2.11", {"start": v(44.51, 14.73) * mm, "end": v(46.1, 17.48) * mm});
            skLineSegment(sketch, "E5.7.2.12", {"start": v(46.1, 19.39) * mm, "end": v(44.51, 22.14) * mm});
            skLineSegment(sketch, "E5.7.2.13", {"start": v(42.86, 13.78) * mm, "end": v(44.45, 11.03) * mm});
            skLineSegment(sketch, "E5.7.2.14", {"start": v(46.1, 24.89) * mm, "end": v(49.27, 24.89) * mm});
            skLineSegment(sketch, "E5.7.2.15", {"start": v(42.86, 8.28) * mm, "end": v(39.69, 8.28) * mm});
            skLineSegment(sketch, "E5.7.2.16", {"start": v(39.69, 15.68) * mm, "end": v(38.1, 18.43) * mm});
            skLineSegment(sketch, "E5.7.2.17", {"start": v(50.86, 14.73) * mm, "end": v(49.27, 11.98) * mm});
            skLineSegment(sketch, "E5.7.2.18", {"start": v(39.69, 8.28) * mm, "end": v(38.1, 11.03) * mm});
            skLineSegment(sketch, "E5.7.2.19", {"start": v(39.69, 21.18) * mm, "end": v(42.86, 21.18) * mm});
            skLineSegment(sketch, "E5.7.2.20", {"start": v(46.1, 11.98) * mm, "end": v(44.51, 14.73) * mm});
            skLineSegment(sketch, "E5.7.2.21", {"start": v(49.27, 19.39) * mm, "end": v(46.1, 19.39) * mm});
            skLineSegment(sketch, "E5.7.2.22", {"start": v(39.69, 13.78) * mm, "end": v(42.86, 13.78) * mm});
            skLineSegment(sketch, "E5.7.2.23", {"start": v(44.45, 18.43) * mm, "end": v(42.86, 15.68) * mm});
            skLineSegment(sketch, "E5.7.3.0", {"start": v(46.1, 2.67) * mm, "end": v(49.27, 2.67) * mm});
            skLineSegment(sketch, "E5.7.3.1", {"start": v(42.86, 0.88) * mm, "end": v(39.69, 0.88) * mm});
            skLineSegment(sketch, "E5.7.3.2", {"start": v(44.45, -3.78) * mm, "end": v(42.86, -6.53) * mm});
            skLineSegment(sketch, "E5.7.3.3", {"start": v(49.27, 2.67) * mm, "end": v(50.86, -0.08) * mm});
            skLineSegment(sketch, "E5.7.3.4", {"start": v(44.51, 7.33) * mm, "end": v(46.1, 10.08) * mm});
            skLineSegment(sketch, "E5.7.3.5", {"start": v(38.1, 3.63) * mm, "end": v(39.69, 6.38) * mm});
            skLineSegment(sketch, "E5.7.3.6", {"start": v(49.27, 10.08) * mm, "end": v(50.86, 7.33) * mm});
            skLineSegment(sketch, "E5.7.3.7", {"start": v(49.27, -2.83) * mm, "end": v(46.1, -2.83) * mm});
            skLineSegment(sketch, "E5.7.3.8", {"start": v(50.86, 7.33) * mm, "end": v(49.27, 4.58) * mm});
            skLineSegment(sketch, "E5.7.3.9", {"start": v(38.1, -3.78) * mm, "end": v(39.69, -1.03) * mm});
            skLineSegment(sketch, "E5.7.3.10", {"start": v(42.86, 6.38) * mm, "end": v(44.45, 3.63) * mm});
            skLineSegment(sketch, "E5.7.3.11", {"start": v(44.51, -0.08) * mm, "end": v(46.1, 2.67) * mm});
            skLineSegment(sketch, "E5.7.3.12", {"start": v(46.1, 4.58) * mm, "end": v(44.51, 7.33) * mm});
            skLineSegment(sketch, "E5.7.3.13", {"start": v(42.86, -1.03) * mm, "end": v(44.45, -3.78) * mm});
            skLineSegment(sketch, "E5.7.3.14", {"start": v(46.1, 10.08) * mm, "end": v(49.27, 10.08) * mm});
            skLineSegment(sketch, "E5.7.3.15", {"start": v(42.86, -6.53) * mm, "end": v(39.69, -6.53) * mm});
            skLineSegment(sketch, "E5.7.3.16", {"start": v(39.69, 0.88) * mm, "end": v(38.1, 3.63) * mm});
            skLineSegment(sketch, "E5.7.3.17", {"start": v(50.86, -0.08) * mm, "end": v(49.27, -2.83) * mm});
            skLineSegment(sketch, "E5.7.3.18", {"start": v(39.69, -6.53) * mm, "end": v(38.1, -3.78) * mm});
            skLineSegment(sketch, "E5.7.3.19", {"start": v(39.69, 6.38) * mm, "end": v(42.86, 6.38) * mm});
            skLineSegment(sketch, "E5.7.3.20", {"start": v(46.1, -2.83) * mm, "end": v(44.51, -0.08) * mm});
            skLineSegment(sketch, "E5.7.3.21", {"start": v(49.27, 4.58) * mm, "end": v(46.1, 4.58) * mm});
            skLineSegment(sketch, "E5.7.3.22", {"start": v(39.69, -1.03) * mm, "end": v(42.86, -1.03) * mm});
            skLineSegment(sketch, "E5.7.3.23", {"start": v(44.45, 3.63) * mm, "end": v(42.86, 0.88) * mm});
            skLineSegment(sketch, "E5.7.4.0", {"start": v(46.1, -12.13) * mm, "end": v(49.27, -12.13) * mm});
            skLineSegment(sketch, "E5.7.4.1", {"start": v(42.86, -13.93) * mm, "end": v(39.69, -13.93) * mm});
            skLineSegment(sketch, "E5.7.4.2", {"start": v(44.45, -18.59) * mm, "end": v(42.86, -21.34) * mm});
            skLineSegment(sketch, "E5.7.4.3", {"start": v(49.27, -12.13) * mm, "end": v(50.86, -14.88) * mm});
            skLineSegment(sketch, "E5.7.4.4", {"start": v(44.51, -7.48) * mm, "end": v(46.1, -4.73) * mm});
            skLineSegment(sketch, "E5.7.4.5", {"start": v(38.1, -11.18) * mm, "end": v(39.69, -8.43) * mm});
            skLineSegment(sketch, "E5.7.4.6", {"start": v(49.27, -4.73) * mm, "end": v(50.86, -7.48) * mm});
            skLineSegment(sketch, "E5.7.4.7", {"start": v(49.27, -17.63) * mm, "end": v(46.1, -17.63) * mm});
            skLineSegment(sketch, "E5.7.4.8", {"start": v(50.86, -7.48) * mm, "end": v(49.27, -10.23) * mm});
            skLineSegment(sketch, "E5.7.4.9", {"start": v(38.1, -18.59) * mm, "end": v(39.69, -15.84) * mm});
            skLineSegment(sketch, "E5.7.4.10", {"start": v(42.86, -8.43) * mm, "end": v(44.45, -11.18) * mm});
            skLineSegment(sketch, "E5.7.4.11", {"start": v(44.51, -14.88) * mm, "end": v(46.1, -12.13) * mm});
            skLineSegment(sketch, "E5.7.4.12", {"start": v(46.1, -10.23) * mm, "end": v(44.51, -7.48) * mm});
            skLineSegment(sketch, "E5.7.4.13", {"start": v(42.86, -15.84) * mm, "end": v(44.45, -18.59) * mm});
            skLineSegment(sketch, "E5.7.4.14", {"start": v(46.1, -4.73) * mm, "end": v(49.27, -4.73) * mm});
            skLineSegment(sketch, "E5.7.4.15", {"start": v(42.86, -21.34) * mm, "end": v(39.69, -21.34) * mm});
            skLineSegment(sketch, "E5.7.4.16", {"start": v(39.69, -13.93) * mm, "end": v(38.1, -11.18) * mm});
            skLineSegment(sketch, "E5.7.4.17", {"start": v(50.86, -14.88) * mm, "end": v(49.27, -17.63) * mm});
            skLineSegment(sketch, "E5.7.4.18", {"start": v(39.69, -21.34) * mm, "end": v(38.1, -18.59) * mm});
            skLineSegment(sketch, "E5.7.4.19", {"start": v(39.69, -8.43) * mm, "end": v(42.86, -8.43) * mm});
            skLineSegment(sketch, "E5.7.4.20", {"start": v(46.1, -17.63) * mm, "end": v(44.51, -14.88) * mm});
            skLineSegment(sketch, "E5.7.4.21", {"start": v(49.27, -10.23) * mm, "end": v(46.1, -10.23) * mm});
            skLineSegment(sketch, "E5.7.4.22", {"start": v(39.69, -15.84) * mm, "end": v(42.86, -15.84) * mm});
            skLineSegment(sketch, "E5.7.4.23", {"start": v(44.45, -11.18) * mm, "end": v(42.86, -13.93) * mm});
            skLineSegment(sketch, "E5.7.5.0", {"start": v(46.1, -26.94) * mm, "end": v(49.27, -26.94) * mm});
            skLineSegment(sketch, "E5.7.5.1", {"start": v(42.86, -28.74) * mm, "end": v(39.69, -28.74) * mm});
            skLineSegment(sketch, "E5.7.5.2", {"start": v(44.45, -33.4) * mm, "end": v(42.86, -36.14) * mm});
            skLineSegment(sketch, "E5.7.5.3", {"start": v(49.27, -26.94) * mm, "end": v(50.86, -29.7) * mm});
            skLineSegment(sketch, "E5.7.5.4", {"start": v(44.51, -22.29) * mm, "end": v(46.1, -19.54) * mm});
            skLineSegment(sketch, "E5.7.5.5", {"start": v(38.1, -26) * mm, "end": v(39.69, -23.24) * mm});
            skLineSegment(sketch, "E5.7.5.6", {"start": v(49.27, -19.54) * mm, "end": v(50.86, -22.29) * mm});
            skLineSegment(sketch, "E5.7.5.7", {"start": v(49.27, -32.44) * mm, "end": v(46.1, -32.44) * mm});
            skLineSegment(sketch, "E5.7.5.8", {"start": v(50.86, -22.29) * mm, "end": v(49.27, -25.04) * mm});
            skLineSegment(sketch, "E5.7.5.9", {"start": v(38.1, -33.4) * mm, "end": v(39.69, -30.65) * mm});
            skLineSegment(sketch, "E5.7.5.10", {"start": v(42.86, -23.24) * mm, "end": v(44.45, -26) * mm});
            skLineSegment(sketch, "E5.7.5.11", {"start": v(44.51, -29.7) * mm, "end": v(46.1, -26.94) * mm});
            skLineSegment(sketch, "E5.7.5.12", {"start": v(46.1, -25.04) * mm, "end": v(44.51, -22.29) * mm});
            skLineSegment(sketch, "E5.7.5.13", {"start": v(42.86, -30.65) * mm, "end": v(44.45, -33.4) * mm});
            skLineSegment(sketch, "E5.7.5.14", {"start": v(46.1, -19.54) * mm, "end": v(49.27, -19.54) * mm});
            skLineSegment(sketch, "E5.7.5.15", {"start": v(42.86, -36.14) * mm, "end": v(39.69, -36.14) * mm});
            skLineSegment(sketch, "E5.7.5.16", {"start": v(39.69, -28.74) * mm, "end": v(38.1, -26) * mm});
            skLineSegment(sketch, "E5.7.5.17", {"start": v(50.86, -29.7) * mm, "end": v(49.27, -32.44) * mm});
            skLineSegment(sketch, "E5.7.5.18", {"start": v(39.69, -36.14) * mm, "end": v(38.1, -33.4) * mm});
            skLineSegment(sketch, "E5.7.5.19", {"start": v(39.69, -23.24) * mm, "end": v(42.86, -23.24) * mm});
            skLineSegment(sketch, "E5.7.5.20", {"start": v(46.1, -32.44) * mm, "end": v(44.51, -29.7) * mm});
            skLineSegment(sketch, "E5.7.5.21", {"start": v(49.27, -25.04) * mm, "end": v(46.1, -25.04) * mm});
            skLineSegment(sketch, "E5.7.5.22", {"start": v(39.69, -30.65) * mm, "end": v(42.86, -30.65) * mm});
            skLineSegment(sketch, "E5.7.5.23", {"start": v(44.45, -26) * mm, "end": v(42.86, -28.74) * mm});
            skLineSegment(sketch, "E5.7.6.0", {"start": v(46.1, -41.75) * mm, "end": v(49.27, -41.75) * mm});
            skLineSegment(sketch, "E5.7.6.1", {"start": v(42.86, -43.55) * mm, "end": v(39.69, -43.55) * mm});
            skLineSegment(sketch, "E5.7.6.2", {"start": v(44.45, -48.2) * mm, "end": v(42.86, -50.95) * mm});
            skLineSegment(sketch, "E5.7.6.3", {"start": v(49.27, -41.75) * mm, "end": v(50.86, -44.5) * mm});
            skLineSegment(sketch, "E5.7.6.4", {"start": v(44.51, -37.1) * mm, "end": v(46.1, -34.35) * mm});
            skLineSegment(sketch, "E5.7.6.5", {"start": v(38.1, -40.8) * mm, "end": v(39.69, -38.05) * mm});
            skLineSegment(sketch, "E5.7.6.6", {"start": v(49.27, -34.35) * mm, "end": v(50.86, -37.1) * mm});
            skLineSegment(sketch, "E5.7.6.7", {"start": v(49.27, -47.25) * mm, "end": v(46.1, -47.25) * mm});
            skLineSegment(sketch, "E5.7.6.8", {"start": v(50.86, -37.1) * mm, "end": v(49.27, -39.85) * mm});
            skLineSegment(sketch, "E5.7.6.9", {"start": v(38.1, -48.2) * mm, "end": v(39.69, -45.45) * mm});
            skLineSegment(sketch, "E5.7.6.10", {"start": v(42.86, -38.05) * mm, "end": v(44.45, -40.8) * mm});
            skLineSegment(sketch, "E5.7.6.11", {"start": v(44.51, -44.5) * mm, "end": v(46.1, -41.75) * mm});
            skLineSegment(sketch, "E5.7.6.12", {"start": v(46.1, -39.85) * mm, "end": v(44.51, -37.1) * mm});
            skLineSegment(sketch, "E5.7.6.13", {"start": v(42.86, -45.45) * mm, "end": v(44.45, -48.2) * mm});
            skLineSegment(sketch, "E5.7.6.14", {"start": v(46.1, -34.35) * mm, "end": v(49.27, -34.35) * mm});
            skLineSegment(sketch, "E5.7.6.15", {"start": v(42.86, -50.95) * mm, "end": v(39.69, -50.95) * mm});
            skLineSegment(sketch, "E5.7.6.16", {"start": v(39.69, -43.55) * mm, "end": v(38.1, -40.8) * mm});
            skLineSegment(sketch, "E5.7.6.17", {"start": v(50.86, -44.5) * mm, "end": v(49.27, -47.25) * mm});
            skLineSegment(sketch, "E5.7.6.18", {"start": v(39.69, -50.95) * mm, "end": v(38.1, -48.2) * mm});
            skLineSegment(sketch, "E5.7.6.19", {"start": v(39.69, -38.05) * mm, "end": v(42.86, -38.05) * mm});
            skLineSegment(sketch, "E5.7.6.20", {"start": v(46.1, -47.25) * mm, "end": v(44.51, -44.5) * mm});
            skLineSegment(sketch, "E5.7.6.21", {"start": v(49.27, -39.85) * mm, "end": v(46.1, -39.85) * mm});
            skLineSegment(sketch, "E5.7.6.22", {"start": v(39.69, -45.45) * mm, "end": v(42.86, -45.45) * mm});
            skLineSegment(sketch, "E5.7.6.23", {"start": v(44.45, -40.8) * mm, "end": v(42.86, -43.55) * mm});
            skLineSegment(sketch, "E5.direction1", {"start": v(-49.21, 50.8) * mm, "end": v(-36.51, 50.8) * mm, "construction": true});
            skLineSegment(sketch, "E5.direction2", {"start": v(-49.21, 50.8) * mm, "end": v(-49.21, 36) * mm, "construction": true});
            skCircle(sketch, "E6", {"center": v(0, 0) * mm, "radius": 47.63 * mm});
            skSolve(sketch);
        }
        {
            var Q0;
            Q0=makeQuery(id+"F0.imprint","IMPRINT",FACE,{"disambiguationData":[TD([[makeQuery(id+"F0.imprint","IMPRINT",EDGE,{"derivedFrom":sQuery(id+"F0.wireOp",EDGE,"E5.0.2.0")}),1.0]])]});
            extrude(context, id + "F1", {"entities" : qUnion([Q0]), "depth" : 3.8 * mm, "offsetDistance" : 25.4 * mm});
        }
        {
            var Q0;
            Q0=qCreatedBy(makeId("Top.planeOp"),FACE);
            var sketch = newSketch(context, id + "F2", { "sketchPlane" : qUnion([Q0])});
            skCircle(sketch, "E7", {"center": v(0, 0) * mm, "radius": 47.63 * mm});
            skCircle(sketch, "E8", {"center": v(0, 0) * mm, "radius": 50.8 * mm});
            skSolve(sketch);
        }
        {
            var Q0;
            Q0 = qSketchRegion(id + "F2", true);
            extrude(context, id + "F3", {"entities" : qUnion([Q0]), "operationType" : NewBodyOperationType.ADD, "depth" : 5.08 * mm, "offsetDistance" : 25.4 * mm});
        }
    });
